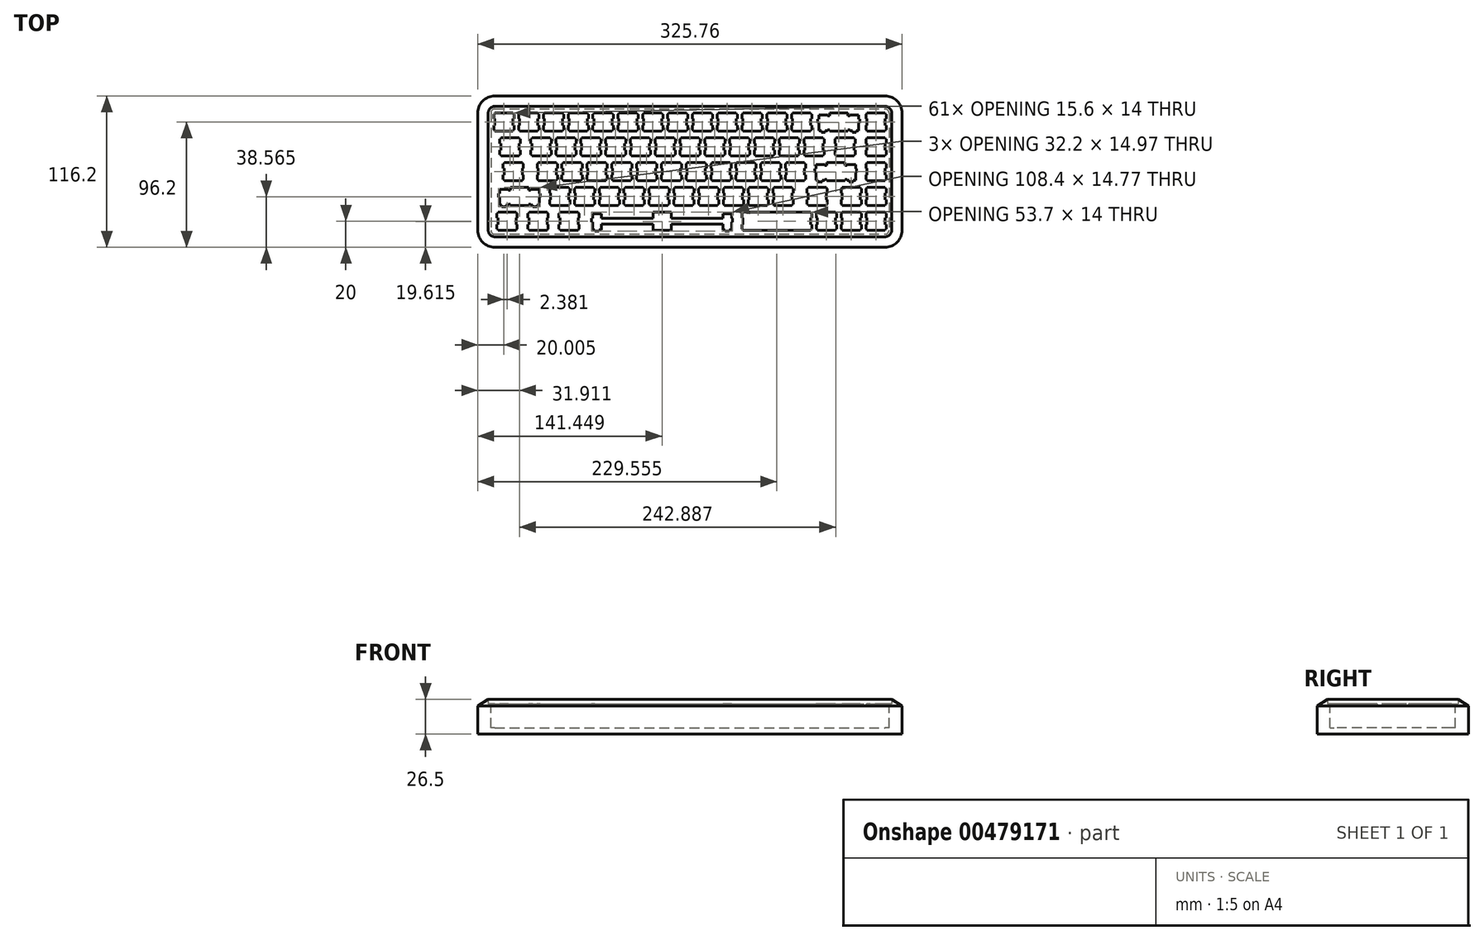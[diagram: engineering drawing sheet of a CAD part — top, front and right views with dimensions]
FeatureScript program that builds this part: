
annotation { "Feature Type Name" : "Feature", "Feature Type Description" : "" }
export const myFeature = defineFeature(function(context is Context, id is Id, definition is map)
    precondition{}
    {
        {
            var Q0;
            Q0=qCreatedBy(makeId("Top.planeOp"),FACE);
            var sketch = newSketch(context, id + "F0", { "sketchPlane" : qUnion([Q0])});
            skLineSegment(sketch, "E0", {"start": v(-116.54, 8.8) * mm, "end": v(-102.54, 8.8) * mm});
            skLineSegment(sketch, "E1", {"start": v(-78.44, 8.8) * mm, "end": v(-64.44, 8.8) * mm});
            skLineSegment(sketch, "E2", {"start": v(-97.49, 8.8) * mm, "end": v(-83.49, 8.8) * mm});
            skLineSegment(sketch, "E3", {"start": v(-40.34, 8.8) * mm, "end": v(-26.34, 8.8) * mm});
            skLineSegment(sketch, "E4", {"start": v(-59.39, 8.8) * mm, "end": v(-45.39, 8.8) * mm});
            skLineSegment(sketch, "E5", {"start": v(-21.29, 8.8) * mm, "end": v(-7.29, 8.8) * mm});
            skLineSegment(sketch, "E6", {"start": v(12.05, 27.85) * mm, "end": v(26.05, 27.85) * mm});
            skLineSegment(sketch, "E7", {"start": v(50.15, 27.85) * mm, "end": v(64.15, 27.85) * mm});
            skLineSegment(sketch, "E8", {"start": v(31.1, 27.85) * mm, "end": v(45.1, 27.85) * mm});
            skLineSegment(sketch, "E9", {"start": v(69.2, 27.85) * mm, "end": v(83.2, 27.85) * mm});
            skLineSegment(sketch, "E10", {"start": v(88.25, 27.85) * mm, "end": v(102.25, 27.85) * mm});
            skLineSegment(sketch, "E11", {"start": v(78.72, 46.9) * mm, "end": v(92.73, 46.9) * mm});
            skLineSegment(sketch, "E12", {"start": v(59.68, 46.9) * mm, "end": v(73.68, 46.9) * mm});
            skLineSegment(sketch, "E13", {"start": v(149.88, 46.9) * mm, "end": v(135.88, 46.9) * mm});
            skLineSegment(sketch, "E14", {"start": v(-145.11, 27.85) * mm, "end": v(-131.11, 27.85) * mm});
            skLineSegment(sketch, "E15", {"start": v(-102.25, 27.85) * mm, "end": v(-88.25, 27.85) * mm});
            skLineSegment(sketch, "E16", {"start": v(-121.3, 27.85) * mm, "end": v(-107.3, 27.85) * mm});
            skLineSegment(sketch, "E17", {"start": v(-83.2, 27.85) * mm, "end": v(-69.2, 27.85) * mm});
            skLineSegment(sketch, "E18", {"start": v(-45.1, 27.85) * mm, "end": v(-31.1, 27.85) * mm});
            skLineSegment(sketch, "E19", {"start": v(-64.15, 27.85) * mm, "end": v(-50.15, 27.85) * mm});
            skLineSegment(sketch, "E20", {"start": v(-7, 27.85) * mm, "end": v(7, 27.85) * mm});
            skLineSegment(sketch, "E21", {"start": v(-26.05, 27.85) * mm, "end": v(-12.05, 27.85) * mm});
            skLineSegment(sketch, "E22", {"start": v(-149.88, 46.9) * mm, "end": v(-135.88, 46.9) * mm});
            skLineSegment(sketch, "E23", {"start": v(-111.78, 46.9) * mm, "end": v(-97.78, 46.9) * mm});
            skLineSegment(sketch, "E24", {"start": v(-130.82, 46.9) * mm, "end": v(-116.83, 46.9) * mm});
            skLineSegment(sketch, "E25", {"start": v(-73.68, 46.9) * mm, "end": v(-59.67, 46.9) * mm});
            skLineSegment(sketch, "E26", {"start": v(-92.73, 46.9) * mm, "end": v(-78.72, 46.9) * mm});
            skLineSegment(sketch, "E27", {"start": v(-54.62, 46.9) * mm, "end": v(-40.62, 46.9) * mm});
            skLineSegment(sketch, "E28", {"start": v(-16.53, 46.9) * mm, "end": v(-2.53, 46.9) * mm});
            skLineSegment(sketch, "E29", {"start": v(-35.58, 46.9) * mm, "end": v(-21.57, 46.9) * mm});
            skLineSegment(sketch, "E30", {"start": v(2.53, 46.9) * mm, "end": v(16.53, 46.9) * mm});
            skLineSegment(sketch, "E31", {"start": v(40.62, 46.9) * mm, "end": v(54.62, 46.9) * mm});
            skLineSegment(sketch, "E32", {"start": v(21.57, 46.9) * mm, "end": v(35.57, 46.9) * mm});
            skLineSegment(sketch, "E33", {"start": v(130.82, -29.3) * mm, "end": v(116.82, -29.3) * mm});
            skLineSegment(sketch, "E34", {"start": v(111.77, -29.3) * mm, "end": v(97.78, -29.3) * mm});
            skLineSegment(sketch, "E35", {"start": v(7.29, -10.25) * mm, "end": v(21.29, -10.25) * mm});
            skLineSegment(sketch, "E36", {"start": v(-11.76, -10.25) * mm, "end": v(2.24, -10.25) * mm});
            skLineSegment(sketch, "E37", {"start": v(26.34, -10.25) * mm, "end": v(40.34, -10.25) * mm});
            skLineSegment(sketch, "E38", {"start": v(64.44, -10.25) * mm, "end": v(78.44, -10.25) * mm});
            skLineSegment(sketch, "E39", {"start": v(45.39, -10.25) * mm, "end": v(59.39, -10.25) * mm});
            skLineSegment(sketch, "E40", {"start": v(90.63, -10.25) * mm, "end": v(104.63, -10.25) * mm});
            skLineSegment(sketch, "E41", {"start": v(149.88, -10.25) * mm, "end": v(135.88, -10.25) * mm});
            skLineSegment(sketch, "E42", {"start": v(130.82, -10.25) * mm, "end": v(116.82, -10.25) * mm});
            skLineSegment(sketch, "E43", {"start": v(-123.68, -29.3) * mm, "end": v(-109.68, -29.3) * mm});
            skLineSegment(sketch, "E44", {"start": v(-147.5, -29.3) * mm, "end": v(-133.5, -29.3) * mm});
            skLineSegment(sketch, "E45", {"start": v(-99.87, -29.3) * mm, "end": v(-85.87, -29.3) * mm});
            skLineSegment(sketch, "E46", {"start": v(149.88, -29.3) * mm, "end": v(135.88, -29.3) * mm});
            skLineSegment(sketch, "E47", {"start": v(-28.43, -29.3) * mm, "end": v(-14.43, -29.3) * mm});
            skLineSegment(sketch, "E48", {"start": v(16.81, 8.8) * mm, "end": v(30.81, 8.8) * mm});
            skLineSegment(sketch, "E49", {"start": v(-2.24, 8.8) * mm, "end": v(11.76, 8.8) * mm});
            skLineSegment(sketch, "E50", {"start": v(35.86, 8.8) * mm, "end": v(49.86, 8.8) * mm});
            skLineSegment(sketch, "E51", {"start": v(73.96, 8.8) * mm, "end": v(87.96, 8.8) * mm});
            skLineSegment(sketch, "E52", {"start": v(54.91, 8.8) * mm, "end": v(68.91, 8.8) * mm});
            skLineSegment(sketch, "E53", {"start": v(149.88, 8.8) * mm, "end": v(135.88, 8.8) * mm});
            skLineSegment(sketch, "E54", {"start": v(-87.96, -10.25) * mm, "end": v(-73.96, -10.25) * mm});
            skLineSegment(sketch, "E55", {"start": v(-107.01, -10.25) * mm, "end": v(-93.01, -10.25) * mm});
            skLineSegment(sketch, "E56", {"start": v(-68.91, -10.25) * mm, "end": v(-54.91, -10.25) * mm});
            skLineSegment(sketch, "E57", {"start": v(-30.81, -10.25) * mm, "end": v(-16.81, -10.25) * mm});
            skLineSegment(sketch, "E58", {"start": v(-49.86, -10.25) * mm, "end": v(-35.86, -10.25) * mm});
            skLineSegment(sketch, "E59", {"start": v(112.06, 27.85) * mm, "end": v(126.06, 27.85) * mm});
            skLineSegment(sketch, "E60", {"start": v(-142.73, 8.8) * mm, "end": v(-128.73, 8.8) * mm});
            skLineSegment(sketch, "E61", {"start": v(149.88, 27.85) * mm, "end": v(135.88, 27.85) * mm});
            skLineSegment(sketch, "E62", {"start": v(-116.54, 8.8) * mm, "end": v(-116.54, 7.8) * mm});
            skLineSegment(sketch, "E63", {"start": v(-102.54, 8.8) * mm, "end": v(-102.54, 7.8) * mm});
            skLineSegment(sketch, "E64", {"start": v(-64.44, 8.8) * mm, "end": v(-64.44, 7.8) * mm});
            skLineSegment(sketch, "E65", {"start": v(-78.44, 8.8) * mm, "end": v(-78.44, 7.8) * mm});
            skLineSegment(sketch, "E66", {"start": v(-83.49, 8.8) * mm, "end": v(-83.49, 7.8) * mm});
            skLineSegment(sketch, "E67", {"start": v(-97.49, 8.8) * mm, "end": v(-97.49, 7.8) * mm});
            skLineSegment(sketch, "E68", {"start": v(-26.34, 8.8) * mm, "end": v(-26.34, 7.8) * mm});
            skLineSegment(sketch, "E69", {"start": v(-40.34, 8.8) * mm, "end": v(-40.34, 7.8) * mm});
            skLineSegment(sketch, "E70", {"start": v(-45.39, 8.8) * mm, "end": v(-45.39, 7.8) * mm});
            skLineSegment(sketch, "E71", {"start": v(-59.39, 8.8) * mm, "end": v(-59.39, 7.8) * mm});
            skLineSegment(sketch, "E72", {"start": v(-7.29, 8.8) * mm, "end": v(-7.29, 7.8) * mm});
            skLineSegment(sketch, "E73", {"start": v(-21.29, 8.8) * mm, "end": v(-21.29, 7.8) * mm});
            skLineSegment(sketch, "E74", {"start": v(26.05, 27.85) * mm, "end": v(26.05, 26.85) * mm});
            skLineSegment(sketch, "E75", {"start": v(12.05, 27.85) * mm, "end": v(12.05, 26.85) * mm});
            skLineSegment(sketch, "E76", {"start": v(64.15, 27.85) * mm, "end": v(64.15, 26.85) * mm});
            skLineSegment(sketch, "E77", {"start": v(50.15, 27.85) * mm, "end": v(50.15, 26.85) * mm});
            skLineSegment(sketch, "E78", {"start": v(45.1, 27.85) * mm, "end": v(45.1, 26.85) * mm});
            skLineSegment(sketch, "E79", {"start": v(31.1, 27.85) * mm, "end": v(31.1, 26.85) * mm});
            skLineSegment(sketch, "E80", {"start": v(83.2, 27.85) * mm, "end": v(83.2, 26.85) * mm});
            skLineSegment(sketch, "E81", {"start": v(69.2, 27.85) * mm, "end": v(69.2, 26.85) * mm});
            skLineSegment(sketch, "E82", {"start": v(102.25, 27.85) * mm, "end": v(102.25, 26.85) * mm});
            skLineSegment(sketch, "E83", {"start": v(88.25, 27.85) * mm, "end": v(88.25, 26.85) * mm});
            skLineSegment(sketch, "E84", {"start": v(73.68, 46.9) * mm, "end": v(73.68, 45.9) * mm});
            skLineSegment(sketch, "E85", {"start": v(59.68, 46.9) * mm, "end": v(59.68, 45.9) * mm});
            skLineSegment(sketch, "E86", {"start": v(92.73, 46.9) * mm, "end": v(92.73, 45.9) * mm});
            skLineSegment(sketch, "E87", {"start": v(78.72, 46.9) * mm, "end": v(78.72, 45.9) * mm});
            skLineSegment(sketch, "E88", {"start": v(149.88, 46.9) * mm, "end": v(149.88, 45.9) * mm});
            skLineSegment(sketch, "E89", {"start": v(-131.11, 27.85) * mm, "end": v(-131.11, 26.85) * mm});
            skLineSegment(sketch, "E90", {"start": v(-145.11, 27.85) * mm, "end": v(-145.11, 26.85) * mm});
            skLineSegment(sketch, "E91", {"start": v(135.88, 46.9) * mm, "end": v(135.88, 45.9) * mm});
            skLineSegment(sketch, "E92", {"start": v(-88.25, 27.85) * mm, "end": v(-88.25, 26.85) * mm});
            skLineSegment(sketch, "E93", {"start": v(-102.25, 27.85) * mm, "end": v(-102.25, 26.85) * mm});
            skLineSegment(sketch, "E94", {"start": v(-121.3, 27.85) * mm, "end": v(-121.3, 26.85) * mm});
            skLineSegment(sketch, "E95", {"start": v(-107.3, 27.85) * mm, "end": v(-107.3, 26.85) * mm});
            skLineSegment(sketch, "E96", {"start": v(-69.2, 27.85) * mm, "end": v(-69.2, 26.85) * mm});
            skLineSegment(sketch, "E97", {"start": v(-83.2, 27.85) * mm, "end": v(-83.2, 26.85) * mm});
            skLineSegment(sketch, "E98", {"start": v(-31.1, 27.85) * mm, "end": v(-31.1, 26.85) * mm});
            skLineSegment(sketch, "E99", {"start": v(-45.1, 27.85) * mm, "end": v(-45.1, 26.85) * mm});
            skLineSegment(sketch, "E100", {"start": v(-50.15, 27.85) * mm, "end": v(-50.15, 26.85) * mm});
            skLineSegment(sketch, "E101", {"start": v(-64.15, 27.85) * mm, "end": v(-64.15, 26.85) * mm});
            skLineSegment(sketch, "E102", {"start": v(7, 27.85) * mm, "end": v(7, 26.85) * mm});
            skLineSegment(sketch, "E103", {"start": v(-7, 27.85) * mm, "end": v(-7, 26.85) * mm});
            skLineSegment(sketch, "E104", {"start": v(-12.05, 27.85) * mm, "end": v(-12.05, 26.85) * mm});
            skLineSegment(sketch, "E105", {"start": v(-26.05, 27.85) * mm, "end": v(-26.05, 26.85) * mm});
            skLineSegment(sketch, "E106", {"start": v(-149.88, 46.9) * mm, "end": v(-149.88, 45.9) * mm});
            skLineSegment(sketch, "E107", {"start": v(-135.88, 46.9) * mm, "end": v(-135.88, 45.9) * mm});
            skLineSegment(sketch, "E108", {"start": v(-97.78, 46.9) * mm, "end": v(-97.78, 45.9) * mm});
            skLineSegment(sketch, "E109", {"start": v(-111.78, 46.9) * mm, "end": v(-111.78, 45.9) * mm});
            skLineSegment(sketch, "E110", {"start": v(-116.83, 46.9) * mm, "end": v(-116.83, 45.9) * mm});
            skLineSegment(sketch, "E111", {"start": v(-130.82, 46.9) * mm, "end": v(-130.82, 45.9) * mm});
            skLineSegment(sketch, "E112", {"start": v(-78.72, 46.9) * mm, "end": v(-78.72, 45.9) * mm});
            skLineSegment(sketch, "E113", {"start": v(-92.73, 46.9) * mm, "end": v(-92.73, 45.9) * mm});
            skLineSegment(sketch, "E114", {"start": v(-40.62, 46.9) * mm, "end": v(-40.62, 45.9) * mm});
            skLineSegment(sketch, "E115", {"start": v(-54.62, 46.9) * mm, "end": v(-54.62, 45.9) * mm});
            skLineSegment(sketch, "E116", {"start": v(-59.67, 46.9) * mm, "end": v(-59.67, 45.9) * mm});
            skLineSegment(sketch, "E117", {"start": v(-73.68, 46.9) * mm, "end": v(-73.68, 45.9) * mm});
            skLineSegment(sketch, "E118", {"start": v(-2.53, 46.9) * mm, "end": v(-2.53, 45.9) * mm});
            skLineSegment(sketch, "E119", {"start": v(-16.53, 46.9) * mm, "end": v(-16.53, 45.9) * mm});
            skLineSegment(sketch, "E120", {"start": v(-21.57, 46.9) * mm, "end": v(-21.57, 45.9) * mm});
            skLineSegment(sketch, "E121", {"start": v(-35.58, 46.9) * mm, "end": v(-35.58, 45.9) * mm});
            skLineSegment(sketch, "E122", {"start": v(16.53, 46.9) * mm, "end": v(16.53, 45.9) * mm});
            skLineSegment(sketch, "E123", {"start": v(2.53, 46.9) * mm, "end": v(2.53, 45.9) * mm});
            skLineSegment(sketch, "E124", {"start": v(54.62, 46.9) * mm, "end": v(54.62, 45.9) * mm});
            skLineSegment(sketch, "E125", {"start": v(40.62, 46.9) * mm, "end": v(40.62, 45.9) * mm});
            skLineSegment(sketch, "E126", {"start": v(35.57, 46.9) * mm, "end": v(35.57, 45.9) * mm});
            skLineSegment(sketch, "E127", {"start": v(21.57, 46.9) * mm, "end": v(21.57, 45.9) * mm});
            skLineSegment(sketch, "E128", {"start": v(130.82, -29.3) * mm, "end": v(130.82, -30.3) * mm});
            skLineSegment(sketch, "E129", {"start": v(116.82, -29.3) * mm, "end": v(116.82, -30.3) * mm});
            skLineSegment(sketch, "E130", {"start": v(92.73, -29.3) * mm, "end": v(92.73, -30.3) * mm});
            skLineSegment(sketch, "E131", {"start": v(111.77, -29.3) * mm, "end": v(111.77, -30.3) * mm});
            skLineSegment(sketch, "E132", {"start": v(97.78, -29.3) * mm, "end": v(97.78, -30.3) * mm});
            skLineSegment(sketch, "E133", {"start": v(40.62, -29.3) * mm, "end": v(40.62, -30.3) * mm});
            skLineSegment(sketch, "E134", {"start": v(21.29, -10.25) * mm, "end": v(21.29, -11.25) * mm});
            skLineSegment(sketch, "E135", {"start": v(7.29, -10.25) * mm, "end": v(7.29, -11.25) * mm});
            skLineSegment(sketch, "E136", {"start": v(2.24, -10.25) * mm, "end": v(2.24, -11.25) * mm});
            skLineSegment(sketch, "E137", {"start": v(-11.76, -10.25) * mm, "end": v(-11.76, -11.25) * mm});
            skLineSegment(sketch, "E138", {"start": v(40.34, -10.25) * mm, "end": v(40.34, -11.25) * mm});
            skLineSegment(sketch, "E139", {"start": v(26.34, -10.25) * mm, "end": v(26.34, -11.25) * mm});
            skLineSegment(sketch, "E140", {"start": v(78.44, -10.25) * mm, "end": v(78.44, -11.25) * mm});
            skLineSegment(sketch, "E141", {"start": v(64.44, -10.25) * mm, "end": v(64.44, -11.25) * mm});
            skLineSegment(sketch, "E142", {"start": v(59.39, -10.25) * mm, "end": v(59.39, -11.25) * mm});
            skLineSegment(sketch, "E143", {"start": v(45.39, -10.25) * mm, "end": v(45.39, -11.25) * mm});
            skLineSegment(sketch, "E144", {"start": v(90.63, -10.25) * mm, "end": v(90.63, -11.25) * mm});
            skLineSegment(sketch, "E145", {"start": v(104.63, -10.25) * mm, "end": v(104.63, -11.25) * mm});
            skLineSegment(sketch, "E146", {"start": v(116.82, -10.25) * mm, "end": v(116.82, -11.25) * mm});
            skLineSegment(sketch, "E147", {"start": v(149.88, -10.25) * mm, "end": v(149.88, -11.25) * mm});
            skLineSegment(sketch, "E148", {"start": v(135.88, -10.25) * mm, "end": v(135.88, -11.25) * mm});
            skLineSegment(sketch, "E149", {"start": v(130.82, -10.25) * mm, "end": v(130.82, -11.25) * mm});
            skLineSegment(sketch, "E150", {"start": v(-123.68, -29.3) * mm, "end": v(-123.68, -30.3) * mm});
            skLineSegment(sketch, "E151", {"start": v(-109.68, -29.3) * mm, "end": v(-109.68, -30.3) * mm});
            skLineSegment(sketch, "E152", {"start": v(-133.5, -29.3) * mm, "end": v(-133.5, -30.3) * mm});
            skLineSegment(sketch, "E153", {"start": v(-147.5, -29.3) * mm, "end": v(-147.5, -30.3) * mm});
            skLineSegment(sketch, "E154", {"start": v(-99.87, -29.3) * mm, "end": v(-99.87, -30.3) * mm});
            skLineSegment(sketch, "E155", {"start": v(-85.87, -29.3) * mm, "end": v(-85.87, -30.3) * mm});
            skLineSegment(sketch, "E156", {"start": v(135.88, -29.3) * mm, "end": v(135.88, -30.3) * mm});
            skLineSegment(sketch, "E157", {"start": v(149.88, -29.3) * mm, "end": v(149.88, -30.3) * mm});
            skLineSegment(sketch, "E158", {"start": v(30.81, 8.8) * mm, "end": v(30.81, 7.8) * mm});
            skLineSegment(sketch, "E159", {"start": v(16.81, 8.8) * mm, "end": v(16.81, 7.8) * mm});
            skLineSegment(sketch, "E160", {"start": v(11.76, 8.8) * mm, "end": v(11.76, 7.8) * mm});
            skLineSegment(sketch, "E161", {"start": v(-2.24, 8.8) * mm, "end": v(-2.24, 7.8) * mm});
            skLineSegment(sketch, "E162", {"start": v(49.86, 8.8) * mm, "end": v(49.86, 7.8) * mm});
            skLineSegment(sketch, "E163", {"start": v(35.86, 8.8) * mm, "end": v(35.86, 7.8) * mm});
            skLineSegment(sketch, "E164", {"start": v(87.96, 8.8) * mm, "end": v(87.96, 7.8) * mm});
            skLineSegment(sketch, "E165", {"start": v(73.96, 8.8) * mm, "end": v(73.96, 7.8) * mm});
            skLineSegment(sketch, "E166", {"start": v(68.91, 8.8) * mm, "end": v(68.91, 7.8) * mm});
            skLineSegment(sketch, "E167", {"start": v(54.91, 8.8) * mm, "end": v(54.91, 7.8) * mm});
            skLineSegment(sketch, "E168", {"start": v(135.88, 8.8) * mm, "end": v(135.88, 7.8) * mm});
            skLineSegment(sketch, "E169", {"start": v(149.88, 8.8) * mm, "end": v(149.88, 7.8) * mm});
            skLineSegment(sketch, "E170", {"start": v(-73.96, -10.25) * mm, "end": v(-73.96, -11.25) * mm});
            skLineSegment(sketch, "E171", {"start": v(-87.96, -10.25) * mm, "end": v(-87.96, -11.25) * mm});
            skLineSegment(sketch, "E172", {"start": v(-107.01, -10.25) * mm, "end": v(-107.01, -11.25) * mm});
            skLineSegment(sketch, "E173", {"start": v(-93.01, -10.25) * mm, "end": v(-93.01, -11.25) * mm});
            skLineSegment(sketch, "E174", {"start": v(-54.91, -10.25) * mm, "end": v(-54.91, -11.25) * mm});
            skLineSegment(sketch, "E175", {"start": v(-68.91, -10.25) * mm, "end": v(-68.91, -11.25) * mm});
            skLineSegment(sketch, "E176", {"start": v(-16.81, -10.25) * mm, "end": v(-16.81, -11.25) * mm});
            skLineSegment(sketch, "E177", {"start": v(-30.81, -10.25) * mm, "end": v(-30.81, -11.25) * mm});
            skLineSegment(sketch, "E178", {"start": v(-35.86, -10.25) * mm, "end": v(-35.86, -11.25) * mm});
            skLineSegment(sketch, "E179", {"start": v(-49.86, -10.25) * mm, "end": v(-49.86, -11.25) * mm});
            skLineSegment(sketch, "E180", {"start": v(112.06, 27.85) * mm, "end": v(112.06, 26.85) * mm});
            skLineSegment(sketch, "E181", {"start": v(126.06, 27.85) * mm, "end": v(126.06, 26.85) * mm});
            skLineSegment(sketch, "E182", {"start": v(-128.73, 8.8) * mm, "end": v(-128.73, 7.8) * mm});
            skLineSegment(sketch, "E183", {"start": v(-142.73, 8.8) * mm, "end": v(-142.73, 7.8) * mm});
            skLineSegment(sketch, "E184", {"start": v(135.88, 27.85) * mm, "end": v(135.88, 26.85) * mm});
            skLineSegment(sketch, "E185", {"start": v(149.88, 27.85) * mm, "end": v(149.88, 26.85) * mm});
            skLineSegment(sketch, "E186", {"start": v(-116.54, 7.8) * mm, "end": v(-117.34, 7.8) * mm});
            skLineSegment(sketch, "E187", {"start": v(-102.54, 7.8) * mm, "end": v(-101.74, 7.8) * mm});
            skLineSegment(sketch, "E188", {"start": v(-64.44, 7.8) * mm, "end": v(-63.64, 7.8) * mm});
            skLineSegment(sketch, "E189", {"start": v(-78.44, 7.8) * mm, "end": v(-79.24, 7.8) * mm});
            skLineSegment(sketch, "E190", {"start": v(-83.49, 7.8) * mm, "end": v(-82.69, 7.8) * mm});
            skLineSegment(sketch, "E191", {"start": v(-97.49, 7.8) * mm, "end": v(-98.29, 7.8) * mm});
            skLineSegment(sketch, "E192", {"start": v(-45.39, 7.8) * mm, "end": v(-44.59, 7.8) * mm});
            skLineSegment(sketch, "E193", {"start": v(-59.39, 7.8) * mm, "end": v(-60.19, 7.8) * mm});
            skLineSegment(sketch, "E194", {"start": v(-7.29, 7.8) * mm, "end": v(-6.49, 7.8) * mm});
            skLineSegment(sketch, "E195", {"start": v(-21.29, 7.8) * mm, "end": v(-22.09, 7.8) * mm});
            skLineSegment(sketch, "E196", {"start": v(-26.34, 7.8) * mm, "end": v(-25.54, 7.8) * mm});
            skLineSegment(sketch, "E197", {"start": v(-40.34, 7.8) * mm, "end": v(-41.14, 7.8) * mm});
            skLineSegment(sketch, "E198", {"start": v(26.05, 26.85) * mm, "end": v(26.85, 26.85) * mm});
            skLineSegment(sketch, "E199", {"start": v(12.05, 26.85) * mm, "end": v(11.25, 26.85) * mm});
            skLineSegment(sketch, "E200", {"start": v(7, 26.85) * mm, "end": v(7.8, 26.85) * mm});
            skLineSegment(sketch, "E201", {"start": v(-7, 26.85) * mm, "end": v(-7.8, 26.85) * mm});
            skLineSegment(sketch, "E202", {"start": v(64.15, 26.85) * mm, "end": v(64.95, 26.85) * mm});
            skLineSegment(sketch, "E203", {"start": v(50.15, 26.85) * mm, "end": v(49.35, 26.85) * mm});
            skLineSegment(sketch, "E204", {"start": v(45.1, 26.85) * mm, "end": v(45.9, 26.85) * mm});
            skLineSegment(sketch, "E205", {"start": v(31.1, 26.85) * mm, "end": v(30.3, 26.85) * mm});
            skLineSegment(sketch, "E206", {"start": v(83.2, 26.85) * mm, "end": v(84, 26.85) * mm});
            skLineSegment(sketch, "E207", {"start": v(69.2, 26.85) * mm, "end": v(68.4, 26.85) * mm});
            skLineSegment(sketch, "E208", {"start": v(102.25, 26.85) * mm, "end": v(103.05, 26.85) * mm});
            skLineSegment(sketch, "E209", {"start": v(88.25, 26.85) * mm, "end": v(87.45, 26.85) * mm});
            skLineSegment(sketch, "E210", {"start": v(73.68, 45.9) * mm, "end": v(74.47, 45.9) * mm});
            skLineSegment(sketch, "E211", {"start": v(59.68, 45.9) * mm, "end": v(58.88, 45.9) * mm});
            skLineSegment(sketch, "E212", {"start": v(92.73, 45.9) * mm, "end": v(93.53, 45.9) * mm});
            skLineSegment(sketch, "E213", {"start": v(78.72, 45.9) * mm, "end": v(77.93, 45.9) * mm});
            skLineSegment(sketch, "E214", {"start": v(149.88, 45.9) * mm, "end": v(150.68, 45.9) * mm});
            skLineSegment(sketch, "E215", {"start": v(135.88, 45.9) * mm, "end": v(135.07, 45.9) * mm});
            skLineSegment(sketch, "E216", {"start": v(-131.11, 26.85) * mm, "end": v(-130.31, 26.85) * mm});
            skLineSegment(sketch, "E217", {"start": v(-145.11, 26.85) * mm, "end": v(-145.91, 26.85) * mm});
            skLineSegment(sketch, "E218", {"start": v(-88.25, 26.85) * mm, "end": v(-87.45, 26.85) * mm});
            skLineSegment(sketch, "E219", {"start": v(-102.25, 26.85) * mm, "end": v(-103.05, 26.85) * mm});
            skLineSegment(sketch, "E220", {"start": v(-121.3, 26.85) * mm, "end": v(-122.1, 26.85) * mm});
            skLineSegment(sketch, "E221", {"start": v(-107.3, 26.85) * mm, "end": v(-106.5, 26.85) * mm});
            skLineSegment(sketch, "E222", {"start": v(-69.2, 26.85) * mm, "end": v(-68.4, 26.85) * mm});
            skLineSegment(sketch, "E223", {"start": v(-83.2, 26.85) * mm, "end": v(-84, 26.85) * mm});
            skLineSegment(sketch, "E224", {"start": v(-31.1, 26.85) * mm, "end": v(-30.3, 26.85) * mm});
            skLineSegment(sketch, "E225", {"start": v(-45.1, 26.85) * mm, "end": v(-45.9, 26.85) * mm});
            skLineSegment(sketch, "E226", {"start": v(-50.15, 26.85) * mm, "end": v(-49.35, 26.85) * mm});
            skLineSegment(sketch, "E227", {"start": v(-64.15, 26.85) * mm, "end": v(-64.95, 26.85) * mm});
            skLineSegment(sketch, "E228", {"start": v(-12.05, 26.85) * mm, "end": v(-11.25, 26.85) * mm});
            skLineSegment(sketch, "E229", {"start": v(-26.05, 26.85) * mm, "end": v(-26.85, 26.85) * mm});
            skLineSegment(sketch, "E230", {"start": v(-149.88, 45.9) * mm, "end": v(-150.68, 45.9) * mm});
            skLineSegment(sketch, "E231", {"start": v(-135.88, 45.9) * mm, "end": v(-135.07, 45.9) * mm});
            skLineSegment(sketch, "E232", {"start": v(-97.78, 45.9) * mm, "end": v(-96.97, 45.9) * mm});
            skLineSegment(sketch, "E233", {"start": v(-111.78, 45.9) * mm, "end": v(-112.58, 45.9) * mm});
            skLineSegment(sketch, "E234", {"start": v(-116.83, 45.9) * mm, "end": v(-116.03, 45.9) * mm});
            skLineSegment(sketch, "E235", {"start": v(-130.82, 45.9) * mm, "end": v(-131.62, 45.9) * mm});
            skLineSegment(sketch, "E236", {"start": v(-78.72, 45.9) * mm, "end": v(-77.92, 45.9) * mm});
            skLineSegment(sketch, "E237", {"start": v(-92.73, 45.9) * mm, "end": v(-93.53, 45.9) * mm});
            skLineSegment(sketch, "E238", {"start": v(-40.62, 45.9) * mm, "end": v(-39.83, 45.9) * mm});
            skLineSegment(sketch, "E239", {"start": v(-54.62, 45.9) * mm, "end": v(-55.42, 45.9) * mm});
            skLineSegment(sketch, "E240", {"start": v(-59.67, 45.9) * mm, "end": v(-58.88, 45.9) * mm});
            skLineSegment(sketch, "E241", {"start": v(-73.68, 45.9) * mm, "end": v(-74.47, 45.9) * mm});
            skLineSegment(sketch, "E242", {"start": v(-2.53, 45.9) * mm, "end": v(-1.72, 45.9) * mm});
            skLineSegment(sketch, "E243", {"start": v(-16.53, 45.9) * mm, "end": v(-17.32, 45.9) * mm});
            skLineSegment(sketch, "E244", {"start": v(-21.57, 45.9) * mm, "end": v(-20.78, 45.9) * mm});
            skLineSegment(sketch, "E245", {"start": v(-35.58, 45.9) * mm, "end": v(-36.38, 45.9) * mm});
            skLineSegment(sketch, "E246", {"start": v(16.53, 45.9) * mm, "end": v(17.32, 45.9) * mm});
            skLineSegment(sketch, "E247", {"start": v(2.53, 45.9) * mm, "end": v(1.72, 45.9) * mm});
            skLineSegment(sketch, "E248", {"start": v(54.62, 45.9) * mm, "end": v(55.43, 45.9) * mm});
            skLineSegment(sketch, "E249", {"start": v(40.62, 45.9) * mm, "end": v(39.82, 45.9) * mm});
            skLineSegment(sketch, "E250", {"start": v(35.57, 45.9) * mm, "end": v(36.38, 45.9) * mm});
            skLineSegment(sketch, "E251", {"start": v(21.57, 45.9) * mm, "end": v(20.78, 45.9) * mm});
            skLineSegment(sketch, "E252", {"start": v(130.82, -30.3) * mm, "end": v(131.62, -30.3) * mm});
            skLineSegment(sketch, "E253", {"start": v(116.82, -30.3) * mm, "end": v(116.02, -30.3) * mm});
            skLineSegment(sketch, "E254", {"start": v(92.73, -30.3) * mm, "end": v(93.53, -30.3) * mm});
            skLineSegment(sketch, "E255", {"start": v(111.77, -30.3) * mm, "end": v(112.57, -30.3) * mm});
            skLineSegment(sketch, "E256", {"start": v(97.78, -30.3) * mm, "end": v(96.97, -30.3) * mm});
            skLineSegment(sketch, "E257", {"start": v(40.62, -30.3) * mm, "end": v(39.82, -30.3) * mm});
            skLineSegment(sketch, "E258", {"start": v(2.24, -11.25) * mm, "end": v(3.04, -11.25) * mm});
            skLineSegment(sketch, "E259", {"start": v(-11.76, -11.25) * mm, "end": v(-12.56, -11.25) * mm});
            skLineSegment(sketch, "E260", {"start": v(40.34, -11.25) * mm, "end": v(41.14, -11.25) * mm});
            skLineSegment(sketch, "E261", {"start": v(26.34, -11.25) * mm, "end": v(25.54, -11.25) * mm});
            skLineSegment(sketch, "E262", {"start": v(21.29, -11.25) * mm, "end": v(22.09, -11.25) * mm});
            skLineSegment(sketch, "E263", {"start": v(7.29, -11.25) * mm, "end": v(6.49, -11.25) * mm});
            skLineSegment(sketch, "E264", {"start": v(78.44, -11.25) * mm, "end": v(79.24, -11.25) * mm});
            skLineSegment(sketch, "E265", {"start": v(64.44, -11.25) * mm, "end": v(63.64, -11.25) * mm});
            skLineSegment(sketch, "E266", {"start": v(59.39, -11.25) * mm, "end": v(60.19, -11.25) * mm});
            skLineSegment(sketch, "E267", {"start": v(45.39, -11.25) * mm, "end": v(44.59, -11.25) * mm});
            skLineSegment(sketch, "E268", {"start": v(90.63, -11.25) * mm, "end": v(89.83, -11.25) * mm});
            skLineSegment(sketch, "E269", {"start": v(104.63, -11.25) * mm, "end": v(105.43, -11.25) * mm});
            skLineSegment(sketch, "E270", {"start": v(149.88, -11.25) * mm, "end": v(150.68, -11.25) * mm});
            skLineSegment(sketch, "E271", {"start": v(135.88, -11.25) * mm, "end": v(135.07, -11.25) * mm});
            skLineSegment(sketch, "E272", {"start": v(116.82, -11.25) * mm, "end": v(116.02, -11.25) * mm});
            skLineSegment(sketch, "E273", {"start": v(130.82, -11.25) * mm, "end": v(131.62, -11.25) * mm});
            skLineSegment(sketch, "E274", {"start": v(-133.5, -30.3) * mm, "end": v(-132.7, -30.3) * mm});
            skLineSegment(sketch, "E275", {"start": v(-147.5, -30.3) * mm, "end": v(-148.3, -30.3) * mm});
            skLineSegment(sketch, "E276", {"start": v(-99.87, -30.3) * mm, "end": v(-100.67, -30.3) * mm});
            skLineSegment(sketch, "E277", {"start": v(-85.87, -30.3) * mm, "end": v(-85.07, -30.3) * mm});
            skLineSegment(sketch, "E278", {"start": v(-123.68, -30.3) * mm, "end": v(-124.48, -30.3) * mm});
            skLineSegment(sketch, "E279", {"start": v(-109.68, -30.3) * mm, "end": v(-108.88, -30.3) * mm});
            skLineSegment(sketch, "E280", {"start": v(135.88, -30.3) * mm, "end": v(135.07, -30.3) * mm});
            skLineSegment(sketch, "E281", {"start": v(149.88, -30.3) * mm, "end": v(150.68, -30.3) * mm});
            skLineSegment(sketch, "E282", {"start": v(30.81, 7.8) * mm, "end": v(31.61, 7.8) * mm});
            skLineSegment(sketch, "E283", {"start": v(16.81, 7.8) * mm, "end": v(16.01, 7.8) * mm});
            skLineSegment(sketch, "E284", {"start": v(11.76, 7.8) * mm, "end": v(12.56, 7.8) * mm});
            skLineSegment(sketch, "E285", {"start": v(-2.24, 7.8) * mm, "end": v(-3.04, 7.8) * mm});
            skLineSegment(sketch, "E286", {"start": v(49.86, 7.8) * mm, "end": v(50.66, 7.8) * mm});
            skLineSegment(sketch, "E287", {"start": v(35.86, 7.8) * mm, "end": v(35.06, 7.8) * mm});
            skLineSegment(sketch, "E288", {"start": v(87.96, 7.8) * mm, "end": v(88.76, 7.8) * mm});
            skLineSegment(sketch, "E289", {"start": v(73.96, 7.8) * mm, "end": v(73.16, 7.8) * mm});
            skLineSegment(sketch, "E290", {"start": v(68.91, 7.8) * mm, "end": v(69.71, 7.8) * mm});
            skLineSegment(sketch, "E291", {"start": v(54.91, 7.8) * mm, "end": v(54.11, 7.8) * mm});
            skLineSegment(sketch, "E292", {"start": v(135.88, 7.8) * mm, "end": v(135.07, 7.8) * mm});
            skLineSegment(sketch, "E293", {"start": v(149.88, 7.8) * mm, "end": v(150.68, 7.8) * mm});
            skLineSegment(sketch, "E294", {"start": v(-73.96, -11.25) * mm, "end": v(-73.16, -11.25) * mm});
            skLineSegment(sketch, "E295", {"start": v(-87.96, -11.25) * mm, "end": v(-88.76, -11.25) * mm});
            skLineSegment(sketch, "E296", {"start": v(-107.01, -11.25) * mm, "end": v(-107.81, -11.25) * mm});
            skLineSegment(sketch, "E297", {"start": v(-93.01, -11.25) * mm, "end": v(-92.21, -11.25) * mm});
            skLineSegment(sketch, "E298", {"start": v(-54.91, -11.25) * mm, "end": v(-54.11, -11.25) * mm});
            skLineSegment(sketch, "E299", {"start": v(-68.91, -11.25) * mm, "end": v(-69.71, -11.25) * mm});
            skLineSegment(sketch, "E300", {"start": v(-16.81, -11.25) * mm, "end": v(-16.01, -11.25) * mm});
            skLineSegment(sketch, "E301", {"start": v(-30.81, -11.25) * mm, "end": v(-31.61, -11.25) * mm});
            skLineSegment(sketch, "E302", {"start": v(-35.86, -11.25) * mm, "end": v(-35.06, -11.25) * mm});
            skLineSegment(sketch, "E303", {"start": v(-49.86, -11.25) * mm, "end": v(-50.66, -11.25) * mm});
            skLineSegment(sketch, "E304", {"start": v(112.06, 26.85) * mm, "end": v(111.26, 26.85) * mm});
            skLineSegment(sketch, "E305", {"start": v(126.06, 26.85) * mm, "end": v(126.86, 26.85) * mm});
            skLineSegment(sketch, "E306", {"start": v(-128.73, 7.8) * mm, "end": v(-127.93, 7.8) * mm});
            skLineSegment(sketch, "E307", {"start": v(-142.73, 7.8) * mm, "end": v(-143.53, 7.8) * mm});
            skLineSegment(sketch, "E308", {"start": v(135.88, 26.85) * mm, "end": v(135.07, 26.85) * mm});
            skLineSegment(sketch, "E309", {"start": v(149.88, 26.85) * mm, "end": v(150.68, 26.85) * mm});
            skLineSegment(sketch, "E310", {"start": v(-117.34, 7.8) * mm, "end": v(-117.34, 4.3) * mm});
            skLineSegment(sketch, "E311", {"start": v(-101.74, 7.8) * mm, "end": v(-101.74, 4.3) * mm});
            skLineSegment(sketch, "E312", {"start": v(-63.64, 7.8) * mm, "end": v(-63.64, 4.3) * mm});
            skLineSegment(sketch, "E313", {"start": v(-79.24, 7.8) * mm, "end": v(-79.24, 4.3) * mm});
            skLineSegment(sketch, "E314", {"start": v(-82.69, 7.8) * mm, "end": v(-82.69, 4.3) * mm});
            skLineSegment(sketch, "E315", {"start": v(-98.29, 7.8) * mm, "end": v(-98.29, 4.3) * mm});
            skLineSegment(sketch, "E316", {"start": v(-44.59, 7.8) * mm, "end": v(-44.59, 4.3) * mm});
            skLineSegment(sketch, "E317", {"start": v(-60.19, 7.8) * mm, "end": v(-60.19, 4.3) * mm});
            skLineSegment(sketch, "E318", {"start": v(-6.49, 7.8) * mm, "end": v(-6.49, 4.3) * mm});
            skLineSegment(sketch, "E319", {"start": v(-22.09, 7.8) * mm, "end": v(-22.09, 4.3) * mm});
            skLineSegment(sketch, "E320", {"start": v(-25.54, 7.8) * mm, "end": v(-25.54, 4.3) * mm});
            skLineSegment(sketch, "E321", {"start": v(-41.14, 7.8) * mm, "end": v(-41.14, 4.3) * mm});
            skLineSegment(sketch, "E322", {"start": v(26.85, 26.85) * mm, "end": v(26.85, 23.35) * mm});
            skLineSegment(sketch, "E323", {"start": v(11.25, 26.85) * mm, "end": v(11.25, 23.35) * mm});
            skLineSegment(sketch, "E324", {"start": v(7.8, 26.85) * mm, "end": v(7.8, 23.35) * mm});
            skLineSegment(sketch, "E325", {"start": v(-7.8, 26.85) * mm, "end": v(-7.8, 23.35) * mm});
            skLineSegment(sketch, "E326", {"start": v(64.95, 26.85) * mm, "end": v(64.95, 23.35) * mm});
            skLineSegment(sketch, "E327", {"start": v(49.35, 26.85) * mm, "end": v(49.35, 23.35) * mm});
            skLineSegment(sketch, "E328", {"start": v(45.9, 26.85) * mm, "end": v(45.9, 23.35) * mm});
            skLineSegment(sketch, "E329", {"start": v(30.3, 26.85) * mm, "end": v(30.3, 23.35) * mm});
            skLineSegment(sketch, "E330", {"start": v(84, 26.85) * mm, "end": v(84, 23.35) * mm});
            skLineSegment(sketch, "E331", {"start": v(68.4, 26.85) * mm, "end": v(68.4, 23.35) * mm});
            skLineSegment(sketch, "E332", {"start": v(103.05, 26.85) * mm, "end": v(103.05, 23.35) * mm});
            skLineSegment(sketch, "E333", {"start": v(87.45, 26.85) * mm, "end": v(87.45, 23.35) * mm});
            skLineSegment(sketch, "E334", {"start": v(74.47, 45.9) * mm, "end": v(74.47, 42.4) * mm});
            skLineSegment(sketch, "E335", {"start": v(58.88, 45.9) * mm, "end": v(58.88, 42.4) * mm});
            skLineSegment(sketch, "E336", {"start": v(93.53, 45.9) * mm, "end": v(93.53, 42.4) * mm});
            skLineSegment(sketch, "E337", {"start": v(77.93, 45.9) * mm, "end": v(77.93, 42.4) * mm});
            skLineSegment(sketch, "E338", {"start": v(-130.31, 26.85) * mm, "end": v(-130.31, 23.35) * mm});
            skLineSegment(sketch, "E339", {"start": v(-145.91, 26.85) * mm, "end": v(-145.91, 23.35) * mm});
            skLineSegment(sketch, "E340", {"start": v(135.07, 45.9) * mm, "end": v(135.07, 42.4) * mm});
            skLineSegment(sketch, "E341", {"start": v(150.68, 45.9) * mm, "end": v(150.68, 42.4) * mm});
            skLineSegment(sketch, "E342", {"start": v(-87.45, 26.85) * mm, "end": v(-87.45, 23.35) * mm});
            skLineSegment(sketch, "E343", {"start": v(-103.05, 26.85) * mm, "end": v(-103.05, 23.35) * mm});
            skLineSegment(sketch, "E344", {"start": v(-122.1, 26.85) * mm, "end": v(-122.1, 23.35) * mm});
            skLineSegment(sketch, "E345", {"start": v(-106.5, 26.85) * mm, "end": v(-106.5, 23.35) * mm});
            skLineSegment(sketch, "E346", {"start": v(-68.4, 26.85) * mm, "end": v(-68.4, 23.35) * mm});
            skLineSegment(sketch, "E347", {"start": v(-84, 26.85) * mm, "end": v(-84, 23.35) * mm});
            skLineSegment(sketch, "E348", {"start": v(-30.3, 26.85) * mm, "end": v(-30.3, 23.35) * mm});
            skLineSegment(sketch, "E349", {"start": v(-45.9, 26.85) * mm, "end": v(-45.9, 23.35) * mm});
            skLineSegment(sketch, "E350", {"start": v(-49.35, 26.85) * mm, "end": v(-49.35, 23.35) * mm});
            skLineSegment(sketch, "E351", {"start": v(-64.95, 26.85) * mm, "end": v(-64.95, 23.35) * mm});
            skLineSegment(sketch, "E352", {"start": v(-11.25, 26.85) * mm, "end": v(-11.25, 23.35) * mm});
            skLineSegment(sketch, "E353", {"start": v(-26.85, 26.85) * mm, "end": v(-26.85, 23.35) * mm});
            skLineSegment(sketch, "E354", {"start": v(-150.68, 45.9) * mm, "end": v(-150.68, 42.4) * mm});
            skLineSegment(sketch, "E355", {"start": v(-135.07, 45.9) * mm, "end": v(-135.07, 42.4) * mm});
            skLineSegment(sketch, "E356", {"start": v(-96.97, 45.9) * mm, "end": v(-96.97, 42.4) * mm});
            skLineSegment(sketch, "E357", {"start": v(-112.58, 45.9) * mm, "end": v(-112.58, 42.4) * mm});
            skLineSegment(sketch, "E358", {"start": v(-116.03, 45.9) * mm, "end": v(-116.03, 42.4) * mm});
            skLineSegment(sketch, "E359", {"start": v(-131.62, 45.9) * mm, "end": v(-131.62, 42.4) * mm});
            skLineSegment(sketch, "E360", {"start": v(-77.92, 45.9) * mm, "end": v(-77.92, 42.4) * mm});
            skLineSegment(sketch, "E361", {"start": v(-93.53, 45.9) * mm, "end": v(-93.53, 42.4) * mm});
            skLineSegment(sketch, "E362", {"start": v(-39.83, 45.9) * mm, "end": v(-39.83, 42.4) * mm});
            skLineSegment(sketch, "E363", {"start": v(-55.42, 45.9) * mm, "end": v(-55.42, 42.4) * mm});
            skLineSegment(sketch, "E364", {"start": v(-58.88, 45.9) * mm, "end": v(-58.88, 42.4) * mm});
            skLineSegment(sketch, "E365", {"start": v(-74.47, 45.9) * mm, "end": v(-74.47, 42.4) * mm});
            skLineSegment(sketch, "E366", {"start": v(-20.78, 45.9) * mm, "end": v(-20.78, 42.4) * mm});
            skLineSegment(sketch, "E367", {"start": v(-36.38, 45.9) * mm, "end": v(-36.38, 42.4) * mm});
            skLineSegment(sketch, "E368", {"start": v(17.32, 45.9) * mm, "end": v(17.32, 42.4) * mm});
            skLineSegment(sketch, "E369", {"start": v(1.72, 45.9) * mm, "end": v(1.72, 42.4) * mm});
            skLineSegment(sketch, "E370", {"start": v(-1.72, 45.9) * mm, "end": v(-1.72, 42.4) * mm});
            skLineSegment(sketch, "E371", {"start": v(-17.32, 45.9) * mm, "end": v(-17.32, 42.4) * mm});
            skLineSegment(sketch, "E372", {"start": v(55.43, 45.9) * mm, "end": v(55.43, 42.4) * mm});
            skLineSegment(sketch, "E373", {"start": v(39.82, 45.9) * mm, "end": v(39.82, 42.4) * mm});
            skLineSegment(sketch, "E374", {"start": v(36.38, 45.9) * mm, "end": v(36.38, 42.4) * mm});
            skLineSegment(sketch, "E375", {"start": v(20.78, 45.9) * mm, "end": v(20.78, 42.4) * mm});
            skLineSegment(sketch, "E376", {"start": v(131.62, -30.3) * mm, "end": v(131.62, -33.8) * mm});
            skLineSegment(sketch, "E377", {"start": v(116.02, -30.3) * mm, "end": v(116.02, -33.8) * mm});
            skLineSegment(sketch, "E378", {"start": v(93.53, -30.3) * mm, "end": v(93.53, -33.8) * mm});
            skLineSegment(sketch, "E379", {"start": v(112.57, -30.3) * mm, "end": v(112.57, -33.8) * mm});
            skLineSegment(sketch, "E380", {"start": v(96.97, -30.3) * mm, "end": v(96.97, -33.8) * mm});
            skLineSegment(sketch, "E381", {"start": v(39.82, -30.3) * mm, "end": v(39.82, -33.8) * mm});
            skLineSegment(sketch, "E382", {"start": v(3.04, -11.25) * mm, "end": v(3.04, -14.75) * mm});
            skLineSegment(sketch, "E383", {"start": v(-12.56, -11.25) * mm, "end": v(-12.56, -14.75) * mm});
            skLineSegment(sketch, "E384", {"start": v(41.14, -11.25) * mm, "end": v(41.14, -14.75) * mm});
            skLineSegment(sketch, "E385", {"start": v(25.54, -11.25) * mm, "end": v(25.54, -14.75) * mm});
            skLineSegment(sketch, "E386", {"start": v(22.09, -11.25) * mm, "end": v(22.09, -14.75) * mm});
            skLineSegment(sketch, "E387", {"start": v(6.49, -11.25) * mm, "end": v(6.49, -14.75) * mm});
            skLineSegment(sketch, "E388", {"start": v(79.24, -11.25) * mm, "end": v(79.24, -14.75) * mm});
            skLineSegment(sketch, "E389", {"start": v(63.64, -11.25) * mm, "end": v(63.64, -14.75) * mm});
            skLineSegment(sketch, "E390", {"start": v(60.19, -11.25) * mm, "end": v(60.19, -14.75) * mm});
            skLineSegment(sketch, "E391", {"start": v(44.59, -11.25) * mm, "end": v(44.59, -14.75) * mm});
            skLineSegment(sketch, "E392", {"start": v(89.83, -11.25) * mm, "end": v(89.83, -14.75) * mm});
            skLineSegment(sketch, "E393", {"start": v(105.43, -11.25) * mm, "end": v(105.43, -14.75) * mm});
            skLineSegment(sketch, "E394", {"start": v(150.68, -11.25) * mm, "end": v(150.68, -14.75) * mm});
            skLineSegment(sketch, "E395", {"start": v(135.07, -11.25) * mm, "end": v(135.07, -14.75) * mm});
            skLineSegment(sketch, "E396", {"start": v(116.02, -11.25) * mm, "end": v(116.02, -14.75) * mm});
            skLineSegment(sketch, "E397", {"start": v(131.62, -11.25) * mm, "end": v(131.62, -14.75) * mm});
            skLineSegment(sketch, "E398", {"start": v(-132.7, -30.3) * mm, "end": v(-132.7, -33.8) * mm});
            skLineSegment(sketch, "E399", {"start": v(-148.3, -30.3) * mm, "end": v(-148.3, -33.8) * mm});
            skLineSegment(sketch, "E400", {"start": v(-100.67, -30.3) * mm, "end": v(-100.67, -33.8) * mm});
            skLineSegment(sketch, "E401", {"start": v(-85.07, -30.3) * mm, "end": v(-85.07, -33.8) * mm});
            skLineSegment(sketch, "E402", {"start": v(-124.48, -30.3) * mm, "end": v(-124.48, -33.8) * mm});
            skLineSegment(sketch, "E403", {"start": v(-108.88, -30.3) * mm, "end": v(-108.88, -33.8) * mm});
            skLineSegment(sketch, "E404", {"start": v(135.07, -30.3) * mm, "end": v(135.07, -33.8) * mm});
            skLineSegment(sketch, "E405", {"start": v(150.68, -30.3) * mm, "end": v(150.68, -33.8) * mm});
            skLineSegment(sketch, "E406", {"start": v(31.61, 7.8) * mm, "end": v(31.61, 4.3) * mm});
            skLineSegment(sketch, "E407", {"start": v(16.01, 7.8) * mm, "end": v(16.01, 4.3) * mm});
            skLineSegment(sketch, "E408", {"start": v(12.56, 7.8) * mm, "end": v(12.56, 4.3) * mm});
            skLineSegment(sketch, "E409", {"start": v(-3.04, 7.8) * mm, "end": v(-3.04, 4.3) * mm});
            skLineSegment(sketch, "E410", {"start": v(50.66, 7.8) * mm, "end": v(50.66, 4.3) * mm});
            skLineSegment(sketch, "E411", {"start": v(35.06, 7.8) * mm, "end": v(35.06, 4.3) * mm});
            skLineSegment(sketch, "E412", {"start": v(88.76, 7.8) * mm, "end": v(88.76, 4.3) * mm});
            skLineSegment(sketch, "E413", {"start": v(73.16, 7.8) * mm, "end": v(73.16, 4.3) * mm});
            skLineSegment(sketch, "E414", {"start": v(69.71, 7.8) * mm, "end": v(69.71, 4.3) * mm});
            skLineSegment(sketch, "E415", {"start": v(54.11, 7.8) * mm, "end": v(54.11, 4.3) * mm});
            skLineSegment(sketch, "E416", {"start": v(135.07, 7.8) * mm, "end": v(135.07, 4.3) * mm});
            skLineSegment(sketch, "E417", {"start": v(150.68, 7.8) * mm, "end": v(150.68, 4.3) * mm});
            skLineSegment(sketch, "E418", {"start": v(-73.16, -11.25) * mm, "end": v(-73.16, -14.75) * mm});
            skLineSegment(sketch, "E419", {"start": v(-88.76, -11.25) * mm, "end": v(-88.76, -14.75) * mm});
            skLineSegment(sketch, "E420", {"start": v(-107.81, -11.25) * mm, "end": v(-107.81, -14.75) * mm});
            skLineSegment(sketch, "E421", {"start": v(-92.21, -11.25) * mm, "end": v(-92.21, -14.75) * mm});
            skLineSegment(sketch, "E422", {"start": v(-54.11, -11.25) * mm, "end": v(-54.11, -14.75) * mm});
            skLineSegment(sketch, "E423", {"start": v(-69.71, -11.25) * mm, "end": v(-69.71, -14.75) * mm});
            skLineSegment(sketch, "E424", {"start": v(-16.01, -11.25) * mm, "end": v(-16.01, -14.75) * mm});
            skLineSegment(sketch, "E425", {"start": v(-31.61, -11.25) * mm, "end": v(-31.61, -14.75) * mm});
            skLineSegment(sketch, "E426", {"start": v(-35.06, -11.25) * mm, "end": v(-35.06, -14.75) * mm});
            skLineSegment(sketch, "E427", {"start": v(-50.66, -11.25) * mm, "end": v(-50.66, -14.75) * mm});
            skLineSegment(sketch, "E428", {"start": v(111.26, 26.85) * mm, "end": v(111.26, 23.35) * mm});
            skLineSegment(sketch, "E429", {"start": v(126.86, 26.85) * mm, "end": v(126.86, 23.35) * mm});
            skLineSegment(sketch, "E430", {"start": v(-127.93, 7.8) * mm, "end": v(-127.93, 4.3) * mm});
            skLineSegment(sketch, "E431", {"start": v(-143.53, 7.8) * mm, "end": v(-143.53, 4.3) * mm});
            skLineSegment(sketch, "E432", {"start": v(150.68, 26.85) * mm, "end": v(150.68, 23.35) * mm});
            skLineSegment(sketch, "E433", {"start": v(135.07, 26.85) * mm, "end": v(135.07, 23.35) * mm});
            skLineSegment(sketch, "E434", {"start": v(-117.34, 4.3) * mm, "end": v(-116.54, 4.3) * mm});
            skLineSegment(sketch, "E435", {"start": v(-101.74, 4.3) * mm, "end": v(-102.54, 4.3) * mm});
            skLineSegment(sketch, "E436", {"start": v(-127.93, 4.3) * mm, "end": v(-128.73, 4.3) * mm});
            skLineSegment(sketch, "E437", {"start": v(-143.53, 4.3) * mm, "end": v(-142.73, 4.3) * mm});
            skLineSegment(sketch, "E438", {"start": v(-63.64, 4.3) * mm, "end": v(-64.44, 4.3) * mm});
            skLineSegment(sketch, "E439", {"start": v(-79.24, 4.3) * mm, "end": v(-78.44, 4.3) * mm});
            skLineSegment(sketch, "E440", {"start": v(-82.69, 4.3) * mm, "end": v(-83.49, 4.3) * mm});
            skLineSegment(sketch, "E441", {"start": v(-98.29, 4.3) * mm, "end": v(-97.49, 4.3) * mm});
            skLineSegment(sketch, "E442", {"start": v(-44.59, 4.3) * mm, "end": v(-45.39, 4.3) * mm});
            skLineSegment(sketch, "E443", {"start": v(-60.19, 4.3) * mm, "end": v(-59.39, 4.3) * mm});
            skLineSegment(sketch, "E444", {"start": v(-6.49, 4.3) * mm, "end": v(-7.29, 4.3) * mm});
            skLineSegment(sketch, "E445", {"start": v(-22.09, 4.3) * mm, "end": v(-21.29, 4.3) * mm});
            skLineSegment(sketch, "E446", {"start": v(-25.54, 4.3) * mm, "end": v(-26.34, 4.3) * mm});
            skLineSegment(sketch, "E447", {"start": v(-41.14, 4.3) * mm, "end": v(-40.34, 4.3) * mm});
            skLineSegment(sketch, "E448", {"start": v(26.85, 23.35) * mm, "end": v(26.05, 23.35) * mm});
            skLineSegment(sketch, "E449", {"start": v(11.25, 23.35) * mm, "end": v(12.05, 23.35) * mm});
            skLineSegment(sketch, "E450", {"start": v(7.8, 23.35) * mm, "end": v(7, 23.35) * mm});
            skLineSegment(sketch, "E451", {"start": v(-7.8, 23.35) * mm, "end": v(-7, 23.35) * mm});
            skLineSegment(sketch, "E452", {"start": v(45.9, 23.35) * mm, "end": v(45.1, 23.35) * mm});
            skLineSegment(sketch, "E453", {"start": v(30.3, 23.35) * mm, "end": v(31.1, 23.35) * mm});
            skLineSegment(sketch, "E454", {"start": v(84, 23.35) * mm, "end": v(83.2, 23.35) * mm});
            skLineSegment(sketch, "E455", {"start": v(68.4, 23.35) * mm, "end": v(69.2, 23.35) * mm});
            skLineSegment(sketch, "E456", {"start": v(64.95, 23.35) * mm, "end": v(64.15, 23.35) * mm});
            skLineSegment(sketch, "E457", {"start": v(49.35, 23.35) * mm, "end": v(50.15, 23.35) * mm});
            skLineSegment(sketch, "E458", {"start": v(103.05, 23.35) * mm, "end": v(102.25, 23.35) * mm});
            skLineSegment(sketch, "E459", {"start": v(87.45, 23.35) * mm, "end": v(88.25, 23.35) * mm});
            skLineSegment(sketch, "E460", {"start": v(74.47, 42.4) * mm, "end": v(73.68, 42.4) * mm});
            skLineSegment(sketch, "E461", {"start": v(58.88, 42.4) * mm, "end": v(59.68, 42.4) * mm});
            skLineSegment(sketch, "E462", {"start": v(93.53, 42.4) * mm, "end": v(92.73, 42.4) * mm});
            skLineSegment(sketch, "E463", {"start": v(77.93, 42.4) * mm, "end": v(78.72, 42.4) * mm});
            skLineSegment(sketch, "E464", {"start": v(-130.31, 23.35) * mm, "end": v(-131.11, 23.35) * mm});
            skLineSegment(sketch, "E465", {"start": v(-145.91, 23.35) * mm, "end": v(-145.11, 23.35) * mm});
            skLineSegment(sketch, "E466", {"start": v(150.68, 42.4) * mm, "end": v(149.88, 42.4) * mm});
            skLineSegment(sketch, "E467", {"start": v(135.07, 42.4) * mm, "end": v(135.88, 42.4) * mm});
            skLineSegment(sketch, "E468", {"start": v(-122.1, 23.35) * mm, "end": v(-121.3, 23.35) * mm});
            skLineSegment(sketch, "E469", {"start": v(-106.5, 23.35) * mm, "end": v(-107.3, 23.35) * mm});
            skLineSegment(sketch, "E470", {"start": v(-68.4, 23.35) * mm, "end": v(-69.2, 23.35) * mm});
            skLineSegment(sketch, "E471", {"start": v(-84, 23.35) * mm, "end": v(-83.2, 23.35) * mm});
            skLineSegment(sketch, "E472", {"start": v(-87.45, 23.35) * mm, "end": v(-88.25, 23.35) * mm});
            skLineSegment(sketch, "E473", {"start": v(-103.05, 23.35) * mm, "end": v(-102.25, 23.35) * mm});
            skLineSegment(sketch, "E474", {"start": v(-30.3, 23.35) * mm, "end": v(-31.1, 23.35) * mm});
            skLineSegment(sketch, "E475", {"start": v(-45.9, 23.35) * mm, "end": v(-45.1, 23.35) * mm});
            skLineSegment(sketch, "E476", {"start": v(-49.35, 23.35) * mm, "end": v(-50.15, 23.35) * mm});
            skLineSegment(sketch, "E477", {"start": v(-64.95, 23.35) * mm, "end": v(-64.15, 23.35) * mm});
            skLineSegment(sketch, "E478", {"start": v(-11.25, 23.35) * mm, "end": v(-12.05, 23.35) * mm});
            skLineSegment(sketch, "E479", {"start": v(-26.85, 23.35) * mm, "end": v(-26.05, 23.35) * mm});
            skLineSegment(sketch, "E480", {"start": v(-150.68, 42.4) * mm, "end": v(-149.88, 42.4) * mm});
            skLineSegment(sketch, "E481", {"start": v(-135.07, 42.4) * mm, "end": v(-135.88, 42.4) * mm});
            skLineSegment(sketch, "E482", {"start": v(-96.97, 42.4) * mm, "end": v(-97.78, 42.4) * mm});
            skLineSegment(sketch, "E483", {"start": v(-112.58, 42.4) * mm, "end": v(-111.78, 42.4) * mm});
            skLineSegment(sketch, "E484", {"start": v(-116.03, 42.4) * mm, "end": v(-116.83, 42.4) * mm});
            skLineSegment(sketch, "E485", {"start": v(-131.62, 42.4) * mm, "end": v(-130.82, 42.4) * mm});
            skLineSegment(sketch, "E486", {"start": v(-77.92, 42.4) * mm, "end": v(-78.72, 42.4) * mm});
            skLineSegment(sketch, "E487", {"start": v(-93.53, 42.4) * mm, "end": v(-92.73, 42.4) * mm});
            skLineSegment(sketch, "E488", {"start": v(-39.83, 42.4) * mm, "end": v(-40.62, 42.4) * mm});
            skLineSegment(sketch, "E489", {"start": v(-55.42, 42.4) * mm, "end": v(-54.62, 42.4) * mm});
            skLineSegment(sketch, "E490", {"start": v(-58.88, 42.4) * mm, "end": v(-59.67, 42.4) * mm});
            skLineSegment(sketch, "E491", {"start": v(-74.47, 42.4) * mm, "end": v(-73.68, 42.4) * mm});
            skLineSegment(sketch, "E492", {"start": v(-20.78, 42.4) * mm, "end": v(-21.57, 42.4) * mm});
            skLineSegment(sketch, "E493", {"start": v(-36.38, 42.4) * mm, "end": v(-35.58, 42.4) * mm});
            skLineSegment(sketch, "E494", {"start": v(17.32, 42.4) * mm, "end": v(16.53, 42.4) * mm});
            skLineSegment(sketch, "E495", {"start": v(1.72, 42.4) * mm, "end": v(2.53, 42.4) * mm});
            skLineSegment(sketch, "E496", {"start": v(-1.72, 42.4) * mm, "end": v(-2.53, 42.4) * mm});
            skLineSegment(sketch, "E497", {"start": v(-17.32, 42.4) * mm, "end": v(-16.53, 42.4) * mm});
            skLineSegment(sketch, "E498", {"start": v(55.43, 42.4) * mm, "end": v(54.62, 42.4) * mm});
            skLineSegment(sketch, "E499", {"start": v(39.82, 42.4) * mm, "end": v(40.62, 42.4) * mm});
            skLineSegment(sketch, "E500", {"start": v(36.38, 42.4) * mm, "end": v(35.57, 42.4) * mm});
            skLineSegment(sketch, "E501", {"start": v(20.78, 42.4) * mm, "end": v(21.57, 42.4) * mm});
            skLineSegment(sketch, "E502", {"start": v(131.62, -33.8) * mm, "end": v(130.82, -33.8) * mm});
            skLineSegment(sketch, "E503", {"start": v(116.02, -33.8) * mm, "end": v(116.82, -33.8) * mm});
            skLineSegment(sketch, "E504", {"start": v(135.07, -33.8) * mm, "end": v(135.88, -33.8) * mm});
            skLineSegment(sketch, "E505", {"start": v(150.68, -33.8) * mm, "end": v(149.88, -33.8) * mm});
            skLineSegment(sketch, "E506", {"start": v(93.53, -33.8) * mm, "end": v(92.73, -33.8) * mm});
            skLineSegment(sketch, "E507", {"start": v(112.57, -33.8) * mm, "end": v(111.77, -33.8) * mm});
            skLineSegment(sketch, "E508", {"start": v(96.97, -33.8) * mm, "end": v(97.78, -33.8) * mm});
            skLineSegment(sketch, "E509", {"start": v(39.82, -33.8) * mm, "end": v(40.62, -33.8) * mm});
            skLineSegment(sketch, "E510", {"start": v(3.04, -14.75) * mm, "end": v(2.24, -14.75) * mm});
            skLineSegment(sketch, "E511", {"start": v(-12.56, -14.75) * mm, "end": v(-11.76, -14.75) * mm});
            skLineSegment(sketch, "E512", {"start": v(41.14, -14.75) * mm, "end": v(40.34, -14.75) * mm});
            skLineSegment(sketch, "E513", {"start": v(25.54, -14.75) * mm, "end": v(26.34, -14.75) * mm});
            skLineSegment(sketch, "E514", {"start": v(22.09, -14.75) * mm, "end": v(21.29, -14.75) * mm});
            skLineSegment(sketch, "E515", {"start": v(6.49, -14.75) * mm, "end": v(7.29, -14.75) * mm});
            skLineSegment(sketch, "E516", {"start": v(60.19, -14.75) * mm, "end": v(59.39, -14.75) * mm});
            skLineSegment(sketch, "E517", {"start": v(44.59, -14.75) * mm, "end": v(45.39, -14.75) * mm});
            skLineSegment(sketch, "E518", {"start": v(89.83, -14.75) * mm, "end": v(90.63, -14.75) * mm});
            skLineSegment(sketch, "E519", {"start": v(105.43, -14.75) * mm, "end": v(104.63, -14.75) * mm});
            skLineSegment(sketch, "E520", {"start": v(79.24, -14.75) * mm, "end": v(78.44, -14.75) * mm});
            skLineSegment(sketch, "E521", {"start": v(63.64, -14.75) * mm, "end": v(64.44, -14.75) * mm});
            skLineSegment(sketch, "E522", {"start": v(150.68, -14.75) * mm, "end": v(149.88, -14.75) * mm});
            skLineSegment(sketch, "E523", {"start": v(135.07, -14.75) * mm, "end": v(135.88, -14.75) * mm});
            skLineSegment(sketch, "E524", {"start": v(116.02, -14.75) * mm, "end": v(116.82, -14.75) * mm});
            skLineSegment(sketch, "E525", {"start": v(131.62, -14.75) * mm, "end": v(130.82, -14.75) * mm});
            skLineSegment(sketch, "E526", {"start": v(-132.7, -33.8) * mm, "end": v(-133.5, -33.8) * mm});
            skLineSegment(sketch, "E527", {"start": v(-148.3, -33.8) * mm, "end": v(-147.5, -33.8) * mm});
            skLineSegment(sketch, "E528", {"start": v(-100.67, -33.8) * mm, "end": v(-99.87, -33.8) * mm});
            skLineSegment(sketch, "E529", {"start": v(-85.07, -33.8) * mm, "end": v(-85.87, -33.8) * mm});
            skLineSegment(sketch, "E530", {"start": v(-124.48, -33.8) * mm, "end": v(-123.68, -33.8) * mm});
            skLineSegment(sketch, "E531", {"start": v(-108.88, -33.8) * mm, "end": v(-109.68, -33.8) * mm});
            skLineSegment(sketch, "E532", {"start": v(12.56, 4.3) * mm, "end": v(11.76, 4.3) * mm});
            skLineSegment(sketch, "E533", {"start": v(-3.04, 4.3) * mm, "end": v(-2.24, 4.3) * mm});
            skLineSegment(sketch, "E534", {"start": v(50.66, 4.3) * mm, "end": v(49.86, 4.3) * mm});
            skLineSegment(sketch, "E535", {"start": v(35.06, 4.3) * mm, "end": v(35.86, 4.3) * mm});
            skLineSegment(sketch, "E536", {"start": v(31.61, 4.3) * mm, "end": v(30.81, 4.3) * mm});
            skLineSegment(sketch, "E537", {"start": v(16.01, 4.3) * mm, "end": v(16.81, 4.3) * mm});
            skLineSegment(sketch, "E538", {"start": v(88.76, 4.3) * mm, "end": v(87.96, 4.3) * mm});
            skLineSegment(sketch, "E539", {"start": v(73.16, 4.3) * mm, "end": v(73.96, 4.3) * mm});
            skLineSegment(sketch, "E540", {"start": v(69.71, 4.3) * mm, "end": v(68.91, 4.3) * mm});
            skLineSegment(sketch, "E541", {"start": v(54.11, 4.3) * mm, "end": v(54.91, 4.3) * mm});
            skLineSegment(sketch, "E542", {"start": v(135.07, 4.3) * mm, "end": v(135.88, 4.3) * mm});
            skLineSegment(sketch, "E543", {"start": v(150.68, 4.3) * mm, "end": v(149.88, 4.3) * mm});
            skLineSegment(sketch, "E544", {"start": v(-107.81, -14.75) * mm, "end": v(-107.01, -14.75) * mm});
            skLineSegment(sketch, "E545", {"start": v(-92.21, -14.75) * mm, "end": v(-93.01, -14.75) * mm});
            skLineSegment(sketch, "E546", {"start": v(-54.11, -14.75) * mm, "end": v(-54.91, -14.75) * mm});
            skLineSegment(sketch, "E547", {"start": v(-69.71, -14.75) * mm, "end": v(-68.91, -14.75) * mm});
            skLineSegment(sketch, "E548", {"start": v(-73.16, -14.75) * mm, "end": v(-73.96, -14.75) * mm});
            skLineSegment(sketch, "E549", {"start": v(-88.76, -14.75) * mm, "end": v(-87.96, -14.75) * mm});
            skLineSegment(sketch, "E550", {"start": v(-16.01, -14.75) * mm, "end": v(-16.81, -14.75) * mm});
            skLineSegment(sketch, "E551", {"start": v(-31.61, -14.75) * mm, "end": v(-30.81, -14.75) * mm});
            skLineSegment(sketch, "E552", {"start": v(-35.06, -14.75) * mm, "end": v(-35.86, -14.75) * mm});
            skLineSegment(sketch, "E553", {"start": v(-50.66, -14.75) * mm, "end": v(-49.86, -14.75) * mm});
            skLineSegment(sketch, "E554", {"start": v(111.26, 23.35) * mm, "end": v(112.06, 23.35) * mm});
            skLineSegment(sketch, "E555", {"start": v(126.86, 23.35) * mm, "end": v(126.06, 23.35) * mm});
            skLineSegment(sketch, "E556", {"start": v(135.07, 23.35) * mm, "end": v(135.88, 23.35) * mm});
            skLineSegment(sketch, "E557", {"start": v(150.68, 23.35) * mm, "end": v(149.88, 23.35) * mm});
            skLineSegment(sketch, "E558", {"start": v(-116.54, 4.3) * mm, "end": v(-116.54, -0.7) * mm});
            skLineSegment(sketch, "E559", {"start": v(-102.54, 4.3) * mm, "end": v(-102.54, -0.7) * mm});
            skLineSegment(sketch, "E560", {"start": v(-128.73, 4.3) * mm, "end": v(-128.73, -0.7) * mm});
            skLineSegment(sketch, "E561", {"start": v(-142.73, 4.3) * mm, "end": v(-142.73, -0.7) * mm});
            skLineSegment(sketch, "E562", {"start": v(-64.44, 4.3) * mm, "end": v(-64.44, -0.7) * mm});
            skLineSegment(sketch, "E563", {"start": v(-78.44, 4.3) * mm, "end": v(-78.44, -0.7) * mm});
            skLineSegment(sketch, "E564", {"start": v(-83.49, 4.3) * mm, "end": v(-83.49, -0.7) * mm});
            skLineSegment(sketch, "E565", {"start": v(-97.49, 4.3) * mm, "end": v(-97.49, -0.7) * mm});
            skLineSegment(sketch, "E566", {"start": v(-45.39, 4.3) * mm, "end": v(-45.39, -0.7) * mm});
            skLineSegment(sketch, "E567", {"start": v(-59.39, 4.3) * mm, "end": v(-59.39, -0.7) * mm});
            skLineSegment(sketch, "E568", {"start": v(-7.29, 4.3) * mm, "end": v(-7.29, -0.7) * mm});
            skLineSegment(sketch, "E569", {"start": v(-21.29, 4.3) * mm, "end": v(-21.29, -0.7) * mm});
            skLineSegment(sketch, "E570", {"start": v(-26.34, 4.3) * mm, "end": v(-26.34, -0.7) * mm});
            skLineSegment(sketch, "E571", {"start": v(-40.34, 4.3) * mm, "end": v(-40.34, -0.7) * mm});
            skLineSegment(sketch, "E572", {"start": v(26.05, 23.35) * mm, "end": v(26.05, 18.35) * mm});
            skLineSegment(sketch, "E573", {"start": v(12.05, 23.35) * mm, "end": v(12.05, 18.35) * mm});
            skLineSegment(sketch, "E574", {"start": v(7, 23.35) * mm, "end": v(7, 18.35) * mm});
            skLineSegment(sketch, "E575", {"start": v(-7, 23.35) * mm, "end": v(-7, 18.35) * mm});
            skLineSegment(sketch, "E576", {"start": v(45.1, 23.35) * mm, "end": v(45.1, 18.35) * mm});
            skLineSegment(sketch, "E577", {"start": v(31.1, 23.35) * mm, "end": v(31.1, 18.35) * mm});
            skLineSegment(sketch, "E578", {"start": v(83.2, 23.35) * mm, "end": v(83.2, 18.35) * mm});
            skLineSegment(sketch, "E579", {"start": v(69.2, 23.35) * mm, "end": v(69.2, 18.35) * mm});
            skLineSegment(sketch, "E580", {"start": v(64.15, 23.35) * mm, "end": v(64.15, 18.35) * mm});
            skLineSegment(sketch, "E581", {"start": v(50.15, 23.35) * mm, "end": v(50.15, 18.35) * mm});
            skLineSegment(sketch, "E582", {"start": v(102.25, 23.35) * mm, "end": v(102.25, 18.35) * mm});
            skLineSegment(sketch, "E583", {"start": v(88.25, 23.35) * mm, "end": v(88.25, 18.35) * mm});
            skLineSegment(sketch, "E584", {"start": v(73.68, 42.4) * mm, "end": v(73.68, 37.4) * mm});
            skLineSegment(sketch, "E585", {"start": v(59.68, 42.4) * mm, "end": v(59.68, 37.4) * mm});
            skLineSegment(sketch, "E586", {"start": v(54.62, 42.4) * mm, "end": v(54.62, 37.4) * mm});
            skLineSegment(sketch, "E587", {"start": v(40.62, 42.4) * mm, "end": v(40.62, 37.4) * mm});
            skLineSegment(sketch, "E588", {"start": v(92.73, 42.4) * mm, "end": v(92.73, 37.4) * mm});
            skLineSegment(sketch, "E589", {"start": v(78.72, 42.4) * mm, "end": v(78.72, 37.4) * mm});
            skLineSegment(sketch, "E590", {"start": v(-131.11, 23.35) * mm, "end": v(-131.11, 18.35) * mm});
            skLineSegment(sketch, "E591", {"start": v(-145.11, 23.35) * mm, "end": v(-145.11, 18.35) * mm});
            skLineSegment(sketch, "E592", {"start": v(135.88, 42.4) * mm, "end": v(135.88, 37.4) * mm});
            skLineSegment(sketch, "E593", {"start": v(149.88, 42.4) * mm, "end": v(149.88, 37.4) * mm});
            skLineSegment(sketch, "E594", {"start": v(-121.3, 23.35) * mm, "end": v(-121.3, 18.35) * mm});
            skLineSegment(sketch, "E595", {"start": v(-107.3, 23.35) * mm, "end": v(-107.3, 18.35) * mm});
            skLineSegment(sketch, "E596", {"start": v(-69.2, 23.35) * mm, "end": v(-69.2, 18.35) * mm});
            skLineSegment(sketch, "E597", {"start": v(-83.2, 23.35) * mm, "end": v(-83.2, 18.35) * mm});
            skLineSegment(sketch, "E598", {"start": v(-88.25, 23.35) * mm, "end": v(-88.25, 18.35) * mm});
            skLineSegment(sketch, "E599", {"start": v(-102.25, 23.35) * mm, "end": v(-102.25, 18.35) * mm});
            skLineSegment(sketch, "E600", {"start": v(-31.1, 23.35) * mm, "end": v(-31.1, 18.35) * mm});
            skLineSegment(sketch, "E601", {"start": v(-45.1, 23.35) * mm, "end": v(-45.1, 18.35) * mm});
            skLineSegment(sketch, "E602", {"start": v(-50.15, 23.35) * mm, "end": v(-50.15, 18.35) * mm});
            skLineSegment(sketch, "E603", {"start": v(-64.15, 23.35) * mm, "end": v(-64.15, 18.35) * mm});
            skLineSegment(sketch, "E604", {"start": v(-12.05, 23.35) * mm, "end": v(-12.05, 18.35) * mm});
            skLineSegment(sketch, "E605", {"start": v(-26.05, 23.35) * mm, "end": v(-26.05, 18.35) * mm});
            skLineSegment(sketch, "E606", {"start": v(-135.88, 42.4) * mm, "end": v(-135.88, 37.4) * mm});
            skLineSegment(sketch, "E607", {"start": v(-116.83, 42.4) * mm, "end": v(-116.83, 37.4) * mm});
            skLineSegment(sketch, "E608", {"start": v(-130.82, 42.4) * mm, "end": v(-130.82, 37.4) * mm});
            skLineSegment(sketch, "E609", {"start": v(-149.88, 42.4) * mm, "end": v(-149.88, 37.4) * mm});
            skLineSegment(sketch, "E610", {"start": v(-78.72, 42.4) * mm, "end": v(-78.72, 37.4) * mm});
            skLineSegment(sketch, "E611", {"start": v(-92.73, 42.4) * mm, "end": v(-92.73, 37.4) * mm});
            skLineSegment(sketch, "E612", {"start": v(-97.78, 42.4) * mm, "end": v(-97.78, 37.4) * mm});
            skLineSegment(sketch, "E613", {"start": v(-111.78, 42.4) * mm, "end": v(-111.78, 37.4) * mm});
            skLineSegment(sketch, "E614", {"start": v(-40.62, 42.4) * mm, "end": v(-40.62, 37.4) * mm});
            skLineSegment(sketch, "E615", {"start": v(-54.62, 42.4) * mm, "end": v(-54.62, 37.4) * mm});
            skLineSegment(sketch, "E616", {"start": v(-59.67, 42.4) * mm, "end": v(-59.67, 37.4) * mm});
            skLineSegment(sketch, "E617", {"start": v(-73.68, 42.4) * mm, "end": v(-73.68, 37.4) * mm});
            skLineSegment(sketch, "E618", {"start": v(-21.57, 42.4) * mm, "end": v(-21.57, 37.4) * mm});
            skLineSegment(sketch, "E619", {"start": v(-35.58, 42.4) * mm, "end": v(-35.58, 37.4) * mm});
            skLineSegment(sketch, "E620", {"start": v(16.53, 42.4) * mm, "end": v(16.53, 37.4) * mm});
            skLineSegment(sketch, "E621", {"start": v(2.53, 42.4) * mm, "end": v(2.53, 37.4) * mm});
            skLineSegment(sketch, "E622", {"start": v(-2.53, 42.4) * mm, "end": v(-2.53, 37.4) * mm});
            skLineSegment(sketch, "E623", {"start": v(-16.53, 42.4) * mm, "end": v(-16.53, 37.4) * mm});
            skLineSegment(sketch, "E624", {"start": v(35.57, 42.4) * mm, "end": v(35.57, 37.4) * mm});
            skLineSegment(sketch, "E625", {"start": v(21.57, 42.4) * mm, "end": v(21.57, 37.4) * mm});
            skLineSegment(sketch, "E626", {"start": v(130.82, -33.8) * mm, "end": v(130.82, -38.8) * mm});
            skLineSegment(sketch, "E627", {"start": v(116.82, -33.8) * mm, "end": v(116.82, -38.8) * mm});
            skLineSegment(sketch, "E628", {"start": v(135.88, -33.8) * mm, "end": v(135.88, -38.8) * mm});
            skLineSegment(sketch, "E629", {"start": v(149.88, -33.8) * mm, "end": v(149.88, -38.8) * mm});
            skLineSegment(sketch, "E630", {"start": v(92.73, -33.8) * mm, "end": v(92.73, -38.8) * mm});
            skLineSegment(sketch, "E631", {"start": v(111.77, -33.8) * mm, "end": v(111.77, -38.8) * mm});
            skLineSegment(sketch, "E632", {"start": v(97.78, -33.8) * mm, "end": v(97.78, -38.8) * mm});
            skLineSegment(sketch, "E633", {"start": v(40.62, -33.8) * mm, "end": v(40.62, -38.8) * mm});
            skLineSegment(sketch, "E634", {"start": v(2.24, -14.75) * mm, "end": v(2.24, -19.75) * mm});
            skLineSegment(sketch, "E635", {"start": v(-11.76, -14.75) * mm, "end": v(-11.76, -19.75) * mm});
            skLineSegment(sketch, "E636", {"start": v(40.34, -14.75) * mm, "end": v(40.34, -19.75) * mm});
            skLineSegment(sketch, "E637", {"start": v(26.34, -14.75) * mm, "end": v(26.34, -19.75) * mm});
            skLineSegment(sketch, "E638", {"start": v(21.29, -14.75) * mm, "end": v(21.29, -19.75) * mm});
            skLineSegment(sketch, "E639", {"start": v(7.29, -14.75) * mm, "end": v(7.29, -19.75) * mm});
            skLineSegment(sketch, "E640", {"start": v(59.39, -14.75) * mm, "end": v(59.39, -19.75) * mm});
            skLineSegment(sketch, "E641", {"start": v(45.39, -14.75) * mm, "end": v(45.39, -19.75) * mm});
            skLineSegment(sketch, "E642", {"start": v(90.63, -14.75) * mm, "end": v(90.63, -19.75) * mm});
            skLineSegment(sketch, "E643", {"start": v(104.63, -14.75) * mm, "end": v(104.63, -19.75) * mm});
            skLineSegment(sketch, "E644", {"start": v(78.44, -14.75) * mm, "end": v(78.44, -19.75) * mm});
            skLineSegment(sketch, "E645", {"start": v(64.44, -14.75) * mm, "end": v(64.44, -19.75) * mm});
            skLineSegment(sketch, "E646", {"start": v(149.88, -14.75) * mm, "end": v(149.88, -19.75) * mm});
            skLineSegment(sketch, "E647", {"start": v(135.88, -14.75) * mm, "end": v(135.88, -19.75) * mm});
            skLineSegment(sketch, "E648", {"start": v(116.82, -14.75) * mm, "end": v(116.82, -19.75) * mm});
            skLineSegment(sketch, "E649", {"start": v(130.82, -14.75) * mm, "end": v(130.82, -19.75) * mm});
            skLineSegment(sketch, "E650", {"start": v(-133.5, -33.8) * mm, "end": v(-133.5, -38.8) * mm});
            skLineSegment(sketch, "E651", {"start": v(-147.5, -33.8) * mm, "end": v(-147.5, -38.8) * mm});
            skLineSegment(sketch, "E652", {"start": v(-99.87, -33.8) * mm, "end": v(-99.87, -38.8) * mm});
            skLineSegment(sketch, "E653", {"start": v(-85.87, -33.8) * mm, "end": v(-85.87, -38.8) * mm});
            skLineSegment(sketch, "E654", {"start": v(-123.68, -33.8) * mm, "end": v(-123.68, -38.8) * mm});
            skLineSegment(sketch, "E655", {"start": v(-109.68, -33.8) * mm, "end": v(-109.68, -38.8) * mm});
            skLineSegment(sketch, "E656", {"start": v(11.76, 4.3) * mm, "end": v(11.76, -0.7) * mm});
            skLineSegment(sketch, "E657", {"start": v(-2.24, 4.3) * mm, "end": v(-2.24, -0.7) * mm});
            skLineSegment(sketch, "E658", {"start": v(49.86, 4.3) * mm, "end": v(49.86, -0.7) * mm});
            skLineSegment(sketch, "E659", {"start": v(35.86, 4.3) * mm, "end": v(35.86, -0.7) * mm});
            skLineSegment(sketch, "E660", {"start": v(30.81, 4.3) * mm, "end": v(30.81, -0.7) * mm});
            skLineSegment(sketch, "E661", {"start": v(16.81, 4.3) * mm, "end": v(16.81, -0.7) * mm});
            skLineSegment(sketch, "E662", {"start": v(87.96, 4.3) * mm, "end": v(87.96, -0.7) * mm});
            skLineSegment(sketch, "E663", {"start": v(73.96, 4.3) * mm, "end": v(73.96, -0.7) * mm});
            skLineSegment(sketch, "E664", {"start": v(68.91, 4.3) * mm, "end": v(68.91, -0.7) * mm});
            skLineSegment(sketch, "E665", {"start": v(54.91, 4.3) * mm, "end": v(54.91, -0.7) * mm});
            skLineSegment(sketch, "E666", {"start": v(135.88, 4.3) * mm, "end": v(135.88, -0.7) * mm});
            skLineSegment(sketch, "E667", {"start": v(149.88, 4.3) * mm, "end": v(149.88, -0.7) * mm});
            skLineSegment(sketch, "E668", {"start": v(-107.01, -14.75) * mm, "end": v(-107.01, -19.75) * mm});
            skLineSegment(sketch, "E669", {"start": v(-93.01, -14.75) * mm, "end": v(-93.01, -19.75) * mm});
            skLineSegment(sketch, "E670", {"start": v(-54.91, -14.75) * mm, "end": v(-54.91, -19.75) * mm});
            skLineSegment(sketch, "E671", {"start": v(-68.91, -14.75) * mm, "end": v(-68.91, -19.75) * mm});
            skLineSegment(sketch, "E672", {"start": v(-73.96, -14.75) * mm, "end": v(-73.96, -19.75) * mm});
            skLineSegment(sketch, "E673", {"start": v(-87.96, -14.75) * mm, "end": v(-87.96, -19.75) * mm});
            skLineSegment(sketch, "E674", {"start": v(-16.81, -14.75) * mm, "end": v(-16.81, -19.75) * mm});
            skLineSegment(sketch, "E675", {"start": v(-30.81, -14.75) * mm, "end": v(-30.81, -19.75) * mm});
            skLineSegment(sketch, "E676", {"start": v(-35.86, -14.75) * mm, "end": v(-35.86, -19.75) * mm});
            skLineSegment(sketch, "E677", {"start": v(-49.86, -14.75) * mm, "end": v(-49.86, -19.75) * mm});
            skLineSegment(sketch, "E678", {"start": v(112.06, 23.35) * mm, "end": v(112.06, 18.35) * mm});
            skLineSegment(sketch, "E679", {"start": v(126.06, 23.35) * mm, "end": v(126.06, 18.35) * mm});
            skLineSegment(sketch, "E680", {"start": v(149.88, 23.35) * mm, "end": v(149.88, 18.35) * mm});
            skLineSegment(sketch, "E681", {"start": v(135.88, 23.35) * mm, "end": v(135.88, 18.35) * mm});
            skLineSegment(sketch, "E682", {"start": v(135.88, 18.35) * mm, "end": v(135.07, 18.35) * mm});
            skLineSegment(sketch, "E683", {"start": v(149.88, 18.35) * mm, "end": v(150.68, 18.35) * mm});
            skLineSegment(sketch, "E684", {"start": v(-116.54, -0.7) * mm, "end": v(-117.34, -0.7) * mm});
            skLineSegment(sketch, "E685", {"start": v(-102.54, -0.7) * mm, "end": v(-101.74, -0.7) * mm});
            skLineSegment(sketch, "E686", {"start": v(-128.73, -0.7) * mm, "end": v(-127.93, -0.7) * mm});
            skLineSegment(sketch, "E687", {"start": v(-142.73, -0.7) * mm, "end": v(-143.53, -0.7) * mm});
            skLineSegment(sketch, "E688", {"start": v(-83.49, -0.7) * mm, "end": v(-82.69, -0.7) * mm});
            skLineSegment(sketch, "E689", {"start": v(-97.49, -0.7) * mm, "end": v(-98.29, -0.7) * mm});
            skLineSegment(sketch, "E690", {"start": v(-45.39, -0.7) * mm, "end": v(-44.59, -0.7) * mm});
            skLineSegment(sketch, "E691", {"start": v(-59.39, -0.7) * mm, "end": v(-60.19, -0.7) * mm});
            skLineSegment(sketch, "E692", {"start": v(-64.44, -0.7) * mm, "end": v(-63.64, -0.7) * mm});
            skLineSegment(sketch, "E693", {"start": v(-78.44, -0.7) * mm, "end": v(-79.24, -0.7) * mm});
            skLineSegment(sketch, "E694", {"start": v(-7.29, -0.7) * mm, "end": v(-6.49, -0.7) * mm});
            skLineSegment(sketch, "E695", {"start": v(-21.29, -0.7) * mm, "end": v(-22.09, -0.7) * mm});
            skLineSegment(sketch, "E696", {"start": v(-26.34, -0.7) * mm, "end": v(-25.54, -0.7) * mm});
            skLineSegment(sketch, "E697", {"start": v(-40.34, -0.7) * mm, "end": v(-41.14, -0.7) * mm});
            skLineSegment(sketch, "E698", {"start": v(26.05, 18.35) * mm, "end": v(26.85, 18.35) * mm});
            skLineSegment(sketch, "E699", {"start": v(12.05, 18.35) * mm, "end": v(11.25, 18.35) * mm});
            skLineSegment(sketch, "E700", {"start": v(7, 18.35) * mm, "end": v(7.8, 18.35) * mm});
            skLineSegment(sketch, "E701", {"start": v(-7, 18.35) * mm, "end": v(-7.8, 18.35) * mm});
            skLineSegment(sketch, "E702", {"start": v(45.1, 18.35) * mm, "end": v(45.9, 18.35) * mm});
            skLineSegment(sketch, "E703", {"start": v(31.1, 18.35) * mm, "end": v(30.3, 18.35) * mm});
            skLineSegment(sketch, "E704", {"start": v(83.2, 18.35) * mm, "end": v(84, 18.35) * mm});
            skLineSegment(sketch, "E705", {"start": v(69.2, 18.35) * mm, "end": v(68.4, 18.35) * mm});
            skLineSegment(sketch, "E706", {"start": v(64.15, 18.35) * mm, "end": v(64.95, 18.35) * mm});
            skLineSegment(sketch, "E707", {"start": v(50.15, 18.35) * mm, "end": v(49.35, 18.35) * mm});
            skLineSegment(sketch, "E708", {"start": v(102.25, 18.35) * mm, "end": v(103.05, 18.35) * mm});
            skLineSegment(sketch, "E709", {"start": v(88.25, 18.35) * mm, "end": v(87.45, 18.35) * mm});
            skLineSegment(sketch, "E710", {"start": v(73.68, 37.4) * mm, "end": v(74.47, 37.4) * mm});
            skLineSegment(sketch, "E711", {"start": v(59.68, 37.4) * mm, "end": v(58.88, 37.4) * mm});
            skLineSegment(sketch, "E712", {"start": v(54.62, 37.4) * mm, "end": v(55.43, 37.4) * mm});
            skLineSegment(sketch, "E713", {"start": v(40.62, 37.4) * mm, "end": v(39.82, 37.4) * mm});
            skLineSegment(sketch, "E714", {"start": v(92.73, 37.4) * mm, "end": v(93.53, 37.4) * mm});
            skLineSegment(sketch, "E715", {"start": v(78.72, 37.4) * mm, "end": v(77.93, 37.4) * mm});
            skLineSegment(sketch, "E716", {"start": v(-131.11, 18.35) * mm, "end": v(-130.31, 18.35) * mm});
            skLineSegment(sketch, "E717", {"start": v(-145.11, 18.35) * mm, "end": v(-145.91, 18.35) * mm});
            skLineSegment(sketch, "E718", {"start": v(149.88, 37.4) * mm, "end": v(150.68, 37.4) * mm});
            skLineSegment(sketch, "E719", {"start": v(135.88, 37.4) * mm, "end": v(135.07, 37.4) * mm});
            skLineSegment(sketch, "E720", {"start": v(-121.3, 18.35) * mm, "end": v(-122.1, 18.35) * mm});
            skLineSegment(sketch, "E721", {"start": v(-107.3, 18.35) * mm, "end": v(-106.5, 18.35) * mm});
            skLineSegment(sketch, "E722", {"start": v(-69.2, 18.35) * mm, "end": v(-68.4, 18.35) * mm});
            skLineSegment(sketch, "E723", {"start": v(-83.2, 18.35) * mm, "end": v(-84, 18.35) * mm});
            skLineSegment(sketch, "E724", {"start": v(-88.25, 18.35) * mm, "end": v(-87.45, 18.35) * mm});
            skLineSegment(sketch, "E725", {"start": v(-102.25, 18.35) * mm, "end": v(-103.05, 18.35) * mm});
            skLineSegment(sketch, "E726", {"start": v(-50.15, 18.35) * mm, "end": v(-49.35, 18.35) * mm});
            skLineSegment(sketch, "E727", {"start": v(-64.15, 18.35) * mm, "end": v(-64.95, 18.35) * mm});
            skLineSegment(sketch, "E728", {"start": v(-12.05, 18.35) * mm, "end": v(-11.25, 18.35) * mm});
            skLineSegment(sketch, "E729", {"start": v(-26.05, 18.35) * mm, "end": v(-26.85, 18.35) * mm});
            skLineSegment(sketch, "E730", {"start": v(-31.1, 18.35) * mm, "end": v(-30.3, 18.35) * mm});
            skLineSegment(sketch, "E731", {"start": v(-45.1, 18.35) * mm, "end": v(-45.9, 18.35) * mm});
            skLineSegment(sketch, "E732", {"start": v(-135.88, 37.4) * mm, "end": v(-135.07, 37.4) * mm});
            skLineSegment(sketch, "E733", {"start": v(-116.83, 37.4) * mm, "end": v(-116.03, 37.4) * mm});
            skLineSegment(sketch, "E734", {"start": v(-130.82, 37.4) * mm, "end": v(-131.62, 37.4) * mm});
            skLineSegment(sketch, "E735", {"start": v(-149.88, 37.4) * mm, "end": v(-150.68, 37.4) * mm});
            skLineSegment(sketch, "E736", {"start": v(-78.72, 37.4) * mm, "end": v(-77.92, 37.4) * mm});
            skLineSegment(sketch, "E737", {"start": v(-92.73, 37.4) * mm, "end": v(-93.53, 37.4) * mm});
            skLineSegment(sketch, "E738", {"start": v(-97.78, 37.4) * mm, "end": v(-96.97, 37.4) * mm});
            skLineSegment(sketch, "E739", {"start": v(-111.78, 37.4) * mm, "end": v(-112.58, 37.4) * mm});
            skLineSegment(sketch, "E740", {"start": v(-40.62, 37.4) * mm, "end": v(-39.83, 37.4) * mm});
            skLineSegment(sketch, "E741", {"start": v(-54.62, 37.4) * mm, "end": v(-55.42, 37.4) * mm});
            skLineSegment(sketch, "E742", {"start": v(-59.67, 37.4) * mm, "end": v(-58.88, 37.4) * mm});
            skLineSegment(sketch, "E743", {"start": v(-73.68, 37.4) * mm, "end": v(-74.47, 37.4) * mm});
            skLineSegment(sketch, "E744", {"start": v(-21.57, 37.4) * mm, "end": v(-20.78, 37.4) * mm});
            skLineSegment(sketch, "E745", {"start": v(-35.58, 37.4) * mm, "end": v(-36.38, 37.4) * mm});
            skLineSegment(sketch, "E746", {"start": v(16.53, 37.4) * mm, "end": v(17.32, 37.4) * mm});
            skLineSegment(sketch, "E747", {"start": v(2.53, 37.4) * mm, "end": v(1.72, 37.4) * mm});
            skLineSegment(sketch, "E748", {"start": v(-2.53, 37.4) * mm, "end": v(-1.72, 37.4) * mm});
            skLineSegment(sketch, "E749", {"start": v(-16.53, 37.4) * mm, "end": v(-17.32, 37.4) * mm});
            skLineSegment(sketch, "E750", {"start": v(35.57, 37.4) * mm, "end": v(36.38, 37.4) * mm});
            skLineSegment(sketch, "E751", {"start": v(21.57, 37.4) * mm, "end": v(20.78, 37.4) * mm});
            skLineSegment(sketch, "E752", {"start": v(130.82, -38.8) * mm, "end": v(131.62, -38.8) * mm});
            skLineSegment(sketch, "E753", {"start": v(116.82, -38.8) * mm, "end": v(116.02, -38.8) * mm});
            skLineSegment(sketch, "E754", {"start": v(135.88, -38.8) * mm, "end": v(135.07, -38.8) * mm});
            skLineSegment(sketch, "E755", {"start": v(149.88, -38.8) * mm, "end": v(150.68, -38.8) * mm});
            skLineSegment(sketch, "E756", {"start": v(111.77, -38.8) * mm, "end": v(112.57, -38.8) * mm});
            skLineSegment(sketch, "E757", {"start": v(97.78, -38.8) * mm, "end": v(96.97, -38.8) * mm});
            skLineSegment(sketch, "E758", {"start": v(92.73, -38.8) * mm, "end": v(93.53, -38.8) * mm});
            skLineSegment(sketch, "E759", {"start": v(40.62, -38.8) * mm, "end": v(39.82, -38.8) * mm});
            skLineSegment(sketch, "E760", {"start": v(2.24, -19.75) * mm, "end": v(3.04, -19.75) * mm});
            skLineSegment(sketch, "E761", {"start": v(-11.76, -19.75) * mm, "end": v(-12.56, -19.75) * mm});
            skLineSegment(sketch, "E762", {"start": v(-16.81, -19.75) * mm, "end": v(-16.01, -19.75) * mm});
            skLineSegment(sketch, "E763", {"start": v(-30.81, -19.75) * mm, "end": v(-31.61, -19.75) * mm});
            skLineSegment(sketch, "E764", {"start": v(40.34, -19.75) * mm, "end": v(41.14, -19.75) * mm});
            skLineSegment(sketch, "E765", {"start": v(26.34, -19.75) * mm, "end": v(25.54, -19.75) * mm});
            skLineSegment(sketch, "E766", {"start": v(21.29, -19.75) * mm, "end": v(22.09, -19.75) * mm});
            skLineSegment(sketch, "E767", {"start": v(7.29, -19.75) * mm, "end": v(6.49, -19.75) * mm});
            skLineSegment(sketch, "E768", {"start": v(59.39, -19.75) * mm, "end": v(60.19, -19.75) * mm});
            skLineSegment(sketch, "E769", {"start": v(45.39, -19.75) * mm, "end": v(44.59, -19.75) * mm});
            skLineSegment(sketch, "E770", {"start": v(90.63, -19.75) * mm, "end": v(89.83, -19.75) * mm});
            skLineSegment(sketch, "E771", {"start": v(104.63, -19.75) * mm, "end": v(105.43, -19.75) * mm});
            skLineSegment(sketch, "E772", {"start": v(78.44, -19.75) * mm, "end": v(79.24, -19.75) * mm});
            skLineSegment(sketch, "E773", {"start": v(64.44, -19.75) * mm, "end": v(63.64, -19.75) * mm});
            skLineSegment(sketch, "E774", {"start": v(116.82, -19.75) * mm, "end": v(116.02, -19.75) * mm});
            skLineSegment(sketch, "E775", {"start": v(130.82, -19.75) * mm, "end": v(131.62, -19.75) * mm});
            skLineSegment(sketch, "E776", {"start": v(-133.5, -38.8) * mm, "end": v(-132.7, -38.8) * mm});
            skLineSegment(sketch, "E777", {"start": v(-147.5, -38.8) * mm, "end": v(-148.3, -38.8) * mm});
            skLineSegment(sketch, "E778", {"start": v(149.88, -19.75) * mm, "end": v(150.68, -19.75) * mm});
            skLineSegment(sketch, "E779", {"start": v(135.88, -19.75) * mm, "end": v(135.07, -19.75) * mm});
            skLineSegment(sketch, "E780", {"start": v(-99.87, -38.8) * mm, "end": v(-100.67, -38.8) * mm});
            skLineSegment(sketch, "E781", {"start": v(-85.87, -38.8) * mm, "end": v(-85.07, -38.8) * mm});
            skLineSegment(sketch, "E782", {"start": v(-123.68, -38.8) * mm, "end": v(-124.48, -38.8) * mm});
            skLineSegment(sketch, "E783", {"start": v(-109.68, -38.8) * mm, "end": v(-108.88, -38.8) * mm});
            skLineSegment(sketch, "E784", {"start": v(11.76, -0.7) * mm, "end": v(12.56, -0.7) * mm});
            skLineSegment(sketch, "E785", {"start": v(-2.24, -0.7) * mm, "end": v(-3.04, -0.7) * mm});
            skLineSegment(sketch, "E786", {"start": v(49.86, -0.7) * mm, "end": v(50.66, -0.7) * mm});
            skLineSegment(sketch, "E787", {"start": v(35.86, -0.7) * mm, "end": v(35.06, -0.7) * mm});
            skLineSegment(sketch, "E788", {"start": v(30.81, -0.7) * mm, "end": v(31.61, -0.7) * mm});
            skLineSegment(sketch, "E789", {"start": v(16.81, -0.7) * mm, "end": v(16.01, -0.7) * mm});
            skLineSegment(sketch, "E790", {"start": v(68.91, -0.7) * mm, "end": v(69.71, -0.7) * mm});
            skLineSegment(sketch, "E791", {"start": v(54.91, -0.7) * mm, "end": v(54.11, -0.7) * mm});
            skLineSegment(sketch, "E792", {"start": v(87.96, -0.7) * mm, "end": v(88.76, -0.7) * mm});
            skLineSegment(sketch, "E793", {"start": v(73.96, -0.7) * mm, "end": v(73.16, -0.7) * mm});
            skLineSegment(sketch, "E794", {"start": v(135.88, -0.7) * mm, "end": v(135.07, -0.7) * mm});
            skLineSegment(sketch, "E795", {"start": v(149.88, -0.7) * mm, "end": v(150.68, -0.7) * mm});
            skLineSegment(sketch, "E796", {"start": v(-107.01, -19.75) * mm, "end": v(-107.81, -19.75) * mm});
            skLineSegment(sketch, "E797", {"start": v(-93.01, -19.75) * mm, "end": v(-92.21, -19.75) * mm});
            skLineSegment(sketch, "E798", {"start": v(-54.91, -19.75) * mm, "end": v(-54.11, -19.75) * mm});
            skLineSegment(sketch, "E799", {"start": v(-68.91, -19.75) * mm, "end": v(-69.71, -19.75) * mm});
            skLineSegment(sketch, "E800", {"start": v(-73.96, -19.75) * mm, "end": v(-73.16, -19.75) * mm});
            skLineSegment(sketch, "E801", {"start": v(-87.96, -19.75) * mm, "end": v(-88.76, -19.75) * mm});
            skLineSegment(sketch, "E802", {"start": v(-35.86, -19.75) * mm, "end": v(-35.06, -19.75) * mm});
            skLineSegment(sketch, "E803", {"start": v(-49.86, -19.75) * mm, "end": v(-50.66, -19.75) * mm});
            skLineSegment(sketch, "E804", {"start": v(112.06, 18.35) * mm, "end": v(111.26, 18.35) * mm});
            skLineSegment(sketch, "E805", {"start": v(126.06, 18.35) * mm, "end": v(126.86, 18.35) * mm});
            skLineSegment(sketch, "E806", {"start": v(150.68, 18.35) * mm, "end": v(150.68, 14.85) * mm});
            skLineSegment(sketch, "E807", {"start": v(135.07, 18.35) * mm, "end": v(135.07, 14.85) * mm});
            skLineSegment(sketch, "E808", {"start": v(-117.34, -0.7) * mm, "end": v(-117.34, -4.2) * mm});
            skLineSegment(sketch, "E809", {"start": v(-101.74, -0.7) * mm, "end": v(-101.74, -4.2) * mm});
            skLineSegment(sketch, "E810", {"start": v(-127.93, -0.7) * mm, "end": v(-127.93, -4.2) * mm});
            skLineSegment(sketch, "E811", {"start": v(-143.53, -0.7) * mm, "end": v(-143.53, -4.2) * mm});
            skLineSegment(sketch, "E812", {"start": v(-82.69, -0.7) * mm, "end": v(-82.69, -4.2) * mm});
            skLineSegment(sketch, "E813", {"start": v(-98.29, -0.7) * mm, "end": v(-98.29, -4.2) * mm});
            skLineSegment(sketch, "E814", {"start": v(-44.59, -0.7) * mm, "end": v(-44.59, -4.2) * mm});
            skLineSegment(sketch, "E815", {"start": v(-60.19, -0.7) * mm, "end": v(-60.19, -4.2) * mm});
            skLineSegment(sketch, "E816", {"start": v(-63.64, -0.7) * mm, "end": v(-63.64, -4.2) * mm});
            skLineSegment(sketch, "E817", {"start": v(-79.24, -0.7) * mm, "end": v(-79.24, -4.2) * mm});
            skLineSegment(sketch, "E818", {"start": v(-6.49, -0.7) * mm, "end": v(-6.49, -4.2) * mm});
            skLineSegment(sketch, "E819", {"start": v(-22.09, -0.7) * mm, "end": v(-22.09, -4.2) * mm});
            skLineSegment(sketch, "E820", {"start": v(-25.54, -0.7) * mm, "end": v(-25.54, -4.2) * mm});
            skLineSegment(sketch, "E821", {"start": v(-41.14, -0.7) * mm, "end": v(-41.14, -4.2) * mm});
            skLineSegment(sketch, "E822", {"start": v(26.85, 18.35) * mm, "end": v(26.85, 14.85) * mm});
            skLineSegment(sketch, "E823", {"start": v(11.25, 18.35) * mm, "end": v(11.25, 14.85) * mm});
            skLineSegment(sketch, "E824", {"start": v(7.8, 18.35) * mm, "end": v(7.8, 14.85) * mm});
            skLineSegment(sketch, "E825", {"start": v(-7.8, 18.35) * mm, "end": v(-7.8, 14.85) * mm});
            skLineSegment(sketch, "E826", {"start": v(45.9, 18.35) * mm, "end": v(45.9, 14.85) * mm});
            skLineSegment(sketch, "E827", {"start": v(30.3, 18.35) * mm, "end": v(30.3, 14.85) * mm});
            skLineSegment(sketch, "E828", {"start": v(84, 18.35) * mm, "end": v(84, 14.85) * mm});
            skLineSegment(sketch, "E829", {"start": v(68.4, 18.35) * mm, "end": v(68.4, 14.85) * mm});
            skLineSegment(sketch, "E830", {"start": v(64.95, 18.35) * mm, "end": v(64.95, 14.85) * mm});
            skLineSegment(sketch, "E831", {"start": v(49.35, 18.35) * mm, "end": v(49.35, 14.85) * mm});
            skLineSegment(sketch, "E832", {"start": v(103.05, 18.35) * mm, "end": v(103.05, 14.85) * mm});
            skLineSegment(sketch, "E833", {"start": v(87.45, 18.35) * mm, "end": v(87.45, 14.85) * mm});
            skLineSegment(sketch, "E834", {"start": v(74.47, 37.4) * mm, "end": v(74.47, 33.9) * mm});
            skLineSegment(sketch, "E835", {"start": v(58.88, 37.4) * mm, "end": v(58.88, 33.9) * mm});
            skLineSegment(sketch, "E836", {"start": v(55.43, 37.4) * mm, "end": v(55.43, 33.9) * mm});
            skLineSegment(sketch, "E837", {"start": v(39.82, 37.4) * mm, "end": v(39.82, 33.9) * mm});
            skLineSegment(sketch, "E838", {"start": v(93.53, 37.4) * mm, "end": v(93.53, 33.9) * mm});
            skLineSegment(sketch, "E839", {"start": v(77.93, 37.4) * mm, "end": v(77.93, 33.9) * mm});
            skLineSegment(sketch, "E840", {"start": v(-130.31, 18.35) * mm, "end": v(-130.31, 14.85) * mm});
            skLineSegment(sketch, "E841", {"start": v(-145.91, 18.35) * mm, "end": v(-145.91, 14.85) * mm});
            skLineSegment(sketch, "E842", {"start": v(135.07, 37.4) * mm, "end": v(135.07, 33.9) * mm});
            skLineSegment(sketch, "E843", {"start": v(150.68, 37.4) * mm, "end": v(150.68, 33.9) * mm});
            skLineSegment(sketch, "E844", {"start": v(-122.1, 18.35) * mm, "end": v(-122.1, 14.85) * mm});
            skLineSegment(sketch, "E845", {"start": v(-106.5, 18.35) * mm, "end": v(-106.5, 14.85) * mm});
            skLineSegment(sketch, "E846", {"start": v(-68.4, 18.35) * mm, "end": v(-68.4, 14.85) * mm});
            skLineSegment(sketch, "E847", {"start": v(-84, 18.35) * mm, "end": v(-84, 14.85) * mm});
            skLineSegment(sketch, "E848", {"start": v(-87.45, 18.35) * mm, "end": v(-87.45, 14.85) * mm});
            skLineSegment(sketch, "E849", {"start": v(-103.05, 18.35) * mm, "end": v(-103.05, 14.85) * mm});
            skLineSegment(sketch, "E850", {"start": v(-49.35, 18.35) * mm, "end": v(-49.35, 14.85) * mm});
            skLineSegment(sketch, "E851", {"start": v(-64.95, 18.35) * mm, "end": v(-64.95, 14.85) * mm});
            skLineSegment(sketch, "E852", {"start": v(-11.25, 18.35) * mm, "end": v(-11.25, 14.85) * mm});
            skLineSegment(sketch, "E853", {"start": v(-26.85, 18.35) * mm, "end": v(-26.85, 14.85) * mm});
            skLineSegment(sketch, "E854", {"start": v(-30.3, 18.35) * mm, "end": v(-30.3, 14.85) * mm});
            skLineSegment(sketch, "E855", {"start": v(-45.9, 18.35) * mm, "end": v(-45.9, 14.85) * mm});
            skLineSegment(sketch, "E856", {"start": v(-150.68, 37.4) * mm, "end": v(-150.68, 33.9) * mm});
            skLineSegment(sketch, "E857", {"start": v(-135.07, 37.4) * mm, "end": v(-135.07, 33.9) * mm});
            skLineSegment(sketch, "E858", {"start": v(-116.03, 37.4) * mm, "end": v(-116.03, 33.9) * mm});
            skLineSegment(sketch, "E859", {"start": v(-131.62, 37.4) * mm, "end": v(-131.62, 33.9) * mm});
            skLineSegment(sketch, "E860", {"start": v(-77.92, 37.4) * mm, "end": v(-77.92, 33.9) * mm});
            skLineSegment(sketch, "E861", {"start": v(-93.53, 37.4) * mm, "end": v(-93.53, 33.9) * mm});
            skLineSegment(sketch, "E862", {"start": v(-96.97, 37.4) * mm, "end": v(-96.97, 33.9) * mm});
            skLineSegment(sketch, "E863", {"start": v(-112.58, 37.4) * mm, "end": v(-112.58, 33.9) * mm});
            skLineSegment(sketch, "E864", {"start": v(-58.88, 37.4) * mm, "end": v(-58.88, 33.9) * mm});
            skLineSegment(sketch, "E865", {"start": v(-74.47, 37.4) * mm, "end": v(-74.47, 33.9) * mm});
            skLineSegment(sketch, "E866", {"start": v(-20.78, 37.4) * mm, "end": v(-20.78, 33.9) * mm});
            skLineSegment(sketch, "E867", {"start": v(-36.38, 37.4) * mm, "end": v(-36.38, 33.9) * mm});
            skLineSegment(sketch, "E868", {"start": v(-39.83, 37.4) * mm, "end": v(-39.83, 33.9) * mm});
            skLineSegment(sketch, "E869", {"start": v(-55.42, 37.4) * mm, "end": v(-55.42, 33.9) * mm});
            skLineSegment(sketch, "E870", {"start": v(17.32, 37.4) * mm, "end": v(17.32, 33.9) * mm});
            skLineSegment(sketch, "E871", {"start": v(1.72, 37.4) * mm, "end": v(1.72, 33.9) * mm});
            skLineSegment(sketch, "E872", {"start": v(-1.72, 37.4) * mm, "end": v(-1.72, 33.9) * mm});
            skLineSegment(sketch, "E873", {"start": v(-17.32, 37.4) * mm, "end": v(-17.32, 33.9) * mm});
            skLineSegment(sketch, "E874", {"start": v(36.38, 37.4) * mm, "end": v(36.38, 33.9) * mm});
            skLineSegment(sketch, "E875", {"start": v(20.78, 37.4) * mm, "end": v(20.78, 33.9) * mm});
            skLineSegment(sketch, "E876", {"start": v(131.62, -38.8) * mm, "end": v(131.62, -42.3) * mm});
            skLineSegment(sketch, "E877", {"start": v(116.02, -38.8) * mm, "end": v(116.02, -42.3) * mm});
            skLineSegment(sketch, "E878", {"start": v(135.07, -38.8) * mm, "end": v(135.07, -42.3) * mm});
            skLineSegment(sketch, "E879", {"start": v(150.68, -38.8) * mm, "end": v(150.68, -42.3) * mm});
            skLineSegment(sketch, "E880", {"start": v(112.57, -38.8) * mm, "end": v(112.57, -42.3) * mm});
            skLineSegment(sketch, "E881", {"start": v(96.97, -38.8) * mm, "end": v(96.97, -42.3) * mm});
            skLineSegment(sketch, "E882", {"start": v(93.53, -38.8) * mm, "end": v(93.53, -42.3) * mm});
            skLineSegment(sketch, "E883", {"start": v(39.82, -38.8) * mm, "end": v(39.82, -42.3) * mm});
            skLineSegment(sketch, "E884", {"start": v(3.04, -19.75) * mm, "end": v(3.04, -23.25) * mm});
            skLineSegment(sketch, "E885", {"start": v(-12.56, -19.75) * mm, "end": v(-12.56, -23.25) * mm});
            skLineSegment(sketch, "E886", {"start": v(-16.01, -19.75) * mm, "end": v(-16.01, -23.25) * mm});
            skLineSegment(sketch, "E887", {"start": v(-31.61, -19.75) * mm, "end": v(-31.61, -23.25) * mm});
            skLineSegment(sketch, "E888", {"start": v(41.14, -19.75) * mm, "end": v(41.14, -23.25) * mm});
            skLineSegment(sketch, "E889", {"start": v(25.54, -19.75) * mm, "end": v(25.54, -23.25) * mm});
            skLineSegment(sketch, "E890", {"start": v(22.09, -19.75) * mm, "end": v(22.09, -23.25) * mm});
            skLineSegment(sketch, "E891", {"start": v(6.49, -19.75) * mm, "end": v(6.49, -23.25) * mm});
            skLineSegment(sketch, "E892", {"start": v(60.19, -19.75) * mm, "end": v(60.19, -23.25) * mm});
            skLineSegment(sketch, "E893", {"start": v(44.59, -19.75) * mm, "end": v(44.59, -23.25) * mm});
            skLineSegment(sketch, "E894", {"start": v(89.83, -19.75) * mm, "end": v(89.83, -23.25) * mm});
            skLineSegment(sketch, "E895", {"start": v(105.43, -19.75) * mm, "end": v(105.43, -23.25) * mm});
            skLineSegment(sketch, "E896", {"start": v(79.24, -19.75) * mm, "end": v(79.24, -23.25) * mm});
            skLineSegment(sketch, "E897", {"start": v(63.64, -19.75) * mm, "end": v(63.64, -23.25) * mm});
            skLineSegment(sketch, "E898", {"start": v(116.02, -19.75) * mm, "end": v(116.02, -23.25) * mm});
            skLineSegment(sketch, "E899", {"start": v(131.62, -19.75) * mm, "end": v(131.62, -23.25) * mm});
            skLineSegment(sketch, "E900", {"start": v(-132.7, -38.8) * mm, "end": v(-132.7, -42.3) * mm});
            skLineSegment(sketch, "E901", {"start": v(-148.3, -38.8) * mm, "end": v(-148.3, -42.3) * mm});
            skLineSegment(sketch, "E902", {"start": v(150.68, -19.75) * mm, "end": v(150.68, -23.25) * mm});
            skLineSegment(sketch, "E903", {"start": v(135.07, -19.75) * mm, "end": v(135.07, -23.25) * mm});
            skLineSegment(sketch, "E904", {"start": v(-100.67, -38.8) * mm, "end": v(-100.67, -42.3) * mm});
            skLineSegment(sketch, "E905", {"start": v(-85.07, -38.8) * mm, "end": v(-85.07, -42.3) * mm});
            skLineSegment(sketch, "E906", {"start": v(-124.48, -38.8) * mm, "end": v(-124.48, -42.3) * mm});
            skLineSegment(sketch, "E907", {"start": v(-108.88, -38.8) * mm, "end": v(-108.88, -42.3) * mm});
            skLineSegment(sketch, "E908", {"start": v(12.56, -0.7) * mm, "end": v(12.56, -4.2) * mm});
            skLineSegment(sketch, "E909", {"start": v(-3.04, -0.7) * mm, "end": v(-3.04, -4.2) * mm});
            skLineSegment(sketch, "E910", {"start": v(50.66, -0.7) * mm, "end": v(50.66, -4.2) * mm});
            skLineSegment(sketch, "E911", {"start": v(35.06, -0.7) * mm, "end": v(35.06, -4.2) * mm});
            skLineSegment(sketch, "E912", {"start": v(31.61, -0.7) * mm, "end": v(31.61, -4.2) * mm});
            skLineSegment(sketch, "E913", {"start": v(16.01, -0.7) * mm, "end": v(16.01, -4.2) * mm});
            skLineSegment(sketch, "E914", {"start": v(69.71, -0.7) * mm, "end": v(69.71, -4.2) * mm});
            skLineSegment(sketch, "E915", {"start": v(54.11, -0.7) * mm, "end": v(54.11, -4.2) * mm});
            skLineSegment(sketch, "E916", {"start": v(88.76, -0.7) * mm, "end": v(88.76, -4.2) * mm});
            skLineSegment(sketch, "E917", {"start": v(73.16, -0.7) * mm, "end": v(73.16, -4.2) * mm});
            skLineSegment(sketch, "E918", {"start": v(135.07, -0.7) * mm, "end": v(135.07, -4.2) * mm});
            skLineSegment(sketch, "E919", {"start": v(150.68, -0.7) * mm, "end": v(150.68, -4.2) * mm});
            skLineSegment(sketch, "E920", {"start": v(-107.81, -19.75) * mm, "end": v(-107.81, -23.25) * mm});
            skLineSegment(sketch, "E921", {"start": v(-92.21, -19.75) * mm, "end": v(-92.21, -23.25) * mm});
            skLineSegment(sketch, "E922", {"start": v(-54.11, -19.75) * mm, "end": v(-54.11, -23.25) * mm});
            skLineSegment(sketch, "E923", {"start": v(-69.71, -19.75) * mm, "end": v(-69.71, -23.25) * mm});
            skLineSegment(sketch, "E924", {"start": v(-73.16, -19.75) * mm, "end": v(-73.16, -23.25) * mm});
            skLineSegment(sketch, "E925", {"start": v(-88.76, -19.75) * mm, "end": v(-88.76, -23.25) * mm});
            skLineSegment(sketch, "E926", {"start": v(-35.06, -19.75) * mm, "end": v(-35.06, -23.25) * mm});
            skLineSegment(sketch, "E927", {"start": v(-50.66, -19.75) * mm, "end": v(-50.66, -23.25) * mm});
            skLineSegment(sketch, "E928", {"start": v(111.26, 18.35) * mm, "end": v(111.26, 14.85) * mm});
            skLineSegment(sketch, "E929", {"start": v(126.86, 18.35) * mm, "end": v(126.86, 14.85) * mm});
            skLineSegment(sketch, "E930", {"start": v(150.68, 14.85) * mm, "end": v(149.88, 14.85) * mm});
            skLineSegment(sketch, "E931", {"start": v(111.26, 14.85) * mm, "end": v(112.06, 14.85) * mm});
            skLineSegment(sketch, "E932", {"start": v(126.86, 14.85) * mm, "end": v(126.06, 14.85) * mm});
            skLineSegment(sketch, "E933", {"start": v(-117.34, -4.2) * mm, "end": v(-116.54, -4.2) * mm});
            skLineSegment(sketch, "E934", {"start": v(-101.74, -4.2) * mm, "end": v(-102.54, -4.2) * mm});
            skLineSegment(sketch, "E935", {"start": v(-127.93, -4.2) * mm, "end": v(-128.73, -4.2) * mm});
            skLineSegment(sketch, "E936", {"start": v(-143.53, -4.2) * mm, "end": v(-142.73, -4.2) * mm});
            skLineSegment(sketch, "E937", {"start": v(-82.69, -4.2) * mm, "end": v(-83.49, -4.2) * mm});
            skLineSegment(sketch, "E938", {"start": v(-98.29, -4.2) * mm, "end": v(-97.49, -4.2) * mm});
            skLineSegment(sketch, "E939", {"start": v(-44.59, -4.2) * mm, "end": v(-45.39, -4.2) * mm});
            skLineSegment(sketch, "E940", {"start": v(-60.19, -4.2) * mm, "end": v(-59.39, -4.2) * mm});
            skLineSegment(sketch, "E941", {"start": v(-63.64, -4.2) * mm, "end": v(-64.44, -4.2) * mm});
            skLineSegment(sketch, "E942", {"start": v(-79.24, -4.2) * mm, "end": v(-78.44, -4.2) * mm});
            skLineSegment(sketch, "E943", {"start": v(-25.54, -4.2) * mm, "end": v(-26.34, -4.2) * mm});
            skLineSegment(sketch, "E944", {"start": v(-41.14, -4.2) * mm, "end": v(-40.34, -4.2) * mm});
            skLineSegment(sketch, "E945", {"start": v(7.8, 14.85) * mm, "end": v(7, 14.85) * mm});
            skLineSegment(sketch, "E946", {"start": v(-7.8, 14.85) * mm, "end": v(-7, 14.85) * mm});
            skLineSegment(sketch, "E947", {"start": v(45.9, 14.85) * mm, "end": v(45.1, 14.85) * mm});
            skLineSegment(sketch, "E948", {"start": v(30.3, 14.85) * mm, "end": v(31.1, 14.85) * mm});
            skLineSegment(sketch, "E949", {"start": v(26.85, 14.85) * mm, "end": v(26.05, 14.85) * mm});
            skLineSegment(sketch, "E950", {"start": v(11.25, 14.85) * mm, "end": v(12.05, 14.85) * mm});
            skLineSegment(sketch, "E951", {"start": v(84, 14.85) * mm, "end": v(83.2, 14.85) * mm});
            skLineSegment(sketch, "E952", {"start": v(68.4, 14.85) * mm, "end": v(69.2, 14.85) * mm});
            skLineSegment(sketch, "E953", {"start": v(64.95, 14.85) * mm, "end": v(64.15, 14.85) * mm});
            skLineSegment(sketch, "E954", {"start": v(49.35, 14.85) * mm, "end": v(50.15, 14.85) * mm});
            skLineSegment(sketch, "E955", {"start": v(103.05, 14.85) * mm, "end": v(102.25, 14.85) * mm});
            skLineSegment(sketch, "E956", {"start": v(87.45, 14.85) * mm, "end": v(88.25, 14.85) * mm});
            skLineSegment(sketch, "E957", {"start": v(74.47, 33.9) * mm, "end": v(73.68, 33.9) * mm});
            skLineSegment(sketch, "E958", {"start": v(58.88, 33.9) * mm, "end": v(59.68, 33.9) * mm});
            skLineSegment(sketch, "E959", {"start": v(55.43, 33.9) * mm, "end": v(54.62, 33.9) * mm});
            skLineSegment(sketch, "E960", {"start": v(39.82, 33.9) * mm, "end": v(40.62, 33.9) * mm});
            skLineSegment(sketch, "E961", {"start": v(93.53, 33.9) * mm, "end": v(92.73, 33.9) * mm});
            skLineSegment(sketch, "E962", {"start": v(77.93, 33.9) * mm, "end": v(78.72, 33.9) * mm});
            skLineSegment(sketch, "E963", {"start": v(-130.31, 14.85) * mm, "end": v(-131.11, 14.85) * mm});
            skLineSegment(sketch, "E964", {"start": v(-145.91, 14.85) * mm, "end": v(-145.11, 14.85) * mm});
            skLineSegment(sketch, "E965", {"start": v(150.68, 33.9) * mm, "end": v(149.88, 33.9) * mm});
            skLineSegment(sketch, "E966", {"start": v(135.07, 33.9) * mm, "end": v(135.88, 33.9) * mm});
            skLineSegment(sketch, "E967", {"start": v(-122.1, 14.85) * mm, "end": v(-121.3, 14.85) * mm});
            skLineSegment(sketch, "E968", {"start": v(-106.5, 14.85) * mm, "end": v(-107.3, 14.85) * mm});
            skLineSegment(sketch, "E969", {"start": v(-68.4, 14.85) * mm, "end": v(-69.2, 14.85) * mm});
            skLineSegment(sketch, "E970", {"start": v(-84, 14.85) * mm, "end": v(-83.2, 14.85) * mm});
            skLineSegment(sketch, "E971", {"start": v(-87.45, 14.85) * mm, "end": v(-88.25, 14.85) * mm});
            skLineSegment(sketch, "E972", {"start": v(-103.05, 14.85) * mm, "end": v(-102.25, 14.85) * mm});
            skLineSegment(sketch, "E973", {"start": v(-49.35, 14.85) * mm, "end": v(-50.15, 14.85) * mm});
            skLineSegment(sketch, "E974", {"start": v(-64.95, 14.85) * mm, "end": v(-64.15, 14.85) * mm});
            skLineSegment(sketch, "E975", {"start": v(-11.25, 14.85) * mm, "end": v(-12.05, 14.85) * mm});
            skLineSegment(sketch, "E976", {"start": v(-26.85, 14.85) * mm, "end": v(-26.05, 14.85) * mm});
            skLineSegment(sketch, "E977", {"start": v(-30.3, 14.85) * mm, "end": v(-31.1, 14.85) * mm});
            skLineSegment(sketch, "E978", {"start": v(-45.9, 14.85) * mm, "end": v(-45.1, 14.85) * mm});
            skLineSegment(sketch, "E979", {"start": v(-150.68, 33.9) * mm, "end": v(-149.88, 33.9) * mm});
            skLineSegment(sketch, "E980", {"start": v(-135.07, 33.9) * mm, "end": v(-135.88, 33.9) * mm});
            skLineSegment(sketch, "E981", {"start": v(-116.03, 33.9) * mm, "end": v(-116.83, 33.9) * mm});
            skLineSegment(sketch, "E982", {"start": v(-131.62, 33.9) * mm, "end": v(-130.82, 33.9) * mm});
            skLineSegment(sketch, "E983", {"start": v(-77.92, 33.9) * mm, "end": v(-78.72, 33.9) * mm});
            skLineSegment(sketch, "E984", {"start": v(-93.53, 33.9) * mm, "end": v(-92.73, 33.9) * mm});
            skLineSegment(sketch, "E985", {"start": v(-96.97, 33.9) * mm, "end": v(-97.78, 33.9) * mm});
            skLineSegment(sketch, "E986", {"start": v(-112.58, 33.9) * mm, "end": v(-111.78, 33.9) * mm});
            skLineSegment(sketch, "E987", {"start": v(-58.88, 33.9) * mm, "end": v(-59.67, 33.9) * mm});
            skLineSegment(sketch, "E988", {"start": v(-74.47, 33.9) * mm, "end": v(-73.68, 33.9) * mm});
            skLineSegment(sketch, "E989", {"start": v(-20.78, 33.9) * mm, "end": v(-21.57, 33.9) * mm});
            skLineSegment(sketch, "E990", {"start": v(-36.38, 33.9) * mm, "end": v(-35.58, 33.9) * mm});
            skLineSegment(sketch, "E991", {"start": v(-39.83, 33.9) * mm, "end": v(-40.62, 33.9) * mm});
            skLineSegment(sketch, "E992", {"start": v(-55.42, 33.9) * mm, "end": v(-54.62, 33.9) * mm});
            skLineSegment(sketch, "E993", {"start": v(17.32, 33.9) * mm, "end": v(16.53, 33.9) * mm});
            skLineSegment(sketch, "E994", {"start": v(1.72, 33.9) * mm, "end": v(2.53, 33.9) * mm});
            skLineSegment(sketch, "E995", {"start": v(-1.72, 33.9) * mm, "end": v(-2.53, 33.9) * mm});
            skLineSegment(sketch, "E996", {"start": v(-17.32, 33.9) * mm, "end": v(-16.53, 33.9) * mm});
            skLineSegment(sketch, "E997", {"start": v(36.38, 33.9) * mm, "end": v(35.57, 33.9) * mm});
            skLineSegment(sketch, "E998", {"start": v(20.78, 33.9) * mm, "end": v(21.57, 33.9) * mm});
            skLineSegment(sketch, "E999", {"start": v(131.62, -42.3) * mm, "end": v(130.82, -42.3) * mm});
            skLineSegment(sketch, "E1000", {"start": v(116.02, -42.3) * mm, "end": v(116.82, -42.3) * mm});
            skLineSegment(sketch, "E1001", {"start": v(135.07, -42.3) * mm, "end": v(135.88, -42.3) * mm});
            skLineSegment(sketch, "E1002", {"start": v(150.68, -42.3) * mm, "end": v(149.88, -42.3) * mm});
            skLineSegment(sketch, "E1003", {"start": v(112.57, -42.3) * mm, "end": v(111.77, -42.3) * mm});
            skLineSegment(sketch, "E1004", {"start": v(96.97, -42.3) * mm, "end": v(97.78, -42.3) * mm});
            skLineSegment(sketch, "E1005", {"start": v(93.53, -42.3) * mm, "end": v(92.73, -42.3) * mm});
            skLineSegment(sketch, "E1006", {"start": v(39.82, -42.3) * mm, "end": v(40.62, -42.3) * mm});
            skLineSegment(sketch, "E1007", {"start": v(3.04, -23.25) * mm, "end": v(2.24, -23.25) * mm});
            skLineSegment(sketch, "E1008", {"start": v(-12.56, -23.25) * mm, "end": v(-11.76, -23.25) * mm});
            skLineSegment(sketch, "E1009", {"start": v(-16.01, -23.25) * mm, "end": v(-16.81, -23.25) * mm});
            skLineSegment(sketch, "E1010", {"start": v(-31.61, -23.25) * mm, "end": v(-30.81, -23.25) * mm});
            skLineSegment(sketch, "E1011", {"start": v(22.09, -23.25) * mm, "end": v(21.29, -23.25) * mm});
            skLineSegment(sketch, "E1012", {"start": v(6.49, -23.25) * mm, "end": v(7.29, -23.25) * mm});
            skLineSegment(sketch, "E1013", {"start": v(60.19, -23.25) * mm, "end": v(59.39, -23.25) * mm});
            skLineSegment(sketch, "E1014", {"start": v(44.59, -23.25) * mm, "end": v(45.39, -23.25) * mm});
            skLineSegment(sketch, "E1015", {"start": v(41.14, -23.25) * mm, "end": v(40.34, -23.25) * mm});
            skLineSegment(sketch, "E1016", {"start": v(25.54, -23.25) * mm, "end": v(26.34, -23.25) * mm});
            skLineSegment(sketch, "E1017", {"start": v(89.83, -23.25) * mm, "end": v(90.63, -23.25) * mm});
            skLineSegment(sketch, "E1018", {"start": v(105.43, -23.25) * mm, "end": v(104.63, -23.25) * mm});
            skLineSegment(sketch, "E1019", {"start": v(79.24, -23.25) * mm, "end": v(78.44, -23.25) * mm});
            skLineSegment(sketch, "E1020", {"start": v(63.64, -23.25) * mm, "end": v(64.44, -23.25) * mm});
            skLineSegment(sketch, "E1021", {"start": v(116.02, -23.25) * mm, "end": v(116.82, -23.25) * mm});
            skLineSegment(sketch, "E1022", {"start": v(131.62, -23.25) * mm, "end": v(130.82, -23.25) * mm});
            skLineSegment(sketch, "E1023", {"start": v(-132.7, -42.3) * mm, "end": v(-133.5, -42.3) * mm});
            skLineSegment(sketch, "E1024", {"start": v(-148.3, -42.3) * mm, "end": v(-147.5, -42.3) * mm});
            skLineSegment(sketch, "E1025", {"start": v(150.68, -23.25) * mm, "end": v(149.88, -23.25) * mm});
            skLineSegment(sketch, "E1026", {"start": v(135.07, -23.25) * mm, "end": v(135.88, -23.25) * mm});
            skLineSegment(sketch, "E1027", {"start": v(-124.48, -42.3) * mm, "end": v(-123.68, -42.3) * mm});
            skLineSegment(sketch, "E1028", {"start": v(-108.88, -42.3) * mm, "end": v(-109.68, -42.3) * mm});
            skLineSegment(sketch, "E1029", {"start": v(-100.67, -42.3) * mm, "end": v(-99.87, -42.3) * mm});
            skLineSegment(sketch, "E1030", {"start": v(-85.07, -42.3) * mm, "end": v(-85.87, -42.3) * mm});
            skLineSegment(sketch, "E1031", {"start": v(12.56, -4.2) * mm, "end": v(11.76, -4.2) * mm});
            skLineSegment(sketch, "E1032", {"start": v(-3.04, -4.2) * mm, "end": v(-2.24, -4.2) * mm});
            skLineSegment(sketch, "E1033", {"start": v(-6.49, -4.2) * mm, "end": v(-7.29, -4.2) * mm});
            skLineSegment(sketch, "E1034", {"start": v(-22.09, -4.2) * mm, "end": v(-21.29, -4.2) * mm});
            skLineSegment(sketch, "E1035", {"start": v(50.66, -4.2) * mm, "end": v(49.86, -4.2) * mm});
            skLineSegment(sketch, "E1036", {"start": v(35.06, -4.2) * mm, "end": v(35.86, -4.2) * mm});
            skLineSegment(sketch, "E1037", {"start": v(31.61, -4.2) * mm, "end": v(30.81, -4.2) * mm});
            skLineSegment(sketch, "E1038", {"start": v(16.01, -4.2) * mm, "end": v(16.81, -4.2) * mm});
            skLineSegment(sketch, "E1039", {"start": v(69.71, -4.2) * mm, "end": v(68.91, -4.2) * mm});
            skLineSegment(sketch, "E1040", {"start": v(54.11, -4.2) * mm, "end": v(54.91, -4.2) * mm});
            skLineSegment(sketch, "E1041", {"start": v(88.76, -4.2) * mm, "end": v(87.96, -4.2) * mm});
            skLineSegment(sketch, "E1042", {"start": v(73.16, -4.2) * mm, "end": v(73.96, -4.2) * mm});
            skLineSegment(sketch, "E1043", {"start": v(135.07, -4.2) * mm, "end": v(135.88, -4.2) * mm});
            skLineSegment(sketch, "E1044", {"start": v(150.68, -4.2) * mm, "end": v(149.88, -4.2) * mm});
            skLineSegment(sketch, "E1045", {"start": v(-107.81, -23.25) * mm, "end": v(-107.01, -23.25) * mm});
            skLineSegment(sketch, "E1046", {"start": v(-92.21, -23.25) * mm, "end": v(-93.01, -23.25) * mm});
            skLineSegment(sketch, "E1047", {"start": v(-54.11, -23.25) * mm, "end": v(-54.91, -23.25) * mm});
            skLineSegment(sketch, "E1048", {"start": v(-69.71, -23.25) * mm, "end": v(-68.91, -23.25) * mm});
            skLineSegment(sketch, "E1049", {"start": v(-73.16, -23.25) * mm, "end": v(-73.96, -23.25) * mm});
            skLineSegment(sketch, "E1050", {"start": v(-88.76, -23.25) * mm, "end": v(-87.96, -23.25) * mm});
            skLineSegment(sketch, "E1051", {"start": v(-35.06, -23.25) * mm, "end": v(-35.86, -23.25) * mm});
            skLineSegment(sketch, "E1052", {"start": v(-50.66, -23.25) * mm, "end": v(-49.86, -23.25) * mm});
            skLineSegment(sketch, "E1053", {"start": v(135.07, 14.85) * mm, "end": v(135.88, 14.85) * mm});
            skLineSegment(sketch, "E1054", {"start": v(149.88, 14.85) * mm, "end": v(149.88, 13.85) * mm});
            skLineSegment(sketch, "E1055", {"start": v(135.88, 14.85) * mm, "end": v(135.88, 13.85) * mm});
            skLineSegment(sketch, "E1056", {"start": v(112.06, 14.85) * mm, "end": v(112.06, 13.85) * mm});
            skLineSegment(sketch, "E1057", {"start": v(126.06, 14.85) * mm, "end": v(126.06, 13.85) * mm});
            skLineSegment(sketch, "E1058", {"start": v(-116.54, -4.2) * mm, "end": v(-116.54, -5.2) * mm});
            skLineSegment(sketch, "E1059", {"start": v(-102.54, -4.2) * mm, "end": v(-102.54, -5.2) * mm});
            skLineSegment(sketch, "E1060", {"start": v(-128.73, -4.2) * mm, "end": v(-128.73, -5.2) * mm});
            skLineSegment(sketch, "E1061", {"start": v(-142.73, -4.2) * mm, "end": v(-142.73, -5.2) * mm});
            skLineSegment(sketch, "E1062", {"start": v(-83.49, -4.2) * mm, "end": v(-83.49, -5.2) * mm});
            skLineSegment(sketch, "E1063", {"start": v(-97.49, -4.2) * mm, "end": v(-97.49, -5.2) * mm});
            skLineSegment(sketch, "E1064", {"start": v(-45.39, -4.2) * mm, "end": v(-45.39, -5.2) * mm});
            skLineSegment(sketch, "E1065", {"start": v(-59.39, -4.2) * mm, "end": v(-59.39, -5.2) * mm});
            skLineSegment(sketch, "E1066", {"start": v(-64.44, -4.2) * mm, "end": v(-64.44, -5.2) * mm});
            skLineSegment(sketch, "E1067", {"start": v(-78.44, -4.2) * mm, "end": v(-78.44, -5.2) * mm});
            skLineSegment(sketch, "E1068", {"start": v(-26.34, -4.2) * mm, "end": v(-26.34, -5.2) * mm});
            skLineSegment(sketch, "E1069", {"start": v(-40.34, -4.2) * mm, "end": v(-40.34, -5.2) * mm});
            skLineSegment(sketch, "E1070", {"start": v(7, 14.85) * mm, "end": v(7, 13.85) * mm});
            skLineSegment(sketch, "E1071", {"start": v(-7, 14.85) * mm, "end": v(-7, 13.85) * mm});
            skLineSegment(sketch, "E1072", {"start": v(45.1, 14.85) * mm, "end": v(45.1, 13.85) * mm});
            skLineSegment(sketch, "E1073", {"start": v(31.1, 14.85) * mm, "end": v(31.1, 13.85) * mm});
            skLineSegment(sketch, "E1074", {"start": v(26.05, 14.85) * mm, "end": v(26.05, 13.85) * mm});
            skLineSegment(sketch, "E1075", {"start": v(12.05, 14.85) * mm, "end": v(12.05, 13.85) * mm});
            skLineSegment(sketch, "E1076", {"start": v(83.2, 14.85) * mm, "end": v(83.2, 13.85) * mm});
            skLineSegment(sketch, "E1077", {"start": v(69.2, 14.85) * mm, "end": v(69.2, 13.85) * mm});
            skLineSegment(sketch, "E1078", {"start": v(64.15, 14.85) * mm, "end": v(64.15, 13.85) * mm});
            skLineSegment(sketch, "E1079", {"start": v(50.15, 14.85) * mm, "end": v(50.15, 13.85) * mm});
            skLineSegment(sketch, "E1080", {"start": v(102.25, 14.85) * mm, "end": v(102.25, 13.85) * mm});
            skLineSegment(sketch, "E1081", {"start": v(88.25, 14.85) * mm, "end": v(88.25, 13.85) * mm});
            skLineSegment(sketch, "E1082", {"start": v(73.68, 33.9) * mm, "end": v(73.68, 32.9) * mm});
            skLineSegment(sketch, "E1083", {"start": v(59.68, 33.9) * mm, "end": v(59.68, 32.9) * mm});
            skLineSegment(sketch, "E1084", {"start": v(54.62, 33.9) * mm, "end": v(54.62, 32.9) * mm});
            skLineSegment(sketch, "E1085", {"start": v(40.62, 33.9) * mm, "end": v(40.62, 32.9) * mm});
            skLineSegment(sketch, "E1086", {"start": v(92.73, 33.9) * mm, "end": v(92.73, 32.9) * mm});
            skLineSegment(sketch, "E1087", {"start": v(78.72, 33.9) * mm, "end": v(78.72, 32.9) * mm});
            skLineSegment(sketch, "E1088", {"start": v(135.88, 33.9) * mm, "end": v(135.88, 32.9) * mm});
            skLineSegment(sketch, "E1089", {"start": v(149.88, 33.9) * mm, "end": v(149.88, 32.9) * mm});
            skLineSegment(sketch, "E1090", {"start": v(-121.3, 14.85) * mm, "end": v(-121.3, 13.85) * mm});
            skLineSegment(sketch, "E1091", {"start": v(-107.3, 14.85) * mm, "end": v(-107.3, 13.85) * mm});
            skLineSegment(sketch, "E1092", {"start": v(-131.11, 14.85) * mm, "end": v(-131.11, 13.85) * mm});
            skLineSegment(sketch, "E1093", {"start": v(-145.11, 14.85) * mm, "end": v(-145.11, 13.85) * mm});
            skLineSegment(sketch, "E1094", {"start": v(-69.2, 14.85) * mm, "end": v(-69.2, 13.85) * mm});
            skLineSegment(sketch, "E1095", {"start": v(-83.2, 14.85) * mm, "end": v(-83.2, 13.85) * mm});
            skLineSegment(sketch, "E1096", {"start": v(-88.25, 14.85) * mm, "end": v(-88.25, 13.85) * mm});
            skLineSegment(sketch, "E1097", {"start": v(-102.25, 14.85) * mm, "end": v(-102.25, 13.85) * mm});
            skLineSegment(sketch, "E1098", {"start": v(-50.15, 14.85) * mm, "end": v(-50.15, 13.85) * mm});
            skLineSegment(sketch, "E1099", {"start": v(-64.15, 14.85) * mm, "end": v(-64.15, 13.85) * mm});
            skLineSegment(sketch, "E1100", {"start": v(-12.05, 14.85) * mm, "end": v(-12.05, 13.85) * mm});
            skLineSegment(sketch, "E1101", {"start": v(-26.05, 14.85) * mm, "end": v(-26.05, 13.85) * mm});
            skLineSegment(sketch, "E1102", {"start": v(-31.1, 14.85) * mm, "end": v(-31.1, 13.85) * mm});
            skLineSegment(sketch, "E1103", {"start": v(-45.1, 14.85) * mm, "end": v(-45.1, 13.85) * mm});
            skLineSegment(sketch, "E1104", {"start": v(-135.88, 33.9) * mm, "end": v(-135.88, 32.9) * mm});
            skLineSegment(sketch, "E1105", {"start": v(-116.83, 33.9) * mm, "end": v(-116.83, 32.9) * mm});
            skLineSegment(sketch, "E1106", {"start": v(-130.82, 33.9) * mm, "end": v(-130.82, 32.9) * mm});
            skLineSegment(sketch, "E1107", {"start": v(-149.88, 33.9) * mm, "end": v(-149.88, 32.9) * mm});
            skLineSegment(sketch, "E1108", {"start": v(-78.72, 33.9) * mm, "end": v(-78.72, 32.9) * mm});
            skLineSegment(sketch, "E1109", {"start": v(-92.73, 33.9) * mm, "end": v(-92.73, 32.9) * mm});
            skLineSegment(sketch, "E1110", {"start": v(-97.78, 33.9) * mm, "end": v(-97.78, 32.9) * mm});
            skLineSegment(sketch, "E1111", {"start": v(-111.78, 33.9) * mm, "end": v(-111.78, 32.9) * mm});
            skLineSegment(sketch, "E1112", {"start": v(-59.67, 33.9) * mm, "end": v(-59.67, 32.9) * mm});
            skLineSegment(sketch, "E1113", {"start": v(-73.68, 33.9) * mm, "end": v(-73.68, 32.9) * mm});
            skLineSegment(sketch, "E1114", {"start": v(-21.57, 33.9) * mm, "end": v(-21.57, 32.9) * mm});
            skLineSegment(sketch, "E1115", {"start": v(-35.58, 33.9) * mm, "end": v(-35.58, 32.9) * mm});
            skLineSegment(sketch, "E1116", {"start": v(-40.62, 33.9) * mm, "end": v(-40.62, 32.9) * mm});
            skLineSegment(sketch, "E1117", {"start": v(-54.62, 33.9) * mm, "end": v(-54.62, 32.9) * mm});
            skLineSegment(sketch, "E1118", {"start": v(-2.53, 33.9) * mm, "end": v(-2.53, 32.9) * mm});
            skLineSegment(sketch, "E1119", {"start": v(-16.53, 33.9) * mm, "end": v(-16.53, 32.9) * mm});
            skLineSegment(sketch, "E1120", {"start": v(35.57, 33.9) * mm, "end": v(35.57, 32.9) * mm});
            skLineSegment(sketch, "E1121", {"start": v(21.57, 33.9) * mm, "end": v(21.57, 32.9) * mm});
            skLineSegment(sketch, "E1122", {"start": v(16.53, 33.9) * mm, "end": v(16.53, 32.9) * mm});
            skLineSegment(sketch, "E1123", {"start": v(2.53, 33.9) * mm, "end": v(2.53, 32.9) * mm});
            skLineSegment(sketch, "E1124", {"start": v(130.82, -42.3) * mm, "end": v(130.82, -43.3) * mm});
            skLineSegment(sketch, "E1125", {"start": v(116.82, -42.3) * mm, "end": v(116.82, -43.3) * mm});
            skLineSegment(sketch, "E1126", {"start": v(135.88, -42.3) * mm, "end": v(135.88, -43.3) * mm});
            skLineSegment(sketch, "E1127", {"start": v(149.88, -42.3) * mm, "end": v(149.88, -43.3) * mm});
            skLineSegment(sketch, "E1128", {"start": v(111.77, -42.3) * mm, "end": v(111.77, -43.3) * mm});
            skLineSegment(sketch, "E1129", {"start": v(97.78, -42.3) * mm, "end": v(97.78, -43.3) * mm});
            skLineSegment(sketch, "E1130", {"start": v(92.73, -42.3) * mm, "end": v(92.73, -43.3) * mm});
            skLineSegment(sketch, "E1131", {"start": v(40.62, -42.3) * mm, "end": v(40.62, -43.3) * mm});
            skLineSegment(sketch, "E1132", {"start": v(2.24, -23.25) * mm, "end": v(2.24, -24.25) * mm});
            skLineSegment(sketch, "E1133", {"start": v(-11.76, -23.25) * mm, "end": v(-11.76, -24.25) * mm});
            skLineSegment(sketch, "E1134", {"start": v(-16.81, -23.25) * mm, "end": v(-16.81, -24.25) * mm});
            skLineSegment(sketch, "E1135", {"start": v(-30.81, -23.25) * mm, "end": v(-30.81, -24.25) * mm});
            skLineSegment(sketch, "E1136", {"start": v(21.29, -23.25) * mm, "end": v(21.29, -24.25) * mm});
            skLineSegment(sketch, "E1137", {"start": v(7.29, -23.25) * mm, "end": v(7.29, -24.25) * mm});
            skLineSegment(sketch, "E1138", {"start": v(59.39, -23.25) * mm, "end": v(59.39, -24.25) * mm});
            skLineSegment(sketch, "E1139", {"start": v(45.39, -23.25) * mm, "end": v(45.39, -24.25) * mm});
            skLineSegment(sketch, "E1140", {"start": v(40.34, -23.25) * mm, "end": v(40.34, -24.25) * mm});
            skLineSegment(sketch, "E1141", {"start": v(26.34, -23.25) * mm, "end": v(26.34, -24.25) * mm});
            skLineSegment(sketch, "E1142", {"start": v(90.63, -23.25) * mm, "end": v(90.63, -24.25) * mm});
            skLineSegment(sketch, "E1143", {"start": v(104.63, -23.25) * mm, "end": v(104.63, -24.25) * mm});
            skLineSegment(sketch, "E1144", {"start": v(78.44, -23.25) * mm, "end": v(78.44, -24.25) * mm});
            skLineSegment(sketch, "E1145", {"start": v(64.44, -23.25) * mm, "end": v(64.44, -24.25) * mm});
            skLineSegment(sketch, "E1146", {"start": v(116.82, -23.25) * mm, "end": v(116.82, -24.25) * mm});
            skLineSegment(sketch, "E1147", {"start": v(130.82, -23.25) * mm, "end": v(130.82, -24.25) * mm});
            skLineSegment(sketch, "E1148", {"start": v(-133.5, -42.3) * mm, "end": v(-133.5, -43.3) * mm});
            skLineSegment(sketch, "E1149", {"start": v(-147.5, -42.3) * mm, "end": v(-147.5, -43.3) * mm});
            skLineSegment(sketch, "E1150", {"start": v(149.88, -23.25) * mm, "end": v(149.88, -24.25) * mm});
            skLineSegment(sketch, "E1151", {"start": v(135.88, -23.25) * mm, "end": v(135.88, -24.25) * mm});
            skLineSegment(sketch, "E1152", {"start": v(-123.68, -42.3) * mm, "end": v(-123.68, -43.3) * mm});
            skLineSegment(sketch, "E1153", {"start": v(-109.68, -42.3) * mm, "end": v(-109.68, -43.3) * mm});
            skLineSegment(sketch, "E1154", {"start": v(-99.87, -42.3) * mm, "end": v(-99.87, -43.3) * mm});
            skLineSegment(sketch, "E1155", {"start": v(-85.87, -42.3) * mm, "end": v(-85.87, -43.3) * mm});
            skLineSegment(sketch, "E1156", {"start": v(11.76, -4.2) * mm, "end": v(11.76, -5.2) * mm});
            skLineSegment(sketch, "E1157", {"start": v(-2.24, -4.2) * mm, "end": v(-2.24, -5.2) * mm});
            skLineSegment(sketch, "E1158", {"start": v(-7.29, -4.2) * mm, "end": v(-7.29, -5.2) * mm});
            skLineSegment(sketch, "E1159", {"start": v(-21.29, -4.2) * mm, "end": v(-21.29, -5.2) * mm});
            skLineSegment(sketch, "E1160", {"start": v(49.86, -4.2) * mm, "end": v(49.86, -5.2) * mm});
            skLineSegment(sketch, "E1161", {"start": v(35.86, -4.2) * mm, "end": v(35.86, -5.2) * mm});
            skLineSegment(sketch, "E1162", {"start": v(30.81, -4.2) * mm, "end": v(30.81, -5.2) * mm});
            skLineSegment(sketch, "E1163", {"start": v(16.81, -4.2) * mm, "end": v(16.81, -5.2) * mm});
            skLineSegment(sketch, "E1164", {"start": v(68.91, -4.2) * mm, "end": v(68.91, -5.2) * mm});
            skLineSegment(sketch, "E1165", {"start": v(54.91, -4.2) * mm, "end": v(54.91, -5.2) * mm});
            skLineSegment(sketch, "E1166", {"start": v(87.96, -4.2) * mm, "end": v(87.96, -5.2) * mm});
            skLineSegment(sketch, "E1167", {"start": v(73.96, -4.2) * mm, "end": v(73.96, -5.2) * mm});
            skLineSegment(sketch, "E1168", {"start": v(135.88, -4.2) * mm, "end": v(135.88, -5.2) * mm});
            skLineSegment(sketch, "E1169", {"start": v(149.88, -4.2) * mm, "end": v(149.88, -5.2) * mm});
            skLineSegment(sketch, "E1170", {"start": v(-107.01, -23.25) * mm, "end": v(-107.01, -24.25) * mm});
            skLineSegment(sketch, "E1171", {"start": v(-93.01, -23.25) * mm, "end": v(-93.01, -24.25) * mm});
            skLineSegment(sketch, "E1172", {"start": v(-54.91, -23.25) * mm, "end": v(-54.91, -24.25) * mm});
            skLineSegment(sketch, "E1173", {"start": v(-68.91, -23.25) * mm, "end": v(-68.91, -24.25) * mm});
            skLineSegment(sketch, "E1174", {"start": v(-73.96, -23.25) * mm, "end": v(-73.96, -24.25) * mm});
            skLineSegment(sketch, "E1175", {"start": v(-87.96, -23.25) * mm, "end": v(-87.96, -24.25) * mm});
            skLineSegment(sketch, "E1176", {"start": v(-35.86, -23.25) * mm, "end": v(-35.86, -24.25) * mm});
            skLineSegment(sketch, "E1177", {"start": v(-49.86, -23.25) * mm, "end": v(-49.86, -24.25) * mm});
            skLineSegment(sketch, "E1178", {"start": v(126.06, 13.85) * mm, "end": v(112.06, 13.85) * mm});
            skLineSegment(sketch, "E1179", {"start": v(-128.73, -5.2) * mm, "end": v(-142.73, -5.2) * mm});
            skLineSegment(sketch, "E1180", {"start": v(-83.49, -5.2) * mm, "end": v(-97.49, -5.2) * mm});
            skLineSegment(sketch, "E1181", {"start": v(-102.54, -5.2) * mm, "end": v(-116.54, -5.2) * mm});
            skLineSegment(sketch, "E1182", {"start": v(-45.39, -5.2) * mm, "end": v(-59.39, -5.2) * mm});
            skLineSegment(sketch, "E1183", {"start": v(-64.44, -5.2) * mm, "end": v(-78.44, -5.2) * mm});
            skLineSegment(sketch, "E1184", {"start": v(-26.34, -5.2) * mm, "end": v(-40.34, -5.2) * mm});
            skLineSegment(sketch, "E1185", {"start": v(7, 13.85) * mm, "end": v(-7, 13.85) * mm});
            skLineSegment(sketch, "E1186", {"start": v(45.1, 13.85) * mm, "end": v(31.1, 13.85) * mm});
            skLineSegment(sketch, "E1187", {"start": v(26.05, 13.85) * mm, "end": v(12.05, 13.85) * mm});
            skLineSegment(sketch, "E1188", {"start": v(64.15, 13.85) * mm, "end": v(50.15, 13.85) * mm});
            skLineSegment(sketch, "E1189", {"start": v(102.25, 13.85) * mm, "end": v(88.25, 13.85) * mm});
            skLineSegment(sketch, "E1190", {"start": v(83.2, 13.85) * mm, "end": v(69.2, 13.85) * mm});
            skLineSegment(sketch, "E1191", {"start": v(73.68, 32.9) * mm, "end": v(59.68, 32.9) * mm});
            skLineSegment(sketch, "E1192", {"start": v(54.62, 32.9) * mm, "end": v(40.62, 32.9) * mm});
            skLineSegment(sketch, "E1193", {"start": v(92.73, 32.9) * mm, "end": v(78.72, 32.9) * mm});
            skLineSegment(sketch, "E1194", {"start": v(135.88, 32.9) * mm, "end": v(149.88, 32.9) * mm});
            skLineSegment(sketch, "E1195", {"start": v(-107.3, 13.85) * mm, "end": v(-121.3, 13.85) * mm});
            skLineSegment(sketch, "E1196", {"start": v(-131.11, 13.85) * mm, "end": v(-145.11, 13.85) * mm});
            skLineSegment(sketch, "E1197", {"start": v(-88.25, 13.85) * mm, "end": v(-102.25, 13.85) * mm});
            skLineSegment(sketch, "E1198", {"start": v(-50.15, 13.85) * mm, "end": v(-64.15, 13.85) * mm});
            skLineSegment(sketch, "E1199", {"start": v(-69.2, 13.85) * mm, "end": v(-83.2, 13.85) * mm});
            skLineSegment(sketch, "E1200", {"start": v(-12.05, 13.85) * mm, "end": v(-26.05, 13.85) * mm});
            skLineSegment(sketch, "E1201", {"start": v(-31.1, 13.85) * mm, "end": v(-45.1, 13.85) * mm});
            skLineSegment(sketch, "E1202", {"start": v(-135.88, 32.9) * mm, "end": v(-149.88, 32.9) * mm});
            skLineSegment(sketch, "E1203", {"start": v(-116.83, 32.9) * mm, "end": v(-130.82, 32.9) * mm});
            skLineSegment(sketch, "E1204", {"start": v(-78.72, 32.9) * mm, "end": v(-92.73, 32.9) * mm});
            skLineSegment(sketch, "E1205", {"start": v(-97.78, 32.9) * mm, "end": v(-111.78, 32.9) * mm});
            skLineSegment(sketch, "E1206", {"start": v(-59.67, 32.9) * mm, "end": v(-73.68, 32.9) * mm});
            skLineSegment(sketch, "E1207", {"start": v(-21.57, 32.9) * mm, "end": v(-35.58, 32.9) * mm});
            skLineSegment(sketch, "E1208", {"start": v(-40.62, 32.9) * mm, "end": v(-54.62, 32.9) * mm});
            skLineSegment(sketch, "E1209", {"start": v(-2.53, 32.9) * mm, "end": v(-16.53, 32.9) * mm});
            skLineSegment(sketch, "E1210", {"start": v(35.57, 32.9) * mm, "end": v(21.57, 32.9) * mm});
            skLineSegment(sketch, "E1211", {"start": v(16.53, 32.9) * mm, "end": v(2.53, 32.9) * mm});
            skLineSegment(sketch, "E1212", {"start": v(135.88, -43.3) * mm, "end": v(149.88, -43.3) * mm});
            skLineSegment(sketch, "E1213", {"start": v(97.78, -43.3) * mm, "end": v(111.77, -43.3) * mm});
            skLineSegment(sketch, "E1214", {"start": v(116.82, -43.3) * mm, "end": v(130.82, -43.3) * mm});
            skLineSegment(sketch, "E1215", {"start": v(2.24, -24.25) * mm, "end": v(-11.76, -24.25) * mm});
            skLineSegment(sketch, "E1216", {"start": v(-16.81, -24.25) * mm, "end": v(-30.81, -24.25) * mm});
            skLineSegment(sketch, "E1217", {"start": v(21.29, -24.25) * mm, "end": v(7.29, -24.25) * mm});
            skLineSegment(sketch, "E1218", {"start": v(59.39, -24.25) * mm, "end": v(45.39, -24.25) * mm});
            skLineSegment(sketch, "E1219", {"start": v(40.34, -24.25) * mm, "end": v(26.34, -24.25) * mm});
            skLineSegment(sketch, "E1220", {"start": v(78.44, -24.25) * mm, "end": v(64.44, -24.25) * mm});
            skLineSegment(sketch, "E1221", {"start": v(116.82, -24.25) * mm, "end": v(130.82, -24.25) * mm});
            skLineSegment(sketch, "E1222", {"start": v(104.63, -24.25) * mm, "end": v(90.63, -24.25) * mm});
            skLineSegment(sketch, "E1223", {"start": v(-133.5, -43.3) * mm, "end": v(-147.5, -43.3) * mm});
            skLineSegment(sketch, "E1224", {"start": v(135.88, -24.25) * mm, "end": v(149.88, -24.25) * mm});
            skLineSegment(sketch, "E1225", {"start": v(-109.68, -43.3) * mm, "end": v(-123.68, -43.3) * mm});
            skLineSegment(sketch, "E1226", {"start": v(-14.43, -43.3) * mm, "end": v(-28.43, -43.3) * mm});
            skLineSegment(sketch, "E1227", {"start": v(-85.87, -43.3) * mm, "end": v(-99.87, -43.3) * mm});
            skLineSegment(sketch, "E1228", {"start": v(11.76, -5.2) * mm, "end": v(-2.24, -5.2) * mm});
            skLineSegment(sketch, "E1229", {"start": v(-7.29, -5.2) * mm, "end": v(-21.29, -5.2) * mm});
            skLineSegment(sketch, "E1230", {"start": v(30.81, -5.2) * mm, "end": v(16.81, -5.2) * mm});
            skLineSegment(sketch, "E1231", {"start": v(68.91, -5.2) * mm, "end": v(54.91, -5.2) * mm});
            skLineSegment(sketch, "E1232", {"start": v(49.86, -5.2) * mm, "end": v(35.86, -5.2) * mm});
            skLineSegment(sketch, "E1233", {"start": v(87.96, -5.2) * mm, "end": v(73.96, -5.2) * mm});
            skLineSegment(sketch, "E1234", {"start": v(135.88, -5.2) * mm, "end": v(149.88, -5.2) * mm});
            skLineSegment(sketch, "E1235", {"start": v(-93.01, -24.25) * mm, "end": v(-107.01, -24.25) * mm});
            skLineSegment(sketch, "E1236", {"start": v(-73.96, -24.25) * mm, "end": v(-87.96, -24.25) * mm});
            skLineSegment(sketch, "E1237", {"start": v(-35.86, -24.25) * mm, "end": v(-49.86, -24.25) * mm});
            skLineSegment(sketch, "E1238", {"start": v(-54.91, -24.25) * mm, "end": v(-68.91, -24.25) * mm});
            skLineSegment(sketch, "E1239", {"start": v(135.88, 13.85) * mm, "end": v(149.88, 13.85) * mm});
            skLineSegment(sketch, "E1240", {"start": v(-137.97, -10.25) * mm, "end": v(-123.97, -10.25) * mm});
            skLineSegment(sketch, "E1241", {"start": v(107.3, 46.9) * mm, "end": v(121.3, 46.9) * mm});
            skLineSegment(sketch, "E1242", {"start": v(104.92, 8.8) * mm, "end": v(118.92, 8.8) * mm});
            skLineSegment(sketch, "E1243", {"start": v(-137.97, -24.25) * mm, "end": v(-123.97, -24.25) * mm});
            skLineSegment(sketch, "E1244", {"start": v(107.3, 32.9) * mm, "end": v(121.3, 32.9) * mm});
            skLineSegment(sketch, "E1245", {"start": v(104.92, -5.2) * mm, "end": v(118.92, -5.2) * mm});
            skLineSegment(sketch, "E1246", {"start": v(-147.07, -17.75) * mm, "end": v(-147.07, -14.95) * mm});
            skLineSegment(sketch, "E1247", {"start": v(98.2, 39.4) * mm, "end": v(98.2, 42.2) * mm});
            skLineSegment(sketch, "E1248", {"start": v(95.82, 1.3) * mm, "end": v(95.82, 4.1) * mm});
            skLineSegment(sketch, "E1249", {"start": v(-114.87, -17.75) * mm, "end": v(-114.87, -14.95) * mm});
            skLineSegment(sketch, "E1250", {"start": v(130.4, 39.4) * mm, "end": v(130.4, 42.2) * mm});
            skLineSegment(sketch, "E1251", {"start": v(128.02, 1.3) * mm, "end": v(128.02, 4.1) * mm});
            skLineSegment(sketch, "E1252", {"start": v(-139.54, -11.72) * mm, "end": v(-146.2, -11.72) * mm});
            skLineSegment(sketch, "E1253", {"start": v(105.72, 45.43) * mm, "end": v(99.08, 45.43) * mm});
            skLineSegment(sketch, "E1254", {"start": v(103.34, 7.33) * mm, "end": v(96.7, 7.33) * mm});
            skLineSegment(sketch, "E1255", {"start": v(-122.4, -11.72) * mm, "end": v(-115.74, -11.72) * mm});
            skLineSegment(sketch, "E1256", {"start": v(122.88, 45.43) * mm, "end": v(129.52, 45.43) * mm});
            skLineSegment(sketch, "E1257", {"start": v(120.5, 7.33) * mm, "end": v(127.14, 7.33) * mm});
            skLineSegment(sketch, "E1258", {"start": v(-147.07, -17.75) * mm, "end": v(-146.2, -17.75) * mm});
            skLineSegment(sketch, "E1259", {"start": v(98.2, 39.4) * mm, "end": v(99.08, 39.4) * mm});
            skLineSegment(sketch, "E1260", {"start": v(95.82, 1.3) * mm, "end": v(96.7, 1.3) * mm});
            skLineSegment(sketch, "E1261", {"start": v(-114.87, -17.75) * mm, "end": v(-115.74, -17.75) * mm});
            skLineSegment(sketch, "E1262", {"start": v(130.4, 39.4) * mm, "end": v(129.52, 39.4) * mm});
            skLineSegment(sketch, "E1263", {"start": v(128.02, 1.3) * mm, "end": v(127.14, 1.3) * mm});
            skLineSegment(sketch, "E1264", {"start": v(-147.07, -14.95) * mm, "end": v(-146.2, -14.95) * mm});
            skLineSegment(sketch, "E1265", {"start": v(98.2, 42.2) * mm, "end": v(99.08, 42.2) * mm});
            skLineSegment(sketch, "E1266", {"start": v(95.82, 4.1) * mm, "end": v(96.7, 4.1) * mm});
            skLineSegment(sketch, "E1267", {"start": v(-114.87, -14.95) * mm, "end": v(-115.74, -14.95) * mm});
            skLineSegment(sketch, "E1268", {"start": v(130.4, 42.2) * mm, "end": v(129.52, 42.2) * mm});
            skLineSegment(sketch, "E1269", {"start": v(128.02, 4.1) * mm, "end": v(127.14, 4.1) * mm});
            skLineSegment(sketch, "E1270", {"start": v(-146.2, -14.95) * mm, "end": v(-146.2, -11.72) * mm});
            skLineSegment(sketch, "E1271", {"start": v(99.08, 42.2) * mm, "end": v(99.08, 45.43) * mm});
            skLineSegment(sketch, "E1272", {"start": v(96.7, 4.1) * mm, "end": v(96.7, 7.33) * mm});
            skLineSegment(sketch, "E1273", {"start": v(-115.74, -14.95) * mm, "end": v(-115.74, -11.72) * mm});
            skLineSegment(sketch, "E1274", {"start": v(129.52, 42.2) * mm, "end": v(129.52, 45.43) * mm});
            skLineSegment(sketch, "E1275", {"start": v(127.14, 4.1) * mm, "end": v(127.14, 7.33) * mm});
            skLineSegment(sketch, "E1276", {"start": v(-139.54, -12.52) * mm, "end": v(-139.54, -11.72) * mm});
            skLineSegment(sketch, "E1277", {"start": v(105.72, 44.63) * mm, "end": v(105.72, 45.43) * mm});
            skLineSegment(sketch, "E1278", {"start": v(103.34, 6.53) * mm, "end": v(103.34, 7.33) * mm});
            skLineSegment(sketch, "E1279", {"start": v(-122.4, -12.52) * mm, "end": v(-122.4, -11.72) * mm});
            skLineSegment(sketch, "E1280", {"start": v(122.88, 44.63) * mm, "end": v(122.88, 45.43) * mm});
            skLineSegment(sketch, "E1281", {"start": v(120.5, 6.53) * mm, "end": v(120.5, 7.33) * mm});
            skLineSegment(sketch, "E1282", {"start": v(-137.97, -10.25) * mm, "end": v(-137.97, -12.52) * mm});
            skLineSegment(sketch, "E1283", {"start": v(107.3, 46.9) * mm, "end": v(107.3, 44.63) * mm});
            skLineSegment(sketch, "E1284", {"start": v(104.92, 8.8) * mm, "end": v(104.92, 6.53) * mm});
            skLineSegment(sketch, "E1285", {"start": v(-123.97, -10.25) * mm, "end": v(-123.97, -12.52) * mm});
            skLineSegment(sketch, "E1286", {"start": v(121.3, 46.9) * mm, "end": v(121.3, 44.63) * mm});
            skLineSegment(sketch, "E1287", {"start": v(118.92, 8.8) * mm, "end": v(118.92, 6.53) * mm});
            skLineSegment(sketch, "E1288", {"start": v(-139.54, -12.52) * mm, "end": v(-137.97, -12.52) * mm});
            skLineSegment(sketch, "E1289", {"start": v(105.72, 44.63) * mm, "end": v(107.3, 44.63) * mm});
            skLineSegment(sketch, "E1290", {"start": v(103.34, 6.53) * mm, "end": v(104.92, 6.53) * mm});
            skLineSegment(sketch, "E1291", {"start": v(-122.4, -12.52) * mm, "end": v(-123.97, -12.52) * mm});
            skLineSegment(sketch, "E1292", {"start": v(122.88, 44.63) * mm, "end": v(121.3, 44.63) * mm});
            skLineSegment(sketch, "E1293", {"start": v(120.5, 6.53) * mm, "end": v(118.92, 6.53) * mm});
            skLineSegment(sketch, "E1294", {"start": v(-141.37, -25.22) * mm, "end": v(-144.37, -25.22) * mm});
            skLineSegment(sketch, "E1295", {"start": v(103.9, 31.93) * mm, "end": v(100.9, 31.93) * mm});
            skLineSegment(sketch, "E1296", {"start": v(101.52, -6.17) * mm, "end": v(98.52, -6.17) * mm});
            skLineSegment(sketch, "E1297", {"start": v(-120.57, -25.22) * mm, "end": v(-117.57, -25.22) * mm});
            skLineSegment(sketch, "E1298", {"start": v(124.7, 31.93) * mm, "end": v(127.7, 31.93) * mm});
            skLineSegment(sketch, "E1299", {"start": v(122.32, -6.17) * mm, "end": v(125.32, -6.17) * mm});
            skLineSegment(sketch, "E1300", {"start": v(-146.2, -17.75) * mm, "end": v(-146.2, -24.02) * mm});
            skLineSegment(sketch, "E1301", {"start": v(99.08, 39.4) * mm, "end": v(99.08, 33.13) * mm});
            skLineSegment(sketch, "E1302", {"start": v(96.7, 1.3) * mm, "end": v(96.7, -4.97) * mm});
            skLineSegment(sketch, "E1303", {"start": v(-115.74, -17.75) * mm, "end": v(-115.74, -24.02) * mm});
            skLineSegment(sketch, "E1304", {"start": v(129.52, 39.4) * mm, "end": v(129.52, 33.13) * mm});
            skLineSegment(sketch, "E1305", {"start": v(127.14, 1.3) * mm, "end": v(127.14, -4.97) * mm});
            skLineSegment(sketch, "E1306", {"start": v(-146.2, -24.02) * mm, "end": v(-144.37, -24.02) * mm});
            skLineSegment(sketch, "E1307", {"start": v(99.08, 33.13) * mm, "end": v(100.9, 33.13) * mm});
            skLineSegment(sketch, "E1308", {"start": v(96.7, -4.97) * mm, "end": v(98.52, -4.97) * mm});
            skLineSegment(sketch, "E1309", {"start": v(-115.74, -24.02) * mm, "end": v(-117.57, -24.02) * mm});
            skLineSegment(sketch, "E1310", {"start": v(129.52, 33.13) * mm, "end": v(127.7, 33.13) * mm});
            skLineSegment(sketch, "E1311", {"start": v(127.14, -4.97) * mm, "end": v(125.32, -4.97) * mm});
            skLineSegment(sketch, "E1312", {"start": v(-117.57, -25.22) * mm, "end": v(-117.57, -24.02) * mm});
            skLineSegment(sketch, "E1313", {"start": v(127.7, 31.93) * mm, "end": v(127.7, 33.13) * mm});
            skLineSegment(sketch, "E1314", {"start": v(125.32, -6.17) * mm, "end": v(125.32, -4.97) * mm});
            skLineSegment(sketch, "E1315", {"start": v(-144.37, -25.22) * mm, "end": v(-144.37, -24.02) * mm});
            skLineSegment(sketch, "E1316", {"start": v(100.9, 31.93) * mm, "end": v(100.9, 33.13) * mm});
            skLineSegment(sketch, "E1317", {"start": v(98.52, -6.17) * mm, "end": v(98.52, -4.97) * mm});
            skLineSegment(sketch, "E1318", {"start": v(-141.37, -25.22) * mm, "end": v(-141.37, -24.02) * mm});
            skLineSegment(sketch, "E1319", {"start": v(103.9, 31.93) * mm, "end": v(103.9, 33.13) * mm});
            skLineSegment(sketch, "E1320", {"start": v(101.52, -6.17) * mm, "end": v(101.52, -4.97) * mm});
            skLineSegment(sketch, "E1321", {"start": v(-120.57, -25.22) * mm, "end": v(-120.57, -24.02) * mm});
            skLineSegment(sketch, "E1322", {"start": v(124.7, 31.93) * mm, "end": v(124.7, 33.13) * mm});
            skLineSegment(sketch, "E1323", {"start": v(122.32, -6.17) * mm, "end": v(122.32, -4.97) * mm});
            skLineSegment(sketch, "E1324", {"start": v(-141.37, -24.02) * mm, "end": v(-139.54, -24.02) * mm});
            skLineSegment(sketch, "E1325", {"start": v(103.9, 33.13) * mm, "end": v(105.72, 33.13) * mm});
            skLineSegment(sketch, "E1326", {"start": v(101.52, -4.97) * mm, "end": v(103.34, -4.97) * mm});
            skLineSegment(sketch, "E1327", {"start": v(-120.57, -24.02) * mm, "end": v(-122.4, -24.02) * mm});
            skLineSegment(sketch, "E1328", {"start": v(124.7, 33.13) * mm, "end": v(122.88, 33.13) * mm});
            skLineSegment(sketch, "E1329", {"start": v(122.32, -4.97) * mm, "end": v(120.5, -4.97) * mm});
            skLineSegment(sketch, "E1330", {"start": v(-139.54, -24.02) * mm, "end": v(-139.54, -23.22) * mm});
            skLineSegment(sketch, "E1331", {"start": v(105.72, 33.13) * mm, "end": v(105.72, 33.93) * mm});
            skLineSegment(sketch, "E1332", {"start": v(103.34, -4.97) * mm, "end": v(103.34, -4.17) * mm});
            skLineSegment(sketch, "E1333", {"start": v(-122.4, -24.02) * mm, "end": v(-122.4, -23.22) * mm});
            skLineSegment(sketch, "E1334", {"start": v(122.88, 33.13) * mm, "end": v(122.88, 33.93) * mm});
            skLineSegment(sketch, "E1335", {"start": v(120.5, -4.97) * mm, "end": v(120.5, -4.17) * mm});
            skLineSegment(sketch, "E1336", {"start": v(-139.54, -23.22) * mm, "end": v(-137.97, -23.22) * mm});
            skLineSegment(sketch, "E1337", {"start": v(105.72, 33.93) * mm, "end": v(107.3, 33.93) * mm});
            skLineSegment(sketch, "E1338", {"start": v(103.34, -4.17) * mm, "end": v(104.92, -4.17) * mm});
            skLineSegment(sketch, "E1339", {"start": v(-122.4, -23.22) * mm, "end": v(-123.97, -23.22) * mm});
            skLineSegment(sketch, "E1340", {"start": v(122.88, 33.93) * mm, "end": v(121.3, 33.93) * mm});
            skLineSegment(sketch, "E1341", {"start": v(120.5, -4.17) * mm, "end": v(118.92, -4.17) * mm});
            skLineSegment(sketch, "E1342", {"start": v(-137.97, -24.25) * mm, "end": v(-137.97, -23.22) * mm});
            skLineSegment(sketch, "E1343", {"start": v(107.3, 32.9) * mm, "end": v(107.3, 33.93) * mm});
            skLineSegment(sketch, "E1344", {"start": v(104.92, -5.2) * mm, "end": v(104.92, -4.17) * mm});
            skLineSegment(sketch, "E1345", {"start": v(-123.97, -24.25) * mm, "end": v(-123.97, -23.22) * mm});
            skLineSegment(sketch, "E1346", {"start": v(121.3, 32.9) * mm, "end": v(121.3, 33.93) * mm});
            skLineSegment(sketch, "E1347", {"start": v(118.92, -5.2) * mm, "end": v(118.92, -4.17) * mm});
            skLineSegment(sketch, "E1348", {"start": v(30.07, -44.07) * mm, "end": v(27.07, -44.07) * mm});
            skLineSegment(sketch, "E1349", {"start": v(-72.93, -44.07) * mm, "end": v(-69.93, -44.07) * mm});
            skLineSegment(sketch, "E1350", {"start": v(27.07, -44.07) * mm, "end": v(27.07, -43.07) * mm});
            skLineSegment(sketch, "E1351", {"start": v(-69.93, -44.07) * mm, "end": v(-69.93, -43.07) * mm});
            skLineSegment(sketch, "E1352", {"start": v(30.07, -44.07) * mm, "end": v(30.07, -43.07) * mm});
            skLineSegment(sketch, "E1353", {"start": v(-72.93, -44.07) * mm, "end": v(-72.93, -43.07) * mm});
            skLineSegment(sketch, "E1354", {"start": v(30.07, -43.07) * mm, "end": v(31.9, -43.07) * mm});
            skLineSegment(sketch, "E1355", {"start": v(-72.93, -43.07) * mm, "end": v(-74.76, -43.07) * mm});
            skLineSegment(sketch, "E1356", {"start": v(27.07, -43.07) * mm, "end": v(25.24, -43.07) * mm});
            skLineSegment(sketch, "E1357", {"start": v(-69.93, -43.07) * mm, "end": v(-68.1, -43.07) * mm});
            skLineSegment(sketch, "E1358", {"start": v(31.9, -43.07) * mm, "end": v(31.9, -36.8) * mm});
            skLineSegment(sketch, "E1359", {"start": v(-74.76, -43.07) * mm, "end": v(-74.76, -36.8) * mm});
            skLineSegment(sketch, "E1360", {"start": v(31.9, -36.8) * mm, "end": v(32.77, -36.8) * mm});
            skLineSegment(sketch, "E1361", {"start": v(31.9, -34) * mm, "end": v(32.77, -34) * mm});
            skLineSegment(sketch, "E1362", {"start": v(-74.76, -36.8) * mm, "end": v(-75.63, -36.8) * mm});
            skLineSegment(sketch, "E1363", {"start": v(-74.76, -34) * mm, "end": v(-75.63, -34) * mm});
            skLineSegment(sketch, "E1364", {"start": v(32.77, -36.8) * mm, "end": v(32.77, -34) * mm});
            skLineSegment(sketch, "E1365", {"start": v(-75.63, -36.8) * mm, "end": v(-75.63, -34) * mm});
            skLineSegment(sketch, "E1366", {"start": v(31.9, -34) * mm, "end": v(31.9, -30.57) * mm});
            skLineSegment(sketch, "E1367", {"start": v(-74.76, -34) * mm, "end": v(-74.76, -30.57) * mm});
            skLineSegment(sketch, "E1368", {"start": v(31.9, -30.57) * mm, "end": v(25.24, -30.57) * mm});
            skLineSegment(sketch, "E1369", {"start": v(-74.76, -30.57) * mm, "end": v(-68.1, -30.57) * mm});
            skLineSegment(sketch, "E1370", {"start": v(25.24, -30.57) * mm, "end": v(25.24, -34) * mm});
            skLineSegment(sketch, "E1371", {"start": v(-68.1, -30.57) * mm, "end": v(-68.1, -34) * mm});
            skLineSegment(sketch, "E1372", {"start": v(25.24, -43.07) * mm, "end": v(25.24, -38.6) * mm});
            skLineSegment(sketch, "E1373", {"start": v(-68.1, -43.07) * mm, "end": v(-68.1, -38.6) * mm});
            skLineSegment(sketch, "E1374", {"start": v(-14.43, -38.6) * mm, "end": v(-14.43, -43.3) * mm});
            skLineSegment(sketch, "E1375", {"start": v(-28.43, -38.6) * mm, "end": v(-28.43, -43.3) * mm});
            skLineSegment(sketch, "E1376", {"start": v(-14.43, -34) * mm, "end": v(-14.43, -29.3) * mm});
            skLineSegment(sketch, "E1377", {"start": v(-28.43, -34) * mm, "end": v(-28.43, -29.3) * mm});
            skLineSegment(sketch, "E1378", {"start": v(-68.1, -34) * mm, "end": v(-28.43, -34) * mm});
            skLineSegment(sketch, "E1379", {"start": v(-68.1, -38.6) * mm, "end": v(-28.43, -38.6) * mm});
            skLineSegment(sketch, "E1380", {"start": v(-14.43, -34) * mm, "end": v(25.24, -34) * mm});
            skLineSegment(sketch, "E1381", {"start": v(-14.43, -38.6) * mm, "end": v(25.24, -38.6) * mm});
            skLineSegment(sketch, "E1382", {"start": v(40.62, -29.3) * mm, "end": v(92.73, -29.3) * mm});
            skLineSegment(sketch, "E1383", {"start": v(40.62, -43.3) * mm, "end": v(92.73, -43.3) * mm});
            skLineSegment(sketch, "E1384.bottom", {"start": v(-149.88, 51.9) * mm, "end": v(149.88, 51.9) * mm});
            skLineSegment(sketch, "E1384.top", {"start": v(-149.88, -48.3) * mm, "end": v(149.88, -48.3) * mm});
            skLineSegment(sketch, "E1384.left", {"start": v(-154.88, 46.9) * mm, "end": v(-154.88, -43.3) * mm});
            skLineSegment(sketch, "E1384.right", {"start": v(154.88, 46.9) * mm, "end": v(154.88, -43.3) * mm});
            skPoint(sketch, "E1385.visualSharp", {"position": v(-154.88, 51.9) * mm});
            skArc(sketch, "E1385.filletArc", {"start": v(-149.88, 51.9) * mm, "mid": v(-153.41, 50.44) * mm, "end": v(-154.88, 46.9) * mm});
            skPoint(sketch, "E1386.visualSharp", {"position": v(154.88, 51.9) * mm});
            skArc(sketch, "E1386.filletArc", {"start": v(154.88, 46.9) * mm, "mid": v(153.41, 50.44) * mm, "end": v(149.88, 51.9) * mm});
            skPoint(sketch, "E1387.visualSharp", {"position": v(154.88, -48.3) * mm});
            skArc(sketch, "E1387.filletArc", {"start": v(149.88, -48.3) * mm, "mid": v(153.41, -46.84) * mm, "end": v(154.87, -43.3) * mm});
            skPoint(sketch, "E1388.visualSharp", {"position": v(-154.88, -48.3) * mm});
            skArc(sketch, "E1388.filletArc", {"start": v(-154.88, -43.3) * mm, "mid": v(-153.41, -46.84) * mm, "end": v(-149.88, -48.3) * mm});
            skSolve(sketch);
        }
        {
            var Q0;
            Q0=makeQuery(id+"F0.imprint","IMPRINT",FACE,{"disambiguationData":[TD([[makeQuery(id+"F0.imprint","IMPRINT",EDGE,{"derivedFrom":sQuery(id+"F0.wireOp",EDGE,"E0")}),1.0]])]});
            extrude(context, id + "F1", {"entities" : qUnion([Q0]), "depth" : 1.5 * mm});
        }
        {
            var Q0;
            Q0=qCreatedBy(makeId("Top.planeOp"),FACE);
            var sketch = newSketch(context, id + "F2", { "sketchPlane" : qUnion([Q0])});
            skLineSegment(sketch, "E1389.0", {"start": v(-149.88, 51.9) * mm, "end": v(149.88, 51.9) * mm});
            skPoint(sketch, "E1390.0", {"position": v(-153.41, 50.44) * mm});
            skLineSegment(sketch, "E1391.0", {"start": v(-154.88, 46.9) * mm, "end": v(-154.88, -43.3) * mm});
            skArc(sketch, "E1392.0", {"start": v(-154.88, -43.3) * mm, "mid": v(-153.41, -46.84) * mm, "end": v(-149.88, -48.3) * mm});
            skLineSegment(sketch, "E1393.0", {"start": v(-149.88, -48.3) * mm, "end": v(149.88, -48.3) * mm});
            skArc(sketch, "E1394.0", {"start": v(149.88, -48.3) * mm, "mid": v(153.41, -46.84) * mm, "end": v(154.87, -43.3) * mm});
            skLineSegment(sketch, "E1395.0", {"start": v(154.88, 46.9) * mm, "end": v(154.88, -43.3) * mm});
            skArc(sketch, "E1396.0", {"start": v(154.88, 46.9) * mm, "mid": v(153.41, 50.44) * mm, "end": v(149.88, 51.9) * mm});
            skArc(sketch, "E1397.0", {"start": v(-149.88, 51.9) * mm, "mid": v(-153.41, 50.44) * mm, "end": v(-154.88, 46.9) * mm});
            skArc(sketch, "E1398.0", {"start": v(-149.88, 59.9) * mm, "mid": v(-159.07, 56.1) * mm, "end": v(-162.88, 46.9) * mm});
            skLineSegment(sketch, "E1398.1", {"start": v(-162.88, 46.9) * mm, "end": v(-162.88, -43.3) * mm});
            skLineSegment(sketch, "E1398.2", {"start": v(-149.88, 59.9) * mm, "end": v(149.87, 59.9) * mm});
            skArc(sketch, "E1398.3", {"start": v(-162.88, -43.3) * mm, "mid": v(-159.07, -52.5) * mm, "end": v(-149.87, -56.3) * mm});
            skArc(sketch, "E1398.4", {"start": v(162.88, 46.9) * mm, "mid": v(159.07, 56.1) * mm, "end": v(149.87, 59.9) * mm});
            skLineSegment(sketch, "E1398.5", {"start": v(162.88, 46.9) * mm, "end": v(162.88, -43.3) * mm});
            skArc(sketch, "E1398.6", {"start": v(149.87, -56.3) * mm, "mid": v(159.07, -52.5) * mm, "end": v(162.88, -43.3) * mm});
            skLineSegment(sketch, "E1398.7", {"start": v(-149.87, -56.3) * mm, "end": v(149.87, -56.3) * mm});
            skArc(sketch, "E1399.0", {"start": v(-149.88, 49.9) * mm, "mid": v(-152, 49.02) * mm, "end": v(-152.88, 46.9) * mm});
            skLineSegment(sketch, "E1399.1", {"start": v(-149.88, 49.9) * mm, "end": v(149.87, 49.9) * mm});
            skLineSegment(sketch, "E1399.2", {"start": v(-152.88, 46.9) * mm, "end": v(-152.88, -43.3) * mm});
            skArc(sketch, "E1399.3", {"start": v(152.88, 46.9) * mm, "mid": v(152, 49.02) * mm, "end": v(149.87, 49.9) * mm});
            skArc(sketch, "E1399.4", {"start": v(-152.88, -43.3) * mm, "mid": v(-152, -45.42) * mm, "end": v(-149.87, -46.3) * mm});
            skLineSegment(sketch, "E1399.5", {"start": v(-149.87, -46.3) * mm, "end": v(149.87, -46.3) * mm});
            skArc(sketch, "E1399.6", {"start": v(149.87, -46.3) * mm, "mid": v(152, -45.42) * mm, "end": v(152.87, -43.3) * mm});
            skLineSegment(sketch, "E1399.7", {"start": v(152.88, 46.9) * mm, "end": v(152.88, -43.3) * mm});
            skSolve(sketch);
        }
        {
            var Q0;
            Q0=makeQuery(id+"F2.imprint","IMPRINT",FACE,{"disambiguationData":[TD([[makeQuery(id+"F2.imprint","IMPRINT",EDGE,{"derivedFrom":sQuery(id+"F2.wireOp",EDGE,"E1389.0")}),-1.0]])]});
            var Q1;
            Q1=makeQuery(id+"F2.imprint","IMPRINT",FACE,{"disambiguationData":[TD([[makeQuery(id+"F2.imprint","IMPRINT",EDGE,{"derivedFrom":sQuery(id+"F2.wireOp",EDGE,"E1389.0")}),1.0]])]});
            extrude(context, id + "F3", {"entities" : qUnion([Q0, Q1]), "oppositeDirection" : true, "depth" : 18 * mm});
        }
        {
            var Q0;
            Q0=makeQuery(id+"F2.imprint","IMPRINT",FACE,{"disambiguationData":[TD([[makeQuery(id+"F2.imprint","IMPRINT",EDGE,{"derivedFrom":sQuery(id+"F2.wireOp",EDGE,"E1389.0")}),1.0]])]});
            extrude(context, id + "F4", {"entities" : qUnion([Q0]), "operationType" : NewBodyOperationType.ADD, "depth" : 5 * mm});
        }
        {
            var Q0;
            Q0=makeQuery(id+"F4.opExtrude","CAP_EDGE",EDGE,{"disambiguationData":[OSD([sQuery(id+"F2.wireOp",EDGE,"E1398.1")])],"isStart":false});
            chamfer(context, id + "F5", {"entities" : qUnion([Q0]), "chamferType" : ChamferType.TWO_OFFSETS, "width1" : 8 * mm, "oppositeDirection" : false, "width2" : 5 * mm, "tangentPropagation" : true});
        }
        {
            var Q0;
            Q0=makeQuery(id+"F3.opExtrude","CAP_FACE",FACE,{"disambiguationData":[OSD([sQuery(id+"F2.wireOp",EDGE,"E1398.0"),sQuery(id+"F2.wireOp",EDGE,"E1398.1"),sQuery(id+"F2.wireOp",EDGE,"E1398.2"),sQuery(id+"F2.wireOp",EDGE,"E1398.3"),sQuery(id+"F2.wireOp",EDGE,"E1398.4"),sQuery(id+"F2.wireOp",EDGE,"E1398.5"),sQuery(id+"F2.wireOp",EDGE,"E1398.6"),sQuery(id+"F2.wireOp",EDGE,"E1398.7"),sQuery(id+"F2.wireOp",EDGE,"E1399.0"),sQuery(id+"F2.wireOp",EDGE,"E1399.1"),sQuery(id+"F2.wireOp",EDGE,"E1399.2"),sQuery(id+"F2.wireOp",EDGE,"E1399.3"),sQuery(id+"F2.wireOp",EDGE,"E1399.4"),sQuery(id+"F2.wireOp",EDGE,"E1399.5"),sQuery(id+"F2.wireOp",EDGE,"E1399.6"),sQuery(id+"F2.wireOp",EDGE,"E1399.7")])],"isStart":false});
            var sketch = newSketch(context, id + "F6", { "sketchPlane" : qUnion([Q0])});
            skArc(sketch, "E1400.0.0", {"start": v(-149.87, 56.3) * mm, "mid": v(-159.07, 52.5) * mm, "end": v(-162.88, 43.3) * mm});
            skLineSegment(sketch, "E1400.0.1", {"start": v(-162.88, 43.3) * mm, "end": v(-162.88, -46.9) * mm});
            skArc(sketch, "E1400.0.2", {"start": v(-162.88, -46.9) * mm, "mid": v(-159.07, -56.1) * mm, "end": v(-149.88, -59.9) * mm});
            skLineSegment(sketch, "E1400.0.3", {"start": v(-149.88, -59.9) * mm, "end": v(149.87, -59.9) * mm});
            skArc(sketch, "E1400.0.4", {"start": v(149.87, -59.9) * mm, "mid": v(159.07, -56.1) * mm, "end": v(162.88, -46.9) * mm});
            skLineSegment(sketch, "E1400.0.5", {"start": v(162.88, -46.9) * mm, "end": v(162.88, 43.3) * mm});
            skArc(sketch, "E1400.0.6", {"start": v(162.88, 43.3) * mm, "mid": v(159.07, 52.5) * mm, "end": v(149.87, 56.3) * mm});
            skLineSegment(sketch, "E1400.0.7", {"start": v(149.87, 56.3) * mm, "end": v(-149.87, 56.3) * mm});
            skLineSegment(sketch, "E1401.0", {"start": v(-150.88, -44.9) * mm, "end": v(-150.88, 41.3) * mm});
            skLineSegment(sketch, "E1401.1", {"start": v(-147.88, -47.9) * mm, "end": v(147.88, -47.9) * mm});
            skLineSegment(sketch, "E1401.2", {"start": v(150.88, -44.9) * mm, "end": v(150.88, 41.3) * mm});
            skLineSegment(sketch, "E1401.3", {"start": v(-147.88, 44.3) * mm, "end": v(147.88, 44.3) * mm});
            skPoint(sketch, "E1402.visualSharp", {"position": v(-150.88, 44.3) * mm});
            skArc(sketch, "E1402.filletArc", {"start": v(-147.88, 44.3) * mm, "mid": v(-150, 43.42) * mm, "end": v(-150.88, 41.3) * mm});
            skPoint(sketch, "E1403.visualSharp", {"position": v(150.88, 44.3) * mm});
            skArc(sketch, "E1403.filletArc", {"start": v(150.88, 41.3) * mm, "mid": v(150, 43.42) * mm, "end": v(147.88, 44.3) * mm});
            skPoint(sketch, "E1404.visualSharp", {"position": v(150.88, -47.9) * mm});
            skArc(sketch, "E1404.filletArc", {"start": v(147.88, -47.9) * mm, "mid": v(150, -47.02) * mm, "end": v(150.88, -44.9) * mm});
            skPoint(sketch, "E1405.visualSharp", {"position": v(-150.88, -47.9) * mm});
            skArc(sketch, "E1405.filletArc", {"start": v(-150.88, -44.9) * mm, "mid": v(-150, -47.02) * mm, "end": v(-147.88, -47.9) * mm});
            skSolve(sketch);
        }
        {
            var Q0;
            Q0=makeQuery(id+"F6.imprint","IMPRINT",FACE,{"disambiguationData":[TD([[makeQuery(id+"F6.imprint","IMPRINT",EDGE,{"derivedFrom":sQuery(id+"F6.wireOp",EDGE,"E1400.0.0")}),-1.0]])]});
            var Q1;
            Q1=makeQuery(id+"F6.imprint","IMPRINT",FACE,{"disambiguationData":[TD([[makeQuery(id+"F6.imprint","IMPRINT",EDGE,{"derivedFrom":sQuery(id+"F6.wireOp",EDGE,"E1401.0")}),1.0]])]});
            extrude(context, id + "F7", {"entities" : qUnion([Q0, Q1]), "depth" : 3.5 * mm});
        }
        {
            var Q0;
            Q0=makeQuery(id+"F7.opExtrude","CAP_FACE",FACE,{"disambiguationData":[OSD([sQuery(id+"F6.wireOp",EDGE,"E1400.0.0"),sQuery(id+"F6.wireOp",EDGE,"E1400.0.1"),sQuery(id+"F6.wireOp",EDGE,"E1400.0.2"),sQuery(id+"F6.wireOp",EDGE,"E1400.0.3"),sQuery(id+"F6.wireOp",EDGE,"E1400.0.4"),sQuery(id+"F6.wireOp",EDGE,"E1400.0.5"),sQuery(id+"F6.wireOp",EDGE,"E1400.0.6"),sQuery(id+"F6.wireOp",EDGE,"E1400.0.7"),sQuery(id+"F6.wireOp",EDGE,"E1401.0"),sQuery(id+"F6.wireOp",EDGE,"E1401.1"),sQuery(id+"F6.wireOp",EDGE,"E1401.2"),sQuery(id+"F6.wireOp",EDGE,"E1401.3"),sQuery(id+"F6.wireOp",EDGE,"E1402.filletArc"),sQuery(id+"F6.wireOp",EDGE,"E1403.filletArc"),sQuery(id+"F6.wireOp",EDGE,"E1404.filletArc"),sQuery(id+"F6.wireOp",EDGE,"E1405.filletArc")])],"isStart":true});
            var sketch = newSketch(context, id + "F8", { "sketchPlane" : qUnion([Q0])});
            skLineSegment(sketch, "E1406.0", {"start": v(-149.87, -46.3) * mm, "end": v(149.87, -46.3) * mm});
            skArc(sketch, "E1407.0", {"start": v(-152.88, -43.3) * mm, "mid": v(-152, -45.42) * mm, "end": v(-149.87, -46.3) * mm});
            skLineSegment(sketch, "E1408.0", {"start": v(-152.88, 46.9) * mm, "end": v(-152.88, -43.3) * mm});
            skArc(sketch, "E1409.0", {"start": v(-149.88, 49.9) * mm, "mid": v(-152, 49.02) * mm, "end": v(-152.88, 46.9) * mm});
            skLineSegment(sketch, "E1410.0", {"start": v(-149.88, 49.9) * mm, "end": v(149.87, 49.9) * mm});
            skArc(sketch, "E1411.0", {"start": v(149.87, -46.3) * mm, "mid": v(152, -45.42) * mm, "end": v(152.87, -43.3) * mm});
            skLineSegment(sketch, "E1412.0", {"start": v(152.88, 46.9) * mm, "end": v(152.88, -43.3) * mm});
            skArc(sketch, "E1413.0", {"start": v(152.88, 46.9) * mm, "mid": v(152, 49.02) * mm, "end": v(149.87, 49.9) * mm});
            skSolve(sketch);
        }
        {
            var Q0;
            Q0=makeQuery(id+"F8.imprint","IMPRINT",FACE,{"disambiguationData":[TD([[makeQuery(id+"F8.imprint","IMPRINT",EDGE,{"derivedFrom":makeQuery(id+"F7.opExtrude","CAP_EDGE",EDGE,{"disambiguationData":[OSD([sQuery(id+"F6.wireOp",EDGE,"E1401.0")])],"isStart":true})}),1.0]])]});
            var Q1;
            Q1=makeQuery(id+"F7.opExtrude","CAP_FACE",FACE,{"disambiguationData":[OSD([sQuery(id+"F6.wireOp",EDGE,"E1400.0.0"),sQuery(id+"F6.wireOp",EDGE,"E1400.0.1"),sQuery(id+"F6.wireOp",EDGE,"E1400.0.2"),sQuery(id+"F6.wireOp",EDGE,"E1400.0.3"),sQuery(id+"F6.wireOp",EDGE,"E1400.0.4"),sQuery(id+"F6.wireOp",EDGE,"E1400.0.5"),sQuery(id+"F6.wireOp",EDGE,"E1400.0.6"),sQuery(id+"F6.wireOp",EDGE,"E1400.0.7"),sQuery(id+"F6.wireOp",EDGE,"E1401.0"),sQuery(id+"F6.wireOp",EDGE,"E1401.1"),sQuery(id+"F6.wireOp",EDGE,"E1401.2"),sQuery(id+"F6.wireOp",EDGE,"E1401.3"),sQuery(id+"F6.wireOp",EDGE,"E1402.filletArc"),sQuery(id+"F6.wireOp",EDGE,"E1403.filletArc"),sQuery(id+"F6.wireOp",EDGE,"E1404.filletArc"),sQuery(id+"F6.wireOp",EDGE,"E1405.filletArc")])],"isStart":false});
            extrude(context, id + "F9", {"entities" : qUnion([Q0]), "endBound" : BoundingType.UP_TO_SURFACE, "oppositeDirection" : true, "endBoundEntityFace" : qUnion([Q1]), "depth" : 25 * mm});
        }
        {
            var Q0;
            Q0=makeQuery(id+"F8.imprint","IMPRINT",FACE,{"disambiguationData":[TD([[makeQuery(id+"F8.imprint","IMPRINT",EDGE,{"derivedFrom":sQuery(id+"F8.wireOp",EDGE,"E1406.0")}),1.0]])]});
            var Q1;
            Q1=makeQuery(id+"F8.imprint","IMPRINT",FACE,{"disambiguationData":[TD([[makeQuery(id+"F8.imprint","IMPRINT",EDGE,{"derivedFrom":makeQuery(id+"F7.opExtrude","CAP_EDGE",EDGE,{"disambiguationData":[OSD([sQuery(id+"F6.wireOp",EDGE,"E1401.0")])],"isStart":true})}),1.0]])]});
            extrude(context, id + "F10", {"entities" : qUnion([Q0, Q1]), "operationType" : NewBodyOperationType.ADD, "depth" : 1.26 * mm});
        }
    });
